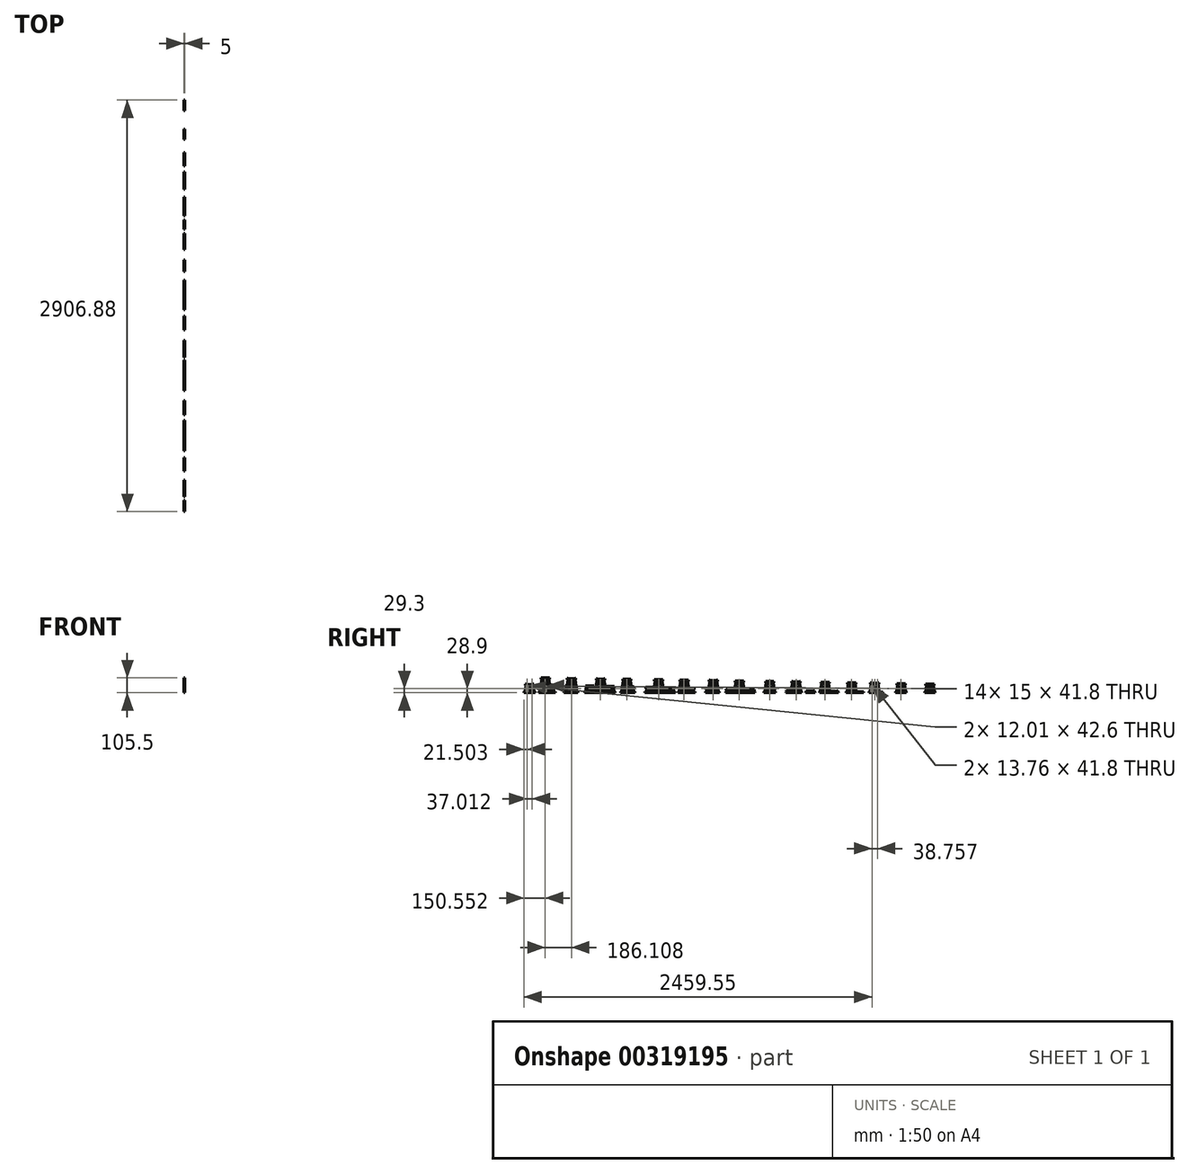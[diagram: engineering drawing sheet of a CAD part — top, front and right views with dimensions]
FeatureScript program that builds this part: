
annotation { "Feature Type Name" : "Feature", "Feature Type Description" : "" }
export const myFeature = defineFeature(function(context is Context, id is Id, definition is map)
    precondition{}
    {
        {
            var Q0;
            Q0=qCreatedBy(makeId("Right.planeOp"),FACE);
            var sketch = newSketch(context, id + "F0", { "sketchPlane" : qUnion([Q0])});
            skLineSegment(sketch, "E0", {"start": v(0, 134.08) * mm, "end": v(0, 0) * mm, "construction": true});
            skLineSegment(sketch, "E1", {"start": v(-77.1, 0) * mm, "end": v(4239.96, 0) * mm, "construction": true});
            skLineSegment(sketch, "E2.bottom", {"start": v(-24.5, 104.5) * mm, "end": v(0, 104.5) * mm});
            skLineSegment(sketch, "E2.top", {"start": v(-19.5, 96.5) * mm, "end": v(-12.5, 96.5) * mm});
            skLineSegment(sketch, "E2.left", {"start": v(-24.5, 104.5) * mm, "end": v(-24.5, 102.5) * mm});
            skLineSegment(sketch, "E3.bottom", {"start": v(-45.1, 0) * mm, "end": v(45.1, 0) * mm});
            skLineSegment(sketch, "E3.left", {"start": v(-45.1, 0) * mm, "end": v(-45.1, 8) * mm});
            skLineSegment(sketch, "E4.left", {"start": v(-12.5, 96.5) * mm, "end": v(-12.5, 54.8) * mm});
            skLineSegment(sketch, "E5", {"start": v(-40.1, 8) * mm, "end": v(-24.5, 96.5) * mm});
            skLineSegment(sketch, "E6", {"start": v(-45.1, 8) * mm, "end": v(-40.1, 8) * mm});
            skLineSegment(sketch, "E7.trimOffspring", {"start": v(-32.6, 8) * mm, "end": v(-26.42, 49.8) * mm});
            skLineSegment(sketch, "E8.bottom", {"start": v(-30, 105.5) * mm, "end": v(-25, 105.5) * mm});
            skLineSegment(sketch, "E8.top", {"start": v(-30, 96.5) * mm, "end": v(-24.5, 96.5) * mm});
            skLineSegment(sketch, "E8.left", {"start": v(-30, 105.5) * mm, "end": v(-30, 96.5) * mm});
            skLineSegment(sketch, "E9.right", {"start": v(-25, 105.5) * mm, "end": v(-25, 102.5) * mm});
            skLineSegment(sketch, "E10", {"start": v(-25, 102.5) * mm, "end": v(-24.5, 102.5) * mm});
            skLineSegment(sketch, "E11", {"start": v(-7.5, 96.5) * mm, "end": v(-7.5, 54.8) * mm});
            skLineSegment(sketch, "E12.trimOffspring", {"start": v(-32.6, 8) * mm, "end": v(-12.5, 8) * mm});
            skLineSegment(sketch, "E13.trimOffspring", {"start": v(-7.5, 49.8) * mm, "end": v(-7.5, 8) * mm});
            skLineSegment(sketch, "E14.trimOffspring", {"start": v(-12.5, 49.8) * mm, "end": v(-12.5, 8) * mm});
            skLineSegment(sketch, "E15.trimOffspring", {"start": v(-25.67, 54.8) * mm, "end": v(-19.5, 96.5) * mm});
            skLineSegment(sketch, "E16", {"start": v(59.07, 96.5) * mm, "end": v(-79.32, 96.5) * mm, "construction": true});
            skLineSegment(sketch, "E17", {"start": v(-25.67, 54.8) * mm, "end": v(0, 54.8) * mm});
            skLineSegment(sketch, "E18", {"start": v(-7.5, 96.5) * mm, "end": v(0, 96.5) * mm});
            skLineSegment(sketch, "E19", {"start": v(-26.42, 49.8) * mm, "end": v(0, 49.8) * mm});
            skLineSegment(sketch, "E20.MirrorCS", {"start": v(24.5, 104.5) * mm, "end": v(0, 104.5) * mm});
            skLineSegment(sketch, "E21.MirrorCS", {"start": v(24.5, 104.5) * mm, "end": v(24.5, 102.5) * mm});
            skLineSegment(sketch, "E22.MirrorCS", {"start": v(25, 102.5) * mm, "end": v(24.5, 102.5) * mm});
            skLineSegment(sketch, "E23.MirrorCS", {"start": v(25, 105.5) * mm, "end": v(25, 102.5) * mm});
            skLineSegment(sketch, "E24.MirrorCS", {"start": v(30, 105.5) * mm, "end": v(25, 105.5) * mm});
            skLineSegment(sketch, "E25.MirrorCS", {"start": v(30, 105.5) * mm, "end": v(30, 96.5) * mm});
            skLineSegment(sketch, "E26.MirrorCS", {"start": v(30, 96.5) * mm, "end": v(24.5, 96.5) * mm});
            skLineSegment(sketch, "E27.MirrorCS", {"start": v(19.5, 96.5) * mm, "end": v(12.5, 96.5) * mm});
            skLineSegment(sketch, "E28.MirrorCS", {"start": v(7.5, 96.5) * mm, "end": v(0, 96.5) * mm});
            skLineSegment(sketch, "E29.MirrorCS", {"start": v(7.5, 96.5) * mm, "end": v(7.5, 54.8) * mm});
            skLineSegment(sketch, "E30.MirrorCS", {"start": v(12.5, 96.5) * mm, "end": v(12.5, 54.8) * mm});
            skLineSegment(sketch, "E31.MirrorCS", {"start": v(25.67, 54.8) * mm, "end": v(19.5, 96.5) * mm});
            skLineSegment(sketch, "E32.MirrorCS", {"start": v(40.1, 8) * mm, "end": v(24.5, 96.5) * mm});
            skLineSegment(sketch, "E33.MirrorCS", {"start": v(25.67, 54.8) * mm, "end": v(0, 54.8) * mm});
            skLineSegment(sketch, "E34.MirrorCS", {"start": v(26.42, 49.8) * mm, "end": v(0, 49.8) * mm});
            skLineSegment(sketch, "E35.MirrorCS", {"start": v(7.5, 49.8) * mm, "end": v(7.5, 8) * mm});
            skLineSegment(sketch, "E36.MirrorCS", {"start": v(12.5, 49.8) * mm, "end": v(12.5, 8) * mm});
            skLineSegment(sketch, "E37.MirrorCS", {"start": v(32.6, 8) * mm, "end": v(12.5, 8) * mm});
            skLineSegment(sketch, "E38.MirrorCS", {"start": v(32.6, 8) * mm, "end": v(26.42, 49.8) * mm});
            skPoint(sketch, "E39.orphan", {"position": v(-32.73, 49.8) * mm});
            skPoint(sketch, "E40.orphan", {"position": v(32.73, 49.8) * mm});
            skLineSegment(sketch, "E41", {"start": v(-7.5, 8) * mm, "end": v(0, 8) * mm});
            skLineSegment(sketch, "E42.MirrorCS", {"start": v(7.5, 8) * mm, "end": v(0, 8) * mm});
            skLineSegment(sketch, "E43.MirrorCS", {"start": v(45.1, 0) * mm, "end": v(45.1, 8) * mm});
            skLineSegment(sketch, "E44.MirrorCS", {"start": v(45.1, 8) * mm, "end": v(40.1, 8) * mm});
            skLineSegment(sketch, "E45", {"start": v(197.1, 85.33) * mm, "end": v(197.1, 0) * mm, "construction": true});
            skLineSegment(sketch, "E46", {"start": v(119.98, 0) * mm, "end": v(260.76, 0) * mm, "construction": true});
            skLineSegment(sketch, "E47.bottom", {"start": v(172.6, 104.5) * mm, "end": v(197.1, 104.5) * mm});
            skLineSegment(sketch, "E47.top", {"start": v(177.6, 96.5) * mm, "end": v(184.6, 96.5) * mm});
            skLineSegment(sketch, "E47.left", {"start": v(172.6, 104.5) * mm, "end": v(172.6, 102.5) * mm});
            skLineSegment(sketch, "E48.bottom", {"start": v(151.99, 0) * mm, "end": v(242.2, 0) * mm});
            skLineSegment(sketch, "E48.left", {"start": v(151.99, 0) * mm, "end": v(151.99, 8) * mm});
            skLineSegment(sketch, "E49.left", {"start": v(184.6, 96.5) * mm, "end": v(184.6, 54.8) * mm});
            skLineSegment(sketch, "E50", {"start": v(156.99, 8) * mm, "end": v(172.6, 96.5) * mm});
            skLineSegment(sketch, "E51", {"start": v(151.99, 8) * mm, "end": v(156.99, 8) * mm});
            skLineSegment(sketch, "E52.trimOffspring", {"start": v(164.49, 8) * mm, "end": v(170.68, 49.8) * mm});
            skLineSegment(sketch, "E53.bottom", {"start": v(167.1, 105.5) * mm, "end": v(172.1, 105.5) * mm});
            skLineSegment(sketch, "E53.top", {"start": v(167.1, 96.5) * mm, "end": v(172.6, 96.5) * mm});
            skLineSegment(sketch, "E53.left", {"start": v(167.1, 105.5) * mm, "end": v(167.1, 96.5) * mm});
            skLineSegment(sketch, "E54.right", {"start": v(172.1, 105.5) * mm, "end": v(172.1, 102.5) * mm});
            skLineSegment(sketch, "E55", {"start": v(172.1, 102.5) * mm, "end": v(172.6, 102.5) * mm});
            skLineSegment(sketch, "E56", {"start": v(189.6, 96.5) * mm, "end": v(189.6, 54.8) * mm});
            skLineSegment(sketch, "E57.trimOffspring", {"start": v(164.49, 8) * mm, "end": v(184.6, 8) * mm});
            skLineSegment(sketch, "E58.trimOffspring", {"start": v(189.6, 49.8) * mm, "end": v(189.6, 8) * mm});
            skLineSegment(sketch, "E59.trimOffspring", {"start": v(184.6, 49.8) * mm, "end": v(184.6, 8) * mm});
            skLineSegment(sketch, "E60.trimOffspring", {"start": v(171.42, 54.8) * mm, "end": v(177.6, 96.5) * mm});
            skLineSegment(sketch, "E61", {"start": v(256.16, 96.5) * mm, "end": v(117.77, 96.5) * mm, "construction": true});
            skLineSegment(sketch, "E62", {"start": v(171.42, 54.8) * mm, "end": v(197.1, 54.8) * mm});
            skLineSegment(sketch, "E63", {"start": v(189.6, 96.5) * mm, "end": v(197.1, 96.5) * mm});
            skLineSegment(sketch, "E64", {"start": v(170.68, 49.8) * mm, "end": v(197.1, 49.8) * mm});
            skLineSegment(sketch, "E65.MirrorCS", {"start": v(221.6, 104.5) * mm, "end": v(197.1, 104.5) * mm});
            skLineSegment(sketch, "E66.MirrorCS", {"start": v(221.6, 104.5) * mm, "end": v(221.6, 102.5) * mm});
            skLineSegment(sketch, "E67.MirrorCS", {"start": v(222.1, 102.5) * mm, "end": v(221.6, 102.5) * mm});
            skLineSegment(sketch, "E68.MirrorCS", {"start": v(222.1, 105.5) * mm, "end": v(222.1, 102.5) * mm});
            skLineSegment(sketch, "E69.MirrorCS", {"start": v(227.1, 105.5) * mm, "end": v(222.1, 105.5) * mm});
            skLineSegment(sketch, "E70.MirrorCS", {"start": v(227.1, 105.5) * mm, "end": v(227.1, 96.5) * mm});
            skLineSegment(sketch, "E71.MirrorCS", {"start": v(227.1, 96.5) * mm, "end": v(221.6, 96.5) * mm});
            skLineSegment(sketch, "E72.MirrorCS", {"start": v(216.6, 96.5) * mm, "end": v(209.6, 96.5) * mm});
            skLineSegment(sketch, "E73.MirrorCS", {"start": v(204.6, 96.5) * mm, "end": v(197.1, 96.5) * mm});
            skLineSegment(sketch, "E74.MirrorCS", {"start": v(204.6, 96.5) * mm, "end": v(204.6, 54.8) * mm});
            skLineSegment(sketch, "E75.MirrorCS", {"start": v(209.6, 96.5) * mm, "end": v(209.6, 54.8) * mm});
            skLineSegment(sketch, "E76.MirrorCS", {"start": v(222.77, 54.8) * mm, "end": v(216.6, 96.5) * mm});
            skLineSegment(sketch, "E77.MirrorCS", {"start": v(237.2, 8) * mm, "end": v(221.6, 96.5) * mm});
            skLineSegment(sketch, "E78.MirrorCS", {"start": v(222.77, 54.8) * mm, "end": v(197.1, 54.8) * mm});
            skLineSegment(sketch, "E79.MirrorCS", {"start": v(223.5, 49.8) * mm, "end": v(197.1, 49.8) * mm});
            skLineSegment(sketch, "E80.MirrorCS", {"start": v(204.6, 49.8) * mm, "end": v(204.6, 8) * mm});
            skLineSegment(sketch, "E81.MirrorCS", {"start": v(209.6, 49.8) * mm, "end": v(209.6, 8) * mm});
            skLineSegment(sketch, "E82.MirrorCS", {"start": v(229.7, 8) * mm, "end": v(209.6, 8) * mm});
            skLineSegment(sketch, "E83.MirrorCS", {"start": v(229.7, 8) * mm, "end": v(223.5, 49.8) * mm});
            skPoint(sketch, "E84.orphan", {"position": v(164.36, 49.8) * mm});
            skPoint(sketch, "E85.orphan", {"position": v(229.83, 49.8) * mm});
            skLineSegment(sketch, "E86", {"start": v(189.6, 8) * mm, "end": v(197.1, 8) * mm});
            skLineSegment(sketch, "E87.MirrorCS", {"start": v(204.6, 8) * mm, "end": v(197.1, 8) * mm});
            skLineSegment(sketch, "E88.MirrorCS", {"start": v(242.2, 0) * mm, "end": v(242.2, 8) * mm});
            skLineSegment(sketch, "E89.MirrorCS", {"start": v(242.2, 8) * mm, "end": v(237.2, 8) * mm});
            skLineSegment(sketch, "E90", {"start": v(383.2, 89.08) * mm, "end": v(383.2, 0) * mm, "construction": true});
            skLineSegment(sketch, "E91", {"start": v(315.11, 0) * mm, "end": v(455.9, 0) * mm, "construction": true});
            skLineSegment(sketch, "E92.bottom", {"start": v(358.7, 100.6) * mm, "end": v(383.2, 100.6) * mm});
            skLineSegment(sketch, "E92.top", {"start": v(363.7, 92.6) * mm, "end": v(370.7, 92.6) * mm});
            skLineSegment(sketch, "E92.left", {"start": v(358.7, 100.6) * mm, "end": v(358.7, 98.6) * mm});
            skLineSegment(sketch, "E93.bottom", {"start": v(338.78, 0) * mm, "end": v(427.62, 0) * mm});
            skLineSegment(sketch, "E93.left", {"start": v(338.78, 0) * mm, "end": v(338.78, 8) * mm});
            skLineSegment(sketch, "E94.left", {"start": v(370.7, 92.6) * mm, "end": v(370.7, 54.8) * mm});
            skLineSegment(sketch, "E95", {"start": v(343.78, 8) * mm, "end": v(358.7, 92.6) * mm});
            skLineSegment(sketch, "E96", {"start": v(338.78, 8) * mm, "end": v(343.78, 8) * mm});
            skLineSegment(sketch, "E97.trimOffspring", {"start": v(351.28, 8) * mm, "end": v(357.42, 49.8) * mm});
            skLineSegment(sketch, "E98.bottom", {"start": v(353.2, 101.6) * mm, "end": v(358.2, 101.6) * mm});
            skLineSegment(sketch, "E98.top", {"start": v(353.2, 92.6) * mm, "end": v(358.7, 92.6) * mm});
            skLineSegment(sketch, "E98.left", {"start": v(353.2, 101.6) * mm, "end": v(353.2, 92.6) * mm});
            skLineSegment(sketch, "E99.right", {"start": v(358.2, 101.6) * mm, "end": v(358.2, 98.6) * mm});
            skLineSegment(sketch, "E100", {"start": v(358.2, 98.6) * mm, "end": v(358.7, 98.6) * mm});
            skLineSegment(sketch, "E101", {"start": v(375.7, 92.6) * mm, "end": v(375.7, 54.8) * mm});
            skLineSegment(sketch, "E102.trimOffspring", {"start": v(351.28, 8) * mm, "end": v(370.7, 8) * mm});
            skLineSegment(sketch, "E103.trimOffspring", {"start": v(375.7, 49.8) * mm, "end": v(375.7, 8) * mm});
            skLineSegment(sketch, "E104.trimOffspring", {"start": v(370.7, 49.8) * mm, "end": v(370.7, 8) * mm});
            skLineSegment(sketch, "E105.trimOffspring", {"start": v(358.15, 54.8) * mm, "end": v(363.7, 92.6) * mm});
            skLineSegment(sketch, "E106", {"start": v(451.29, 92.6) * mm, "end": v(312.9, 92.6) * mm, "construction": true});
            skLineSegment(sketch, "E107", {"start": v(358.15, 54.8) * mm, "end": v(383.2, 54.8) * mm});
            skLineSegment(sketch, "E108", {"start": v(375.7, 92.6) * mm, "end": v(383.2, 92.6) * mm});
            skLineSegment(sketch, "E109", {"start": v(357.42, 49.8) * mm, "end": v(383.2, 49.8) * mm});
            skLineSegment(sketch, "E110.MirrorCS", {"start": v(407.7, 100.6) * mm, "end": v(383.2, 100.6) * mm});
            skLineSegment(sketch, "E111.MirrorCS", {"start": v(407.7, 100.6) * mm, "end": v(407.7, 98.6) * mm});
            skLineSegment(sketch, "E112.MirrorCS", {"start": v(408.2, 98.6) * mm, "end": v(407.7, 98.6) * mm});
            skLineSegment(sketch, "E113.MirrorCS", {"start": v(408.2, 101.6) * mm, "end": v(408.2, 98.6) * mm});
            skLineSegment(sketch, "E114.MirrorCS", {"start": v(413.2, 101.6) * mm, "end": v(408.2, 101.6) * mm});
            skLineSegment(sketch, "E115.MirrorCS", {"start": v(413.2, 101.6) * mm, "end": v(413.2, 92.6) * mm});
            skLineSegment(sketch, "E116.MirrorCS", {"start": v(413.2, 92.6) * mm, "end": v(407.7, 92.6) * mm});
            skLineSegment(sketch, "E117.MirrorCS", {"start": v(402.7, 92.6) * mm, "end": v(395.7, 92.6) * mm});
            skLineSegment(sketch, "E118.MirrorCS", {"start": v(390.7, 92.6) * mm, "end": v(383.2, 92.6) * mm});
            skLineSegment(sketch, "E119.MirrorCS", {"start": v(390.7, 92.6) * mm, "end": v(390.7, 54.8) * mm});
            skLineSegment(sketch, "E120.MirrorCS", {"start": v(395.7, 92.6) * mm, "end": v(395.7, 54.8) * mm});
            skLineSegment(sketch, "E121.MirrorCS", {"start": v(408.25, 54.8) * mm, "end": v(402.7, 92.6) * mm});
            skLineSegment(sketch, "E122.MirrorCS", {"start": v(422.62, 8) * mm, "end": v(407.7, 92.6) * mm});
            skLineSegment(sketch, "E123.MirrorCS", {"start": v(408.25, 54.8) * mm, "end": v(383.2, 54.8) * mm});
            skLineSegment(sketch, "E124.MirrorCS", {"start": v(408.98, 49.8) * mm, "end": v(383.2, 49.8) * mm});
            skLineSegment(sketch, "E125.MirrorCS", {"start": v(390.7, 49.8) * mm, "end": v(390.7, 8) * mm});
            skLineSegment(sketch, "E126.MirrorCS", {"start": v(395.7, 49.8) * mm, "end": v(395.7, 8) * mm});
            skLineSegment(sketch, "E127.MirrorCS", {"start": v(415.12, 8) * mm, "end": v(395.7, 8) * mm});
            skLineSegment(sketch, "E128.MirrorCS", {"start": v(415.12, 8) * mm, "end": v(408.98, 49.8) * mm});
            skPoint(sketch, "E129.orphan", {"position": v(351.15, 49.8) * mm});
            skPoint(sketch, "E130.orphan", {"position": v(415.25, 49.8) * mm});
            skLineSegment(sketch, "E131", {"start": v(375.7, 8) * mm, "end": v(383.2, 8) * mm});
            skLineSegment(sketch, "E132.MirrorCS", {"start": v(390.7, 8) * mm, "end": v(383.2, 8) * mm});
            skLineSegment(sketch, "E133.MirrorCS", {"start": v(427.62, 0) * mm, "end": v(427.62, 8) * mm});
            skLineSegment(sketch, "E134.MirrorCS", {"start": v(427.62, 8) * mm, "end": v(422.62, 8) * mm});
            skLineSegment(sketch, "E135", {"start": v(587.84, 113.08) * mm, "end": v(587.84, 0) * mm, "construction": true});
            skLineSegment(sketch, "E136", {"start": v(510.73, 0) * mm, "end": v(651.5, 0) * mm, "construction": true});
            skLineSegment(sketch, "E137.bottom", {"start": v(563.34, 96.7) * mm, "end": v(587.84, 96.7) * mm});
            skLineSegment(sketch, "E137.top", {"start": v(568.34, 88.7) * mm, "end": v(575.34, 88.7) * mm});
            skLineSegment(sketch, "E137.left", {"start": v(563.34, 96.7) * mm, "end": v(563.34, 94.7) * mm});
            skLineSegment(sketch, "E138.bottom", {"start": v(544.11, 0) * mm, "end": v(631.57, 0) * mm});
            skLineSegment(sketch, "E138.left", {"start": v(544.11, 0) * mm, "end": v(544.11, 8) * mm});
            skLineSegment(sketch, "E139.left", {"start": v(575.34, 88.7) * mm, "end": v(575.34, 54.8) * mm});
            skLineSegment(sketch, "E140", {"start": v(549.11, 8) * mm, "end": v(563.34, 88.7) * mm});
            skLineSegment(sketch, "E141", {"start": v(544.11, 8) * mm, "end": v(549.11, 8) * mm});
            skLineSegment(sketch, "E142.trimOffspring", {"start": v(556.61, 8) * mm, "end": v(562.69, 49.8) * mm});
            skLineSegment(sketch, "E143.bottom", {"start": v(557.84, 97.7) * mm, "end": v(562.84, 97.7) * mm});
            skLineSegment(sketch, "E143.top", {"start": v(557.84, 88.7) * mm, "end": v(563.34, 88.7) * mm});
            skLineSegment(sketch, "E143.left", {"start": v(557.84, 97.7) * mm, "end": v(557.84, 88.7) * mm});
            skLineSegment(sketch, "E144.right", {"start": v(562.84, 97.7) * mm, "end": v(562.84, 94.7) * mm});
            skLineSegment(sketch, "E145", {"start": v(562.84, 94.7) * mm, "end": v(563.34, 94.7) * mm});
            skLineSegment(sketch, "E146", {"start": v(580.34, 88.7) * mm, "end": v(580.34, 54.8) * mm});
            skLineSegment(sketch, "E147.trimOffspring", {"start": v(556.61, 8) * mm, "end": v(575.34, 8) * mm});
            skLineSegment(sketch, "E148.trimOffspring", {"start": v(580.34, 49.8) * mm, "end": v(580.34, 8) * mm});
            skLineSegment(sketch, "E149.trimOffspring", {"start": v(575.34, 49.8) * mm, "end": v(575.34, 8) * mm});
            skLineSegment(sketch, "E150.trimOffspring", {"start": v(563.41, 54.8) * mm, "end": v(568.34, 88.7) * mm});
            skLineSegment(sketch, "E151", {"start": v(646.9, 88.7) * mm, "end": v(508.52, 88.7) * mm, "construction": true});
            skLineSegment(sketch, "E152", {"start": v(563.41, 54.8) * mm, "end": v(587.84, 54.8) * mm});
            skLineSegment(sketch, "E153", {"start": v(580.34, 88.7) * mm, "end": v(587.84, 88.7) * mm});
            skLineSegment(sketch, "E154", {"start": v(562.69, 49.8) * mm, "end": v(587.84, 49.8) * mm});
            skLineSegment(sketch, "E155.MirrorCS", {"start": v(612.34, 96.7) * mm, "end": v(587.84, 96.7) * mm});
            skLineSegment(sketch, "E156.MirrorCS", {"start": v(612.34, 96.7) * mm, "end": v(612.34, 94.7) * mm});
            skLineSegment(sketch, "E157.MirrorCS", {"start": v(612.84, 94.7) * mm, "end": v(612.34, 94.7) * mm});
            skLineSegment(sketch, "E158.MirrorCS", {"start": v(612.84, 97.7) * mm, "end": v(612.84, 94.7) * mm});
            skLineSegment(sketch, "E159.MirrorCS", {"start": v(617.84, 97.7) * mm, "end": v(612.84, 97.7) * mm});
            skLineSegment(sketch, "E160.MirrorCS", {"start": v(617.84, 97.7) * mm, "end": v(617.84, 88.7) * mm});
            skLineSegment(sketch, "E161.MirrorCS", {"start": v(617.84, 88.7) * mm, "end": v(612.34, 88.7) * mm});
            skLineSegment(sketch, "E162.MirrorCS", {"start": v(607.34, 88.7) * mm, "end": v(600.34, 88.7) * mm});
            skLineSegment(sketch, "E163.MirrorCS", {"start": v(595.34, 88.7) * mm, "end": v(587.84, 88.7) * mm});
            skLineSegment(sketch, "E164.MirrorCS", {"start": v(595.34, 88.7) * mm, "end": v(595.34, 54.8) * mm});
            skLineSegment(sketch, "E165.MirrorCS", {"start": v(600.34, 88.7) * mm, "end": v(600.34, 54.8) * mm});
            skLineSegment(sketch, "E166.MirrorCS", {"start": v(612.27, 54.8) * mm, "end": v(607.34, 88.7) * mm});
            skLineSegment(sketch, "E167.MirrorCS", {"start": v(626.57, 8) * mm, "end": v(612.34, 88.7) * mm});
            skLineSegment(sketch, "E168.MirrorCS", {"start": v(612.27, 54.8) * mm, "end": v(587.84, 54.8) * mm});
            skLineSegment(sketch, "E169.MirrorCS", {"start": v(613, 49.8) * mm, "end": v(587.84, 49.8) * mm});
            skLineSegment(sketch, "E170.MirrorCS", {"start": v(595.34, 49.8) * mm, "end": v(595.34, 8) * mm});
            skLineSegment(sketch, "E171.MirrorCS", {"start": v(600.34, 49.8) * mm, "end": v(600.34, 8) * mm});
            skLineSegment(sketch, "E172.MirrorCS", {"start": v(619.07, 8) * mm, "end": v(600.34, 8) * mm});
            skLineSegment(sketch, "E173.MirrorCS", {"start": v(619.07, 8) * mm, "end": v(613, 49.8) * mm});
            skPoint(sketch, "E174.orphan", {"position": v(556.48, 49.8) * mm});
            skPoint(sketch, "E175.orphan", {"position": v(619.2, 49.8) * mm});
            skLineSegment(sketch, "E176", {"start": v(580.34, 8) * mm, "end": v(587.84, 8) * mm});
            skLineSegment(sketch, "E177.MirrorCS", {"start": v(595.34, 8) * mm, "end": v(587.84, 8) * mm});
            skLineSegment(sketch, "E178.MirrorCS", {"start": v(631.57, 0) * mm, "end": v(631.57, 8) * mm});
            skLineSegment(sketch, "E179.MirrorCS", {"start": v(631.57, 8) * mm, "end": v(626.57, 8) * mm});
            skLineSegment(sketch, "E180", {"start": v(773.95, 116.82) * mm, "end": v(773.95, 0) * mm, "construction": true});
            skLineSegment(sketch, "E181", {"start": v(705.86, 0) * mm, "end": v(846.64, 0) * mm, "construction": true});
            skLineSegment(sketch, "E182.bottom", {"start": v(749.45, 95.8) * mm, "end": v(773.95, 95.8) * mm});
            skLineSegment(sketch, "E182.top", {"start": v(754.45, 87.8) * mm, "end": v(761.45, 87.8) * mm});
            skLineSegment(sketch, "E182.left", {"start": v(749.45, 95.8) * mm, "end": v(749.45, 93.8) * mm});
            skLineSegment(sketch, "E183.bottom", {"start": v(730.38, 0) * mm, "end": v(817.52, 0) * mm});
            skLineSegment(sketch, "E183.left", {"start": v(730.38, 0) * mm, "end": v(730.38, 8) * mm});
            skLineSegment(sketch, "E184.left", {"start": v(761.45, 87.8) * mm, "end": v(761.45, 54.8) * mm});
            skLineSegment(sketch, "E185", {"start": v(735.38, 8) * mm, "end": v(749.45, 87.8) * mm});
            skLineSegment(sketch, "E186", {"start": v(730.38, 8) * mm, "end": v(735.38, 8) * mm});
            skLineSegment(sketch, "E187.trimOffspring", {"start": v(742.88, 8) * mm, "end": v(748.94, 49.8) * mm});
            skLineSegment(sketch, "E188.bottom", {"start": v(743.95, 96.8) * mm, "end": v(748.95, 96.8) * mm});
            skLineSegment(sketch, "E188.top", {"start": v(743.95, 87.8) * mm, "end": v(749.45, 87.8) * mm});
            skLineSegment(sketch, "E188.left", {"start": v(743.95, 96.8) * mm, "end": v(743.95, 87.8) * mm});
            skLineSegment(sketch, "E189.right", {"start": v(748.95, 96.8) * mm, "end": v(748.95, 93.8) * mm});
            skLineSegment(sketch, "E190", {"start": v(748.95, 93.8) * mm, "end": v(749.45, 93.8) * mm});
            skLineSegment(sketch, "E191", {"start": v(766.45, 87.8) * mm, "end": v(766.45, 54.8) * mm});
            skLineSegment(sketch, "E192.trimOffspring", {"start": v(742.88, 8) * mm, "end": v(761.45, 8) * mm});
            skLineSegment(sketch, "E193.trimOffspring", {"start": v(766.45, 49.8) * mm, "end": v(766.45, 8) * mm});
            skLineSegment(sketch, "E194.trimOffspring", {"start": v(761.45, 49.8) * mm, "end": v(761.45, 8) * mm});
            skLineSegment(sketch, "E195.trimOffspring", {"start": v(749.66, 54.8) * mm, "end": v(754.45, 87.8) * mm});
            skLineSegment(sketch, "E196", {"start": v(842.04, 87.8) * mm, "end": v(703.65, 87.8) * mm, "construction": true});
            skLineSegment(sketch, "E197", {"start": v(749.66, 54.8) * mm, "end": v(773.95, 54.8) * mm});
            skLineSegment(sketch, "E198", {"start": v(766.45, 87.8) * mm, "end": v(773.95, 87.8) * mm});
            skLineSegment(sketch, "E199", {"start": v(748.94, 49.8) * mm, "end": v(773.95, 49.8) * mm});
            skLineSegment(sketch, "E200.MirrorCS", {"start": v(798.45, 95.8) * mm, "end": v(773.95, 95.8) * mm});
            skLineSegment(sketch, "E201.MirrorCS", {"start": v(798.45, 95.8) * mm, "end": v(798.45, 93.8) * mm});
            skLineSegment(sketch, "E202.MirrorCS", {"start": v(798.95, 93.8) * mm, "end": v(798.45, 93.8) * mm});
            skLineSegment(sketch, "E203.MirrorCS", {"start": v(798.95, 96.8) * mm, "end": v(798.95, 93.8) * mm});
            skLineSegment(sketch, "E204.MirrorCS", {"start": v(803.95, 96.8) * mm, "end": v(798.95, 96.8) * mm});
            skLineSegment(sketch, "E205.MirrorCS", {"start": v(803.95, 96.8) * mm, "end": v(803.95, 87.8) * mm});
            skLineSegment(sketch, "E206.MirrorCS", {"start": v(803.95, 87.8) * mm, "end": v(798.45, 87.8) * mm});
            skLineSegment(sketch, "E207.MirrorCS", {"start": v(793.45, 87.8) * mm, "end": v(786.45, 87.8) * mm});
            skLineSegment(sketch, "E208.MirrorCS", {"start": v(781.45, 87.8) * mm, "end": v(773.95, 87.8) * mm});
            skLineSegment(sketch, "E209.MirrorCS", {"start": v(781.45, 87.8) * mm, "end": v(781.45, 54.8) * mm});
            skLineSegment(sketch, "E210.MirrorCS", {"start": v(786.45, 87.8) * mm, "end": v(786.45, 54.8) * mm});
            skLineSegment(sketch, "E211.MirrorCS", {"start": v(798.23, 54.8) * mm, "end": v(793.45, 87.8) * mm});
            skLineSegment(sketch, "E212.MirrorCS", {"start": v(812.52, 8) * mm, "end": v(798.45, 87.8) * mm});
            skLineSegment(sketch, "E213.MirrorCS", {"start": v(798.23, 54.8) * mm, "end": v(773.95, 54.8) * mm});
            skLineSegment(sketch, "E214.MirrorCS", {"start": v(798.96, 49.8) * mm, "end": v(773.95, 49.8) * mm});
            skLineSegment(sketch, "E215.MirrorCS", {"start": v(781.45, 49.8) * mm, "end": v(781.45, 8) * mm});
            skLineSegment(sketch, "E216.MirrorCS", {"start": v(786.45, 49.8) * mm, "end": v(786.45, 8) * mm});
            skLineSegment(sketch, "E217.MirrorCS", {"start": v(805.02, 8) * mm, "end": v(786.45, 8) * mm});
            skLineSegment(sketch, "E218.MirrorCS", {"start": v(805.02, 8) * mm, "end": v(798.96, 49.8) * mm});
            skPoint(sketch, "E219.orphan", {"position": v(742.75, 49.8) * mm});
            skPoint(sketch, "E220.orphan", {"position": v(805.15, 49.8) * mm});
            skLineSegment(sketch, "E221", {"start": v(766.45, 8) * mm, "end": v(773.95, 8) * mm});
            skLineSegment(sketch, "E222.MirrorCS", {"start": v(781.45, 8) * mm, "end": v(773.95, 8) * mm});
            skLineSegment(sketch, "E223.MirrorCS", {"start": v(817.52, 0) * mm, "end": v(817.52, 8) * mm});
            skLineSegment(sketch, "E224.MirrorCS", {"start": v(817.52, 8) * mm, "end": v(812.52, 8) * mm});
            skLineSegment(sketch, "E225", {"start": v(998.65, 106.46) * mm, "end": v(998.65, 0) * mm, "construction": true});
            skLineSegment(sketch, "E226", {"start": v(917.44, 0) * mm, "end": v(1058.21, 0) * mm, "construction": true});
            skLineSegment(sketch, "E227.bottom", {"start": v(974.15, 91.9) * mm, "end": v(998.65, 91.9) * mm});
            skLineSegment(sketch, "E227.top", {"start": v(979.15, 83.9) * mm, "end": v(986.15, 83.9) * mm});
            skLineSegment(sketch, "E227.left", {"start": v(974.15, 91.9) * mm, "end": v(974.15, 89.9) * mm});
            skLineSegment(sketch, "E228.bottom", {"start": v(955.77, 0) * mm, "end": v(1041.54, 0) * mm});
            skLineSegment(sketch, "E228.left", {"start": v(955.77, 0) * mm, "end": v(955.77, 8) * mm});
            skLineSegment(sketch, "E229.left", {"start": v(986.15, 83.9) * mm, "end": v(986.15, 54.8) * mm});
            skLineSegment(sketch, "E230", {"start": v(960.77, 8) * mm, "end": v(974.15, 83.9) * mm});
            skLineSegment(sketch, "E231", {"start": v(955.77, 8) * mm, "end": v(960.77, 8) * mm});
            skLineSegment(sketch, "E232.trimOffspring", {"start": v(968.27, 8) * mm, "end": v(974.26, 49.8) * mm});
            skLineSegment(sketch, "E233.bottom", {"start": v(968.65, 92.9) * mm, "end": v(973.65, 92.9) * mm});
            skLineSegment(sketch, "E233.top", {"start": v(968.65, 83.9) * mm, "end": v(974.15, 83.9) * mm});
            skLineSegment(sketch, "E233.left", {"start": v(968.65, 92.9) * mm, "end": v(968.65, 83.9) * mm});
            skLineSegment(sketch, "E234.right", {"start": v(973.65, 92.9) * mm, "end": v(973.65, 89.9) * mm});
            skLineSegment(sketch, "E235", {"start": v(973.65, 89.9) * mm, "end": v(974.15, 89.9) * mm});
            skLineSegment(sketch, "E236", {"start": v(991.15, 83.9) * mm, "end": v(991.15, 54.8) * mm});
            skLineSegment(sketch, "E237.trimOffspring", {"start": v(968.27, 8) * mm, "end": v(986.15, 8) * mm});
            skLineSegment(sketch, "E238.trimOffspring", {"start": v(991.15, 49.8) * mm, "end": v(991.15, 8) * mm});
            skLineSegment(sketch, "E239.trimOffspring", {"start": v(986.15, 49.8) * mm, "end": v(986.15, 8) * mm});
            skLineSegment(sketch, "E240.trimOffspring", {"start": v(974.98, 54.8) * mm, "end": v(979.15, 83.9) * mm});
            skLineSegment(sketch, "E241", {"start": v(1053.61, 83.9) * mm, "end": v(915.23, 83.9) * mm, "construction": true});
            skLineSegment(sketch, "E242", {"start": v(974.98, 54.8) * mm, "end": v(998.65, 54.8) * mm});
            skLineSegment(sketch, "E243", {"start": v(991.15, 83.9) * mm, "end": v(998.65, 83.9) * mm});
            skLineSegment(sketch, "E244", {"start": v(974.26, 49.8) * mm, "end": v(998.65, 49.8) * mm});
            skLineSegment(sketch, "E245.MirrorCS", {"start": v(1023.15, 91.9) * mm, "end": v(998.65, 91.9) * mm});
            skLineSegment(sketch, "E246.MirrorCS", {"start": v(1023.15, 91.9) * mm, "end": v(1023.15, 89.9) * mm});
            skLineSegment(sketch, "E247.MirrorCS", {"start": v(1023.65, 89.9) * mm, "end": v(1023.15, 89.9) * mm});
            skLineSegment(sketch, "E248.MirrorCS", {"start": v(1023.65, 92.9) * mm, "end": v(1023.65, 89.9) * mm});
            skLineSegment(sketch, "E249.MirrorCS", {"start": v(1028.65, 92.9) * mm, "end": v(1023.65, 92.9) * mm});
            skLineSegment(sketch, "E250.MirrorCS", {"start": v(1028.65, 92.9) * mm, "end": v(1028.65, 83.9) * mm});
            skLineSegment(sketch, "E251.MirrorCS", {"start": v(1028.65, 83.9) * mm, "end": v(1023.15, 83.9) * mm});
            skLineSegment(sketch, "E252.MirrorCS", {"start": v(1018.15, 83.9) * mm, "end": v(1011.15, 83.9) * mm});
            skLineSegment(sketch, "E253.MirrorCS", {"start": v(1006.15, 83.9) * mm, "end": v(998.65, 83.9) * mm});
            skLineSegment(sketch, "E254.MirrorCS", {"start": v(1006.15, 83.9) * mm, "end": v(1006.15, 54.8) * mm});
            skLineSegment(sketch, "E255.MirrorCS", {"start": v(1011.15, 83.9) * mm, "end": v(1011.15, 54.8) * mm});
            skLineSegment(sketch, "E256.MirrorCS", {"start": v(1022.33, 54.8) * mm, "end": v(1018.15, 83.9) * mm});
            skLineSegment(sketch, "E257.MirrorCS", {"start": v(1036.54, 8) * mm, "end": v(1023.15, 83.9) * mm});
            skLineSegment(sketch, "E258.MirrorCS", {"start": v(1022.33, 54.8) * mm, "end": v(998.65, 54.8) * mm});
            skLineSegment(sketch, "E259.MirrorCS", {"start": v(1023.04, 49.8) * mm, "end": v(998.65, 49.8) * mm});
            skLineSegment(sketch, "E260.MirrorCS", {"start": v(1006.15, 49.8) * mm, "end": v(1006.15, 8) * mm});
            skLineSegment(sketch, "E261.MirrorCS", {"start": v(1011.15, 49.8) * mm, "end": v(1011.15, 8) * mm});
            skLineSegment(sketch, "E262.MirrorCS", {"start": v(1029.04, 8) * mm, "end": v(1011.15, 8) * mm});
            skLineSegment(sketch, "E263.MirrorCS", {"start": v(1029.04, 8) * mm, "end": v(1023.04, 49.8) * mm});
            skPoint(sketch, "E264.orphan", {"position": v(968.14, 49.8) * mm});
            skPoint(sketch, "E265.orphan", {"position": v(1029.17, 49.8) * mm});
            skLineSegment(sketch, "E266", {"start": v(991.15, 8) * mm, "end": v(998.65, 8) * mm});
            skLineSegment(sketch, "E267.MirrorCS", {"start": v(1006.15, 8) * mm, "end": v(998.65, 8) * mm});
            skLineSegment(sketch, "E268.MirrorCS", {"start": v(1041.54, 0) * mm, "end": v(1041.54, 8) * mm});
            skLineSegment(sketch, "E269.MirrorCS", {"start": v(1041.54, 8) * mm, "end": v(1036.54, 8) * mm});
            skLineSegment(sketch, "E270", {"start": v(1178.73, 105.45) * mm, "end": v(1178.73, 0) * mm, "construction": true});
            skLineSegment(sketch, "E271", {"start": v(1112.57, 0) * mm, "end": v(1253.34, 0) * mm, "construction": true});
            skLineSegment(sketch, "E272.bottom", {"start": v(1154.23, 88) * mm, "end": v(1178.73, 88) * mm});
            skLineSegment(sketch, "E272.top", {"start": v(1159.23, 80) * mm, "end": v(1166.23, 80) * mm});
            skLineSegment(sketch, "E272.left", {"start": v(1154.23, 88) * mm, "end": v(1154.23, 86) * mm});
            skLineSegment(sketch, "E273.bottom", {"start": v(1136.53, 0) * mm, "end": v(1220.92, 0) * mm});
            skLineSegment(sketch, "E273.left", {"start": v(1136.53, 0) * mm, "end": v(1136.53, 8) * mm});
            skLineSegment(sketch, "E274.left", {"start": v(1166.23, 80) * mm, "end": v(1166.23, 54.8) * mm});
            skLineSegment(sketch, "E275", {"start": v(1141.53, 8) * mm, "end": v(1154.23, 80) * mm});
            skLineSegment(sketch, "E276", {"start": v(1136.53, 8) * mm, "end": v(1141.53, 8) * mm});
            skLineSegment(sketch, "E277.trimOffspring", {"start": v(1149.03, 8) * mm, "end": v(1154.95, 49.8) * mm});
            skLineSegment(sketch, "E278.bottom", {"start": v(1148.73, 89) * mm, "end": v(1153.73, 89) * mm});
            skLineSegment(sketch, "E278.top", {"start": v(1148.73, 80) * mm, "end": v(1154.23, 80) * mm});
            skLineSegment(sketch, "E278.left", {"start": v(1148.73, 89) * mm, "end": v(1148.73, 80) * mm});
            skLineSegment(sketch, "E279.right", {"start": v(1153.73, 89) * mm, "end": v(1153.73, 86) * mm});
            skLineSegment(sketch, "E280", {"start": v(1153.73, 86) * mm, "end": v(1154.23, 86) * mm});
            skLineSegment(sketch, "E281", {"start": v(1171.23, 80) * mm, "end": v(1171.23, 54.8) * mm});
            skLineSegment(sketch, "E282.trimOffspring", {"start": v(1149.03, 8) * mm, "end": v(1166.23, 8) * mm});
            skLineSegment(sketch, "E283.trimOffspring", {"start": v(1171.23, 49.8) * mm, "end": v(1171.23, 8) * mm});
            skLineSegment(sketch, "E284.trimOffspring", {"start": v(1166.23, 49.8) * mm, "end": v(1166.23, 8) * mm});
            skLineSegment(sketch, "E285.trimOffspring", {"start": v(1155.66, 54.8) * mm, "end": v(1159.23, 80) * mm});
            skLineSegment(sketch, "E286", {"start": v(1248.74, 80) * mm, "end": v(1110.36, 80) * mm, "construction": true});
            skLineSegment(sketch, "E287", {"start": v(1155.66, 54.8) * mm, "end": v(1178.73, 54.8) * mm});
            skLineSegment(sketch, "E288", {"start": v(1171.23, 80) * mm, "end": v(1178.73, 80) * mm});
            skLineSegment(sketch, "E289", {"start": v(1154.95, 49.8) * mm, "end": v(1178.73, 49.8) * mm});
            skLineSegment(sketch, "E290.MirrorCS", {"start": v(1203.23, 88) * mm, "end": v(1178.73, 88) * mm});
            skLineSegment(sketch, "E291.MirrorCS", {"start": v(1203.23, 88) * mm, "end": v(1203.23, 86) * mm});
            skLineSegment(sketch, "E292.MirrorCS", {"start": v(1203.73, 86) * mm, "end": v(1203.23, 86) * mm});
            skLineSegment(sketch, "E293.MirrorCS", {"start": v(1203.73, 89) * mm, "end": v(1203.73, 86) * mm});
            skLineSegment(sketch, "E294.MirrorCS", {"start": v(1208.73, 89) * mm, "end": v(1203.73, 89) * mm});
            skLineSegment(sketch, "E295.MirrorCS", {"start": v(1208.73, 89) * mm, "end": v(1208.73, 80) * mm});
            skLineSegment(sketch, "E296.MirrorCS", {"start": v(1208.73, 80) * mm, "end": v(1203.23, 80) * mm});
            skLineSegment(sketch, "E297.MirrorCS", {"start": v(1198.23, 80) * mm, "end": v(1191.23, 80) * mm});
            skLineSegment(sketch, "E298.MirrorCS", {"start": v(1186.23, 80) * mm, "end": v(1178.73, 80) * mm});
            skLineSegment(sketch, "E299.MirrorCS", {"start": v(1186.23, 80) * mm, "end": v(1186.23, 54.8) * mm});
            skLineSegment(sketch, "E300.MirrorCS", {"start": v(1191.23, 80) * mm, "end": v(1191.23, 54.8) * mm});
            skLineSegment(sketch, "E301.MirrorCS", {"start": v(1201.8, 54.8) * mm, "end": v(1198.23, 80) * mm});
            skLineSegment(sketch, "E302.MirrorCS", {"start": v(1215.92, 8) * mm, "end": v(1203.23, 80) * mm});
            skLineSegment(sketch, "E303.MirrorCS", {"start": v(1201.8, 54.8) * mm, "end": v(1178.73, 54.8) * mm});
            skLineSegment(sketch, "E304.MirrorCS", {"start": v(1202.5, 49.8) * mm, "end": v(1178.73, 49.8) * mm});
            skLineSegment(sketch, "E305.MirrorCS", {"start": v(1186.23, 49.8) * mm, "end": v(1186.23, 8) * mm});
            skLineSegment(sketch, "E306.MirrorCS", {"start": v(1191.23, 49.8) * mm, "end": v(1191.23, 8) * mm});
            skLineSegment(sketch, "E307.MirrorCS", {"start": v(1208.42, 8) * mm, "end": v(1191.23, 8) * mm});
            skLineSegment(sketch, "E308.MirrorCS", {"start": v(1208.42, 8) * mm, "end": v(1202.5, 49.8) * mm});
            skPoint(sketch, "E309.orphan", {"position": v(1148.9, 49.8) * mm});
            skPoint(sketch, "E310.orphan", {"position": v(1208.55, 49.8) * mm});
            skLineSegment(sketch, "E311", {"start": v(1171.23, 8) * mm, "end": v(1178.73, 8) * mm});
            skLineSegment(sketch, "E312.MirrorCS", {"start": v(1186.23, 8) * mm, "end": v(1178.73, 8) * mm});
            skLineSegment(sketch, "E313.MirrorCS", {"start": v(1220.92, 0) * mm, "end": v(1220.92, 8) * mm});
            skLineSegment(sketch, "E314.MirrorCS", {"start": v(1220.92, 8) * mm, "end": v(1215.92, 8) * mm});
            skLineSegment(sketch, "E315", {"start": v(1385.06, 114.47) * mm, "end": v(1385.06, 0) * mm, "construction": true});
            skLineSegment(sketch, "E316", {"start": v(1308.18, 0) * mm, "end": v(1448.96, 0) * mm, "construction": true});
            skLineSegment(sketch, "E317.bottom", {"start": v(1360.56, 87.1) * mm, "end": v(1385.06, 87.1) * mm});
            skLineSegment(sketch, "E317.top", {"start": v(1365.56, 79.1) * mm, "end": v(1372.56, 79.1) * mm});
            skLineSegment(sketch, "E317.left", {"start": v(1360.56, 87.1) * mm, "end": v(1360.56, 85.1) * mm});
            skLineSegment(sketch, "E318.bottom", {"start": v(1343.03, 0) * mm, "end": v(1427.1, 0) * mm});
            skLineSegment(sketch, "E318.left", {"start": v(1343.03, 0) * mm, "end": v(1343.03, 8) * mm});
            skLineSegment(sketch, "E319.left", {"start": v(1372.56, 79.1) * mm, "end": v(1372.56, 54.8) * mm});
            skLineSegment(sketch, "E320", {"start": v(1348.03, 8) * mm, "end": v(1360.56, 79.1) * mm});
            skLineSegment(sketch, "E321", {"start": v(1343.03, 8) * mm, "end": v(1348.03, 8) * mm});
            skLineSegment(sketch, "E322.trimOffspring", {"start": v(1355.53, 8) * mm, "end": v(1361.43, 49.8) * mm});
            skLineSegment(sketch, "E323.bottom", {"start": v(1355.06, 88.1) * mm, "end": v(1360.06, 88.1) * mm});
            skLineSegment(sketch, "E323.top", {"start": v(1355.06, 79.1) * mm, "end": v(1360.56, 79.1) * mm});
            skLineSegment(sketch, "E323.left", {"start": v(1355.06, 88.1) * mm, "end": v(1355.06, 79.1) * mm});
            skLineSegment(sketch, "E324.right", {"start": v(1360.06, 88.1) * mm, "end": v(1360.06, 85.1) * mm});
            skLineSegment(sketch, "E325", {"start": v(1360.06, 85.1) * mm, "end": v(1360.56, 85.1) * mm});
            skLineSegment(sketch, "E326", {"start": v(1377.56, 79.1) * mm, "end": v(1377.56, 54.8) * mm});
            skLineSegment(sketch, "E327.trimOffspring", {"start": v(1355.53, 8) * mm, "end": v(1372.56, 8) * mm});
            skLineSegment(sketch, "E328.trimOffspring", {"start": v(1377.56, 49.8) * mm, "end": v(1377.56, 8) * mm});
            skLineSegment(sketch, "E329.trimOffspring", {"start": v(1372.56, 49.8) * mm, "end": v(1372.56, 8) * mm});
            skLineSegment(sketch, "E330.trimOffspring", {"start": v(1362.13, 54.8) * mm, "end": v(1365.56, 79.1) * mm});
            skLineSegment(sketch, "E331", {"start": v(1444.36, 79.1) * mm, "end": v(1305.97, 79.1) * mm, "construction": true});
            skLineSegment(sketch, "E332", {"start": v(1362.13, 54.8) * mm, "end": v(1385.06, 54.8) * mm});
            skLineSegment(sketch, "E333", {"start": v(1377.56, 79.1) * mm, "end": v(1385.06, 79.1) * mm});
            skLineSegment(sketch, "E334", {"start": v(1361.43, 49.8) * mm, "end": v(1385.06, 49.8) * mm});
            skLineSegment(sketch, "E335.MirrorCS", {"start": v(1409.56, 87.1) * mm, "end": v(1385.06, 87.1) * mm});
            skLineSegment(sketch, "E336.MirrorCS", {"start": v(1409.56, 87.1) * mm, "end": v(1409.56, 85.1) * mm});
            skLineSegment(sketch, "E337.MirrorCS", {"start": v(1410.06, 85.1) * mm, "end": v(1409.56, 85.1) * mm});
            skLineSegment(sketch, "E338.MirrorCS", {"start": v(1410.06, 88.1) * mm, "end": v(1410.06, 85.1) * mm});
            skLineSegment(sketch, "E339.MirrorCS", {"start": v(1415.06, 88.1) * mm, "end": v(1410.06, 88.1) * mm});
            skLineSegment(sketch, "E340.MirrorCS", {"start": v(1415.06, 88.1) * mm, "end": v(1415.06, 79.1) * mm});
            skLineSegment(sketch, "E341.MirrorCS", {"start": v(1415.06, 79.1) * mm, "end": v(1409.56, 79.1) * mm});
            skLineSegment(sketch, "E342.MirrorCS", {"start": v(1404.56, 79.1) * mm, "end": v(1397.56, 79.1) * mm});
            skLineSegment(sketch, "E343.MirrorCS", {"start": v(1392.56, 79.1) * mm, "end": v(1385.06, 79.1) * mm});
            skLineSegment(sketch, "E344.MirrorCS", {"start": v(1392.56, 79.1) * mm, "end": v(1392.56, 54.8) * mm});
            skLineSegment(sketch, "E345.MirrorCS", {"start": v(1397.56, 79.1) * mm, "end": v(1397.56, 54.8) * mm});
            skLineSegment(sketch, "E346.MirrorCS", {"start": v(1408, 54.8) * mm, "end": v(1404.56, 79.1) * mm});
            skLineSegment(sketch, "E347.MirrorCS", {"start": v(1422.1, 8) * mm, "end": v(1409.56, 79.1) * mm});
            skLineSegment(sketch, "E348.MirrorCS", {"start": v(1408, 54.8) * mm, "end": v(1385.06, 54.8) * mm});
            skLineSegment(sketch, "E349.MirrorCS", {"start": v(1408.7, 49.8) * mm, "end": v(1385.06, 49.8) * mm});
            skLineSegment(sketch, "E350.MirrorCS", {"start": v(1392.56, 49.8) * mm, "end": v(1392.56, 8) * mm});
            skLineSegment(sketch, "E351.MirrorCS", {"start": v(1397.56, 49.8) * mm, "end": v(1397.56, 8) * mm});
            skLineSegment(sketch, "E352.MirrorCS", {"start": v(1414.6, 8) * mm, "end": v(1397.56, 8) * mm});
            skLineSegment(sketch, "E353.MirrorCS", {"start": v(1414.6, 8) * mm, "end": v(1408.7, 49.8) * mm});
            skPoint(sketch, "E354.orphan", {"position": v(1355.4, 49.8) * mm});
            skPoint(sketch, "E355.orphan", {"position": v(1414.73, 49.8) * mm});
            skLineSegment(sketch, "E356", {"start": v(1377.56, 8) * mm, "end": v(1385.06, 8) * mm});
            skLineSegment(sketch, "E357.MirrorCS", {"start": v(1392.56, 8) * mm, "end": v(1385.06, 8) * mm});
            skLineSegment(sketch, "E358.MirrorCS", {"start": v(1427.1, 0) * mm, "end": v(1427.1, 8) * mm});
            skLineSegment(sketch, "E359.MirrorCS", {"start": v(1427.1, 8) * mm, "end": v(1422.1, 8) * mm});
            skLineSegment(sketch, "E360", {"start": v(1568.9, 104.74) * mm, "end": v(1568.9, 0) * mm, "construction": true});
            skLineSegment(sketch, "E361", {"start": v(1503.32, 0) * mm, "end": v(1644.1, 0) * mm, "construction": true});
            skLineSegment(sketch, "E362.bottom", {"start": v(1544.4, 83.2) * mm, "end": v(1568.9, 83.2) * mm});
            skLineSegment(sketch, "E362.top", {"start": v(1549.4, 75.2) * mm, "end": v(1556.4, 75.2) * mm});
            skLineSegment(sketch, "E362.left", {"start": v(1544.4, 83.2) * mm, "end": v(1544.4, 81.2) * mm});
            skLineSegment(sketch, "E363.bottom", {"start": v(1527.54, 0) * mm, "end": v(1610.24, 0) * mm});
            skLineSegment(sketch, "E363.left", {"start": v(1527.54, 0) * mm, "end": v(1527.54, 8) * mm});
            skLineSegment(sketch, "E364.left", {"start": v(1556.4, 75.2) * mm, "end": v(1556.4, 54.8) * mm});
            skLineSegment(sketch, "E365", {"start": v(1532.54, 8) * mm, "end": v(1544.4, 75.2) * mm});
            skLineSegment(sketch, "E366", {"start": v(1527.54, 8) * mm, "end": v(1532.54, 8) * mm});
            skLineSegment(sketch, "E367.trimOffspring", {"start": v(1540.04, 8) * mm, "end": v(1545.86, 49.8) * mm});
            skLineSegment(sketch, "E368.bottom", {"start": v(1538.9, 84.2) * mm, "end": v(1543.9, 84.2) * mm});
            skLineSegment(sketch, "E368.top", {"start": v(1538.9, 75.2) * mm, "end": v(1544.4, 75.2) * mm});
            skLineSegment(sketch, "E368.left", {"start": v(1538.9, 84.2) * mm, "end": v(1538.9, 75.2) * mm});
            skLineSegment(sketch, "E369.right", {"start": v(1543.9, 84.2) * mm, "end": v(1543.9, 81.2) * mm});
            skLineSegment(sketch, "E370", {"start": v(1543.9, 81.2) * mm, "end": v(1544.4, 81.2) * mm});
            skLineSegment(sketch, "E371", {"start": v(1561.4, 75.2) * mm, "end": v(1561.4, 54.8) * mm});
            skLineSegment(sketch, "E372.trimOffspring", {"start": v(1540.04, 8) * mm, "end": v(1556.4, 8) * mm});
            skLineSegment(sketch, "E373.trimOffspring", {"start": v(1561.4, 49.8) * mm, "end": v(1561.4, 8) * mm});
            skLineSegment(sketch, "E374.trimOffspring", {"start": v(1556.4, 49.8) * mm, "end": v(1556.4, 8) * mm});
            skLineSegment(sketch, "E375.trimOffspring", {"start": v(1546.55, 54.8) * mm, "end": v(1549.4, 75.2) * mm});
            skLineSegment(sketch, "E376", {"start": v(1639.5, 75.2) * mm, "end": v(1501.1, 75.2) * mm, "construction": true});
            skLineSegment(sketch, "E377", {"start": v(1546.55, 54.8) * mm, "end": v(1568.9, 54.8) * mm});
            skLineSegment(sketch, "E378", {"start": v(1561.4, 75.2) * mm, "end": v(1568.9, 75.2) * mm});
            skLineSegment(sketch, "E379", {"start": v(1545.86, 49.8) * mm, "end": v(1568.9, 49.8) * mm});
            skLineSegment(sketch, "E380.MirrorCS", {"start": v(1593.4, 83.2) * mm, "end": v(1568.9, 83.2) * mm});
            skLineSegment(sketch, "E381.MirrorCS", {"start": v(1593.4, 83.2) * mm, "end": v(1593.4, 81.2) * mm});
            skLineSegment(sketch, "E382.MirrorCS", {"start": v(1593.9, 81.2) * mm, "end": v(1593.4, 81.2) * mm});
            skLineSegment(sketch, "E383.MirrorCS", {"start": v(1593.9, 84.2) * mm, "end": v(1593.9, 81.2) * mm});
            skLineSegment(sketch, "E384.MirrorCS", {"start": v(1598.9, 84.2) * mm, "end": v(1593.9, 84.2) * mm});
            skLineSegment(sketch, "E385.MirrorCS", {"start": v(1598.9, 84.2) * mm, "end": v(1598.9, 75.2) * mm});
            skLineSegment(sketch, "E386.MirrorCS", {"start": v(1598.9, 75.2) * mm, "end": v(1593.4, 75.2) * mm});
            skLineSegment(sketch, "E387.MirrorCS", {"start": v(1588.4, 75.2) * mm, "end": v(1581.4, 75.2) * mm});
            skLineSegment(sketch, "E388.MirrorCS", {"start": v(1576.4, 75.2) * mm, "end": v(1568.9, 75.2) * mm});
            skLineSegment(sketch, "E389.MirrorCS", {"start": v(1576.4, 75.2) * mm, "end": v(1576.4, 54.8) * mm});
            skLineSegment(sketch, "E390.MirrorCS", {"start": v(1581.4, 75.2) * mm, "end": v(1581.4, 54.8) * mm});
            skLineSegment(sketch, "E391.MirrorCS", {"start": v(1591.23, 54.8) * mm, "end": v(1588.4, 75.2) * mm});
            skLineSegment(sketch, "E392.MirrorCS", {"start": v(1605.24, 8) * mm, "end": v(1593.4, 75.2) * mm});
            skLineSegment(sketch, "E393.MirrorCS", {"start": v(1591.23, 54.8) * mm, "end": v(1568.9, 54.8) * mm});
            skLineSegment(sketch, "E394.MirrorCS", {"start": v(1591.92, 49.8) * mm, "end": v(1568.9, 49.8) * mm});
            skLineSegment(sketch, "E395.MirrorCS", {"start": v(1576.4, 49.8) * mm, "end": v(1576.4, 8) * mm});
            skLineSegment(sketch, "E396.MirrorCS", {"start": v(1581.4, 49.8) * mm, "end": v(1581.4, 8) * mm});
            skLineSegment(sketch, "E397.MirrorCS", {"start": v(1597.74, 8) * mm, "end": v(1581.4, 8) * mm});
            skLineSegment(sketch, "E398.MirrorCS", {"start": v(1597.74, 8) * mm, "end": v(1591.92, 49.8) * mm});
            skPoint(sketch, "E399.orphan", {"position": v(1539.91, 49.8) * mm});
            skPoint(sketch, "E400.orphan", {"position": v(1597.87, 49.8) * mm});
            skLineSegment(sketch, "E401", {"start": v(1561.4, 8) * mm, "end": v(1568.9, 8) * mm});
            skLineSegment(sketch, "E402.MirrorCS", {"start": v(1576.4, 8) * mm, "end": v(1568.9, 8) * mm});
            skLineSegment(sketch, "E403.MirrorCS", {"start": v(1610.24, 0) * mm, "end": v(1610.24, 8) * mm});
            skLineSegment(sketch, "E404.MirrorCS", {"start": v(1610.24, 8) * mm, "end": v(1605.24, 8) * mm});
            skLineSegment(sketch, "E405", {"start": v(1783.75, 120.9) * mm, "end": v(1783.75, 0) * mm, "construction": true});
            skLineSegment(sketch, "E406", {"start": v(1706.64, 0) * mm, "end": v(1847.42, 0) * mm, "construction": true});
            skLineSegment(sketch, "E407.bottom", {"start": v(1759.25, 79.3) * mm, "end": v(1783.75, 79.3) * mm});
            skLineSegment(sketch, "E407.top", {"start": v(1764.25, 71.3) * mm, "end": v(1771.25, 71.3) * mm});
            skLineSegment(sketch, "E407.left", {"start": v(1759.25, 79.3) * mm, "end": v(1759.25, 77.3) * mm});
            skLineSegment(sketch, "E408.bottom", {"start": v(1743.1, 0) * mm, "end": v(1824.42, 0) * mm});
            skLineSegment(sketch, "E408.left", {"start": v(1743.1, 0) * mm, "end": v(1743.1, 8) * mm});
            skLineSegment(sketch, "E409.left", {"start": v(1771.25, 71.3) * mm, "end": v(1771.25, 54.8) * mm});
            skLineSegment(sketch, "E410", {"start": v(1748.1, 8) * mm, "end": v(1759.25, 71.3) * mm});
            skLineSegment(sketch, "E411", {"start": v(1743.1, 8) * mm, "end": v(1748.1, 8) * mm});
            skLineSegment(sketch, "E412.trimOffspring", {"start": v(1755.6, 8) * mm, "end": v(1761.31, 49.8) * mm});
            skLineSegment(sketch, "E413.bottom", {"start": v(1753.75, 80.3) * mm, "end": v(1758.75, 80.3) * mm});
            skLineSegment(sketch, "E413.top", {"start": v(1753.75, 71.3) * mm, "end": v(1759.25, 71.3) * mm});
            skLineSegment(sketch, "E413.left", {"start": v(1753.75, 80.3) * mm, "end": v(1753.75, 71.3) * mm});
            skLineSegment(sketch, "E414.right", {"start": v(1758.75, 80.3) * mm, "end": v(1758.75, 77.3) * mm});
            skLineSegment(sketch, "E415", {"start": v(1758.75, 77.3) * mm, "end": v(1759.25, 77.3) * mm});
            skLineSegment(sketch, "E416", {"start": v(1776.25, 71.3) * mm, "end": v(1776.25, 54.8) * mm});
            skLineSegment(sketch, "E417.trimOffspring", {"start": v(1755.6, 8) * mm, "end": v(1771.25, 8) * mm});
            skLineSegment(sketch, "E418.trimOffspring", {"start": v(1776.25, 49.8) * mm, "end": v(1776.25, 8) * mm});
            skLineSegment(sketch, "E419.trimOffspring", {"start": v(1771.25, 49.8) * mm, "end": v(1771.25, 8) * mm});
            skLineSegment(sketch, "E420.trimOffspring", {"start": v(1762, 54.8) * mm, "end": v(1764.25, 71.3) * mm});
            skLineSegment(sketch, "E421", {"start": v(1842.82, 71.3) * mm, "end": v(1704.43, 71.3) * mm, "construction": true});
            skLineSegment(sketch, "E422", {"start": v(1762, 54.8) * mm, "end": v(1783.75, 54.8) * mm});
            skLineSegment(sketch, "E423", {"start": v(1776.25, 71.3) * mm, "end": v(1783.75, 71.3) * mm});
            skLineSegment(sketch, "E424", {"start": v(1761.31, 49.8) * mm, "end": v(1783.75, 49.8) * mm});
            skLineSegment(sketch, "E425.MirrorCS", {"start": v(1808.25, 79.3) * mm, "end": v(1783.75, 79.3) * mm});
            skLineSegment(sketch, "E426.MirrorCS", {"start": v(1808.25, 79.3) * mm, "end": v(1808.25, 77.3) * mm});
            skLineSegment(sketch, "E427.MirrorCS", {"start": v(1808.75, 77.3) * mm, "end": v(1808.25, 77.3) * mm});
            skLineSegment(sketch, "E428.MirrorCS", {"start": v(1808.75, 80.3) * mm, "end": v(1808.75, 77.3) * mm});
            skLineSegment(sketch, "E429.MirrorCS", {"start": v(1813.75, 80.3) * mm, "end": v(1808.75, 80.3) * mm});
            skLineSegment(sketch, "E430.MirrorCS", {"start": v(1813.75, 80.3) * mm, "end": v(1813.75, 71.3) * mm});
            skLineSegment(sketch, "E431.MirrorCS", {"start": v(1813.75, 71.3) * mm, "end": v(1808.25, 71.3) * mm});
            skLineSegment(sketch, "E432.MirrorCS", {"start": v(1803.25, 71.3) * mm, "end": v(1796.25, 71.3) * mm});
            skLineSegment(sketch, "E433.MirrorCS", {"start": v(1791.25, 71.3) * mm, "end": v(1783.75, 71.3) * mm});
            skLineSegment(sketch, "E434.MirrorCS", {"start": v(1791.25, 71.3) * mm, "end": v(1791.25, 54.8) * mm});
            skLineSegment(sketch, "E435.MirrorCS", {"start": v(1796.25, 71.3) * mm, "end": v(1796.25, 54.8) * mm});
            skLineSegment(sketch, "E436.MirrorCS", {"start": v(1805.51, 54.8) * mm, "end": v(1803.25, 71.3) * mm});
            skLineSegment(sketch, "E437.MirrorCS", {"start": v(1819.42, 8) * mm, "end": v(1808.25, 71.3) * mm});
            skLineSegment(sketch, "E438.MirrorCS", {"start": v(1805.51, 54.8) * mm, "end": v(1783.75, 54.8) * mm});
            skLineSegment(sketch, "E439.MirrorCS", {"start": v(1806.2, 49.8) * mm, "end": v(1783.75, 49.8) * mm});
            skLineSegment(sketch, "E440.MirrorCS", {"start": v(1791.25, 49.8) * mm, "end": v(1791.25, 8) * mm});
            skLineSegment(sketch, "E441.MirrorCS", {"start": v(1796.25, 49.8) * mm, "end": v(1796.25, 8) * mm});
            skLineSegment(sketch, "E442.MirrorCS", {"start": v(1811.92, 8) * mm, "end": v(1796.25, 8) * mm});
            skLineSegment(sketch, "E443.MirrorCS", {"start": v(1811.92, 8) * mm, "end": v(1806.2, 49.8) * mm});
            skPoint(sketch, "E444.orphan", {"position": v(1755.46, 49.8) * mm});
            skPoint(sketch, "E445.orphan", {"position": v(1812.04, 49.8) * mm});
            skLineSegment(sketch, "E446", {"start": v(1776.25, 8) * mm, "end": v(1783.75, 8) * mm});
            skLineSegment(sketch, "E447.MirrorCS", {"start": v(1791.25, 8) * mm, "end": v(1783.75, 8) * mm});
            skLineSegment(sketch, "E448.MirrorCS", {"start": v(1824.42, 0) * mm, "end": v(1824.42, 8) * mm});
            skLineSegment(sketch, "E449.MirrorCS", {"start": v(1824.42, 8) * mm, "end": v(1819.42, 8) * mm});
            skLineSegment(sketch, "E450", {"start": v(1969.86, 124.64) * mm, "end": v(1969.86, 0) * mm, "construction": true});
            skLineSegment(sketch, "E451", {"start": v(1901.78, 0) * mm, "end": v(2042.55, 0) * mm, "construction": true});
            skLineSegment(sketch, "E452.bottom", {"start": v(1945.36, 78.4) * mm, "end": v(1969.86, 78.4) * mm});
            skLineSegment(sketch, "E452.top", {"start": v(1950.36, 70.4) * mm, "end": v(1957.36, 70.4) * mm});
            skLineSegment(sketch, "E452.left", {"start": v(1945.36, 78.4) * mm, "end": v(1945.36, 76.4) * mm});
            skLineSegment(sketch, "E453.bottom", {"start": v(1929.36, 0) * mm, "end": v(2010.36, 0) * mm});
            skLineSegment(sketch, "E453.left", {"start": v(1929.36, 0) * mm, "end": v(1929.36, 8) * mm});
            skLineSegment(sketch, "E454.left", {"start": v(1957.36, 70.4) * mm, "end": v(1957.36, 54.8) * mm});
            skLineSegment(sketch, "E455", {"start": v(1934.36, 8) * mm, "end": v(1945.36, 70.4) * mm});
            skLineSegment(sketch, "E456", {"start": v(1929.36, 8) * mm, "end": v(1934.36, 8) * mm});
            skLineSegment(sketch, "E457.trimOffspring", {"start": v(1941.86, 8) * mm, "end": v(1947.55, 49.8) * mm});
            skLineSegment(sketch, "E458.bottom", {"start": v(1939.86, 79.4) * mm, "end": v(1944.86, 79.4) * mm});
            skLineSegment(sketch, "E458.top", {"start": v(1939.86, 70.4) * mm, "end": v(1945.36, 70.4) * mm});
            skLineSegment(sketch, "E458.left", {"start": v(1939.86, 79.4) * mm, "end": v(1939.86, 70.4) * mm});
            skLineSegment(sketch, "E459.right", {"start": v(1944.86, 79.4) * mm, "end": v(1944.86, 76.4) * mm});
            skLineSegment(sketch, "E460", {"start": v(1944.86, 76.4) * mm, "end": v(1945.36, 76.4) * mm});
            skLineSegment(sketch, "E461", {"start": v(1962.36, 70.4) * mm, "end": v(1962.36, 54.8) * mm});
            skLineSegment(sketch, "E462.trimOffspring", {"start": v(1941.86, 8) * mm, "end": v(1957.36, 8) * mm});
            skLineSegment(sketch, "E463.trimOffspring", {"start": v(1962.36, 49.8) * mm, "end": v(1962.36, 8) * mm});
            skLineSegment(sketch, "E464.trimOffspring", {"start": v(1957.36, 49.8) * mm, "end": v(1957.36, 8) * mm});
            skLineSegment(sketch, "E465.trimOffspring", {"start": v(1948.24, 54.8) * mm, "end": v(1950.36, 70.4) * mm});
            skLineSegment(sketch, "E466", {"start": v(2037.95, 70.4) * mm, "end": v(1899.57, 70.4) * mm, "construction": true});
            skLineSegment(sketch, "E467", {"start": v(1948.24, 54.8) * mm, "end": v(1969.86, 54.8) * mm});
            skLineSegment(sketch, "E468", {"start": v(1962.36, 70.4) * mm, "end": v(1969.86, 70.4) * mm});
            skLineSegment(sketch, "E469", {"start": v(1947.55, 49.8) * mm, "end": v(1969.86, 49.8) * mm});
            skLineSegment(sketch, "E470.MirrorCS", {"start": v(1994.36, 78.4) * mm, "end": v(1969.86, 78.4) * mm});
            skLineSegment(sketch, "E471.MirrorCS", {"start": v(1994.36, 78.4) * mm, "end": v(1994.36, 76.4) * mm});
            skLineSegment(sketch, "E472.MirrorCS", {"start": v(1994.86, 76.4) * mm, "end": v(1994.36, 76.4) * mm});
            skLineSegment(sketch, "E473.MirrorCS", {"start": v(1994.86, 79.4) * mm, "end": v(1994.86, 76.4) * mm});
            skLineSegment(sketch, "E474.MirrorCS", {"start": v(1999.86, 79.4) * mm, "end": v(1994.86, 79.4) * mm});
            skLineSegment(sketch, "E475.MirrorCS", {"start": v(1999.86, 79.4) * mm, "end": v(1999.86, 70.4) * mm});
            skLineSegment(sketch, "E476.MirrorCS", {"start": v(1999.86, 70.4) * mm, "end": v(1994.36, 70.4) * mm});
            skLineSegment(sketch, "E477.MirrorCS", {"start": v(1989.36, 70.4) * mm, "end": v(1982.36, 70.4) * mm});
            skLineSegment(sketch, "E478.MirrorCS", {"start": v(1977.36, 70.4) * mm, "end": v(1969.86, 70.4) * mm});
            skLineSegment(sketch, "E479.MirrorCS", {"start": v(1977.36, 70.4) * mm, "end": v(1977.36, 54.8) * mm});
            skLineSegment(sketch, "E480.MirrorCS", {"start": v(1982.36, 70.4) * mm, "end": v(1982.36, 54.8) * mm});
            skLineSegment(sketch, "E481.MirrorCS", {"start": v(1991.49, 54.8) * mm, "end": v(1989.36, 70.4) * mm});
            skLineSegment(sketch, "E482.MirrorCS", {"start": v(2005.36, 8) * mm, "end": v(1994.36, 70.4) * mm});
            skLineSegment(sketch, "E483.MirrorCS", {"start": v(1991.49, 54.8) * mm, "end": v(1969.86, 54.8) * mm});
            skLineSegment(sketch, "E484.MirrorCS", {"start": v(1992.17, 49.8) * mm, "end": v(1969.86, 49.8) * mm});
            skLineSegment(sketch, "E485.MirrorCS", {"start": v(1977.36, 49.8) * mm, "end": v(1977.36, 8) * mm});
            skLineSegment(sketch, "E486.MirrorCS", {"start": v(1982.36, 49.8) * mm, "end": v(1982.36, 8) * mm});
            skLineSegment(sketch, "E487.MirrorCS", {"start": v(1997.86, 8) * mm, "end": v(1982.36, 8) * mm});
            skLineSegment(sketch, "E488.MirrorCS", {"start": v(1997.86, 8) * mm, "end": v(1992.17, 49.8) * mm});
            skPoint(sketch, "E489.orphan", {"position": v(1941.73, 49.8) * mm});
            skPoint(sketch, "E490.orphan", {"position": v(1998, 49.8) * mm});
            skLineSegment(sketch, "E491", {"start": v(1962.36, 8) * mm, "end": v(1969.86, 8) * mm});
            skLineSegment(sketch, "E492.MirrorCS", {"start": v(1977.36, 8) * mm, "end": v(1969.86, 8) * mm});
            skLineSegment(sketch, "E493.MirrorCS", {"start": v(2010.36, 0) * mm, "end": v(2010.36, 8) * mm});
            skLineSegment(sketch, "E494.MirrorCS", {"start": v(2010.36, 8) * mm, "end": v(2005.36, 8) * mm});
            skLineSegment(sketch, "E495", {"start": v(2175.5, 99.88) * mm, "end": v(2175.5, 0) * mm, "construction": true});
            skLineSegment(sketch, "E496", {"start": v(2097.4, 0) * mm, "end": v(2238.17, 0) * mm, "construction": true});
            skLineSegment(sketch, "E497.bottom", {"start": v(2151, 74) * mm, "end": v(2175.5, 74) * mm});
            skLineSegment(sketch, "E497.top", {"start": v(2156, 66) * mm, "end": v(2163, 66) * mm});
            skLineSegment(sketch, "E497.left", {"start": v(2151, 74) * mm, "end": v(2151, 72) * mm});
            skLineSegment(sketch, "E498.bottom", {"start": v(2135.77, 0) * mm, "end": v(2215.22, 0) * mm});
            skLineSegment(sketch, "E498.left", {"start": v(2135.77, 0) * mm, "end": v(2135.77, 8) * mm});
            skLineSegment(sketch, "E499.left", {"start": v(2163, 66) * mm, "end": v(2163, 54.8) * mm});
            skLineSegment(sketch, "E500", {"start": v(2140.77, 8) * mm, "end": v(2151, 66) * mm});
            skLineSegment(sketch, "E501", {"start": v(2135.77, 8) * mm, "end": v(2140.77, 8) * mm});
            skLineSegment(sketch, "E502.trimOffspring", {"start": v(2148.27, 8) * mm, "end": v(2153.84, 49.8) * mm});
            skLineSegment(sketch, "E503.bottom", {"start": v(2145.5, 75) * mm, "end": v(2150.5, 75) * mm});
            skLineSegment(sketch, "E503.top", {"start": v(2145.5, 66) * mm, "end": v(2151, 66) * mm});
            skLineSegment(sketch, "E503.left", {"start": v(2145.5, 75) * mm, "end": v(2145.5, 66) * mm});
            skLineSegment(sketch, "E504.right", {"start": v(2150.5, 75) * mm, "end": v(2150.5, 72) * mm});
            skLineSegment(sketch, "E505", {"start": v(2150.5, 72) * mm, "end": v(2151, 72) * mm});
            skLineSegment(sketch, "E506", {"start": v(2168, 66) * mm, "end": v(2168, 54.8) * mm});
            skLineSegment(sketch, "E507.trimOffspring", {"start": v(2148.27, 8) * mm, "end": v(2163, 8) * mm});
            skLineSegment(sketch, "E508.trimOffspring", {"start": v(2168, 49.8) * mm, "end": v(2168, 8) * mm});
            skLineSegment(sketch, "E509.trimOffspring", {"start": v(2163, 49.8) * mm, "end": v(2163, 8) * mm});
            skLineSegment(sketch, "E510.trimOffspring", {"start": v(2154.5, 54.8) * mm, "end": v(2156, 66) * mm});
            skLineSegment(sketch, "E511", {"start": v(2233.57, 66) * mm, "end": v(2095.18, 66) * mm, "construction": true});
            skLineSegment(sketch, "E512", {"start": v(2154.5, 54.8) * mm, "end": v(2175.5, 54.8) * mm});
            skLineSegment(sketch, "E513", {"start": v(2168, 66) * mm, "end": v(2175.5, 66) * mm});
            skLineSegment(sketch, "E514", {"start": v(2153.84, 49.8) * mm, "end": v(2175.5, 49.8) * mm});
            skLineSegment(sketch, "E515.MirrorCS", {"start": v(2200, 74) * mm, "end": v(2175.5, 74) * mm});
            skLineSegment(sketch, "E516.MirrorCS", {"start": v(2200, 74) * mm, "end": v(2200, 72) * mm});
            skLineSegment(sketch, "E517.MirrorCS", {"start": v(2200.5, 72) * mm, "end": v(2200, 72) * mm});
            skLineSegment(sketch, "E518.MirrorCS", {"start": v(2200.5, 75) * mm, "end": v(2200.5, 72) * mm});
            skLineSegment(sketch, "E519.MirrorCS", {"start": v(2205.5, 75) * mm, "end": v(2200.5, 75) * mm});
            skLineSegment(sketch, "E520.MirrorCS", {"start": v(2205.5, 75) * mm, "end": v(2205.5, 66) * mm});
            skLineSegment(sketch, "E521.MirrorCS", {"start": v(2205.5, 66) * mm, "end": v(2200, 66) * mm});
            skLineSegment(sketch, "E522.MirrorCS", {"start": v(2195, 66) * mm, "end": v(2188, 66) * mm});
            skLineSegment(sketch, "E523.MirrorCS", {"start": v(2183, 66) * mm, "end": v(2175.5, 66) * mm});
            skLineSegment(sketch, "E524.MirrorCS", {"start": v(2183, 66) * mm, "end": v(2183, 54.8) * mm});
            skLineSegment(sketch, "E525.MirrorCS", {"start": v(2188, 66) * mm, "end": v(2188, 54.8) * mm});
            skLineSegment(sketch, "E526.MirrorCS", {"start": v(2196.49, 54.8) * mm, "end": v(2195, 66) * mm});
            skLineSegment(sketch, "E527.MirrorCS", {"start": v(2210.22, 8) * mm, "end": v(2200, 66) * mm});
            skLineSegment(sketch, "E528.MirrorCS", {"start": v(2196.49, 54.8) * mm, "end": v(2175.5, 54.8) * mm});
            skLineSegment(sketch, "E529.MirrorCS", {"start": v(2197.16, 49.8) * mm, "end": v(2175.5, 49.8) * mm});
            skLineSegment(sketch, "E530.MirrorCS", {"start": v(2183, 49.8) * mm, "end": v(2183, 8) * mm});
            skLineSegment(sketch, "E531.MirrorCS", {"start": v(2188, 49.8) * mm, "end": v(2188, 8) * mm});
            skLineSegment(sketch, "E532.MirrorCS", {"start": v(2202.72, 8) * mm, "end": v(2188, 8) * mm});
            skLineSegment(sketch, "E533.MirrorCS", {"start": v(2202.72, 8) * mm, "end": v(2197.16, 49.8) * mm});
            skPoint(sketch, "E534.orphan", {"position": v(2148.14, 49.8) * mm});
            skPoint(sketch, "E535.orphan", {"position": v(2202.85, 49.8) * mm});
            skLineSegment(sketch, "E536", {"start": v(2168, 8) * mm, "end": v(2175.5, 8) * mm});
            skLineSegment(sketch, "E537.MirrorCS", {"start": v(2183, 8) * mm, "end": v(2175.5, 8) * mm});
            skLineSegment(sketch, "E538.MirrorCS", {"start": v(2215.22, 0) * mm, "end": v(2215.22, 8) * mm});
            skLineSegment(sketch, "E539.MirrorCS", {"start": v(2215.22, 8) * mm, "end": v(2210.22, 8) * mm});
            skLineSegment(sketch, "E540", {"start": v(2362.88, 97.17) * mm, "end": v(2362.88, 0) * mm, "construction": true});
            skLineSegment(sketch, "E541", {"start": v(2292.52, 0) * mm, "end": v(2433.3, 0) * mm, "construction": true});
            skLineSegment(sketch, "E542.bottom", {"start": v(2338.38, 69.6) * mm, "end": v(2362.88, 69.6) * mm});
            skLineSegment(sketch, "E542.top", {"start": v(2343.38, 61.6) * mm, "end": v(2350.38, 61.6) * mm});
            skLineSegment(sketch, "E542.left", {"start": v(2338.38, 69.6) * mm, "end": v(2338.38, 67.6) * mm});
            skLineSegment(sketch, "E543.bottom", {"start": v(2323.92, 0) * mm, "end": v(2401.83, 0) * mm});
            skLineSegment(sketch, "E543.left", {"start": v(2323.92, 0) * mm, "end": v(2323.92, 8) * mm});
            skLineSegment(sketch, "E544.left", {"start": v(2350.38, 61.6) * mm, "end": v(2350.38, 54.8) * mm});
            skLineSegment(sketch, "E545", {"start": v(2328.92, 8) * mm, "end": v(2338.38, 61.6) * mm});
            skLineSegment(sketch, "E546", {"start": v(2323.92, 8) * mm, "end": v(2328.92, 8) * mm});
            skLineSegment(sketch, "E547.trimOffspring", {"start": v(2336.42, 8) * mm, "end": v(2341.84, 49.8) * mm});
            skLineSegment(sketch, "E548.bottom", {"start": v(2332.88, 70.6) * mm, "end": v(2337.88, 70.6) * mm});
            skLineSegment(sketch, "E548.top", {"start": v(2332.88, 61.6) * mm, "end": v(2338.38, 61.6) * mm});
            skLineSegment(sketch, "E548.left", {"start": v(2332.88, 70.6) * mm, "end": v(2332.88, 61.6) * mm});
            skLineSegment(sketch, "E549.right", {"start": v(2337.88, 70.6) * mm, "end": v(2337.88, 67.6) * mm});
            skLineSegment(sketch, "E550", {"start": v(2337.88, 67.6) * mm, "end": v(2338.38, 67.6) * mm});
            skLineSegment(sketch, "E551", {"start": v(2355.38, 61.6) * mm, "end": v(2355.38, 54.8) * mm});
            skLineSegment(sketch, "E552.trimOffspring", {"start": v(2336.42, 8) * mm, "end": v(2350.38, 8) * mm});
            skLineSegment(sketch, "E553.trimOffspring", {"start": v(2355.38, 49.8) * mm, "end": v(2355.38, 8) * mm});
            skLineSegment(sketch, "E554.trimOffspring", {"start": v(2350.38, 49.8) * mm, "end": v(2350.38, 8) * mm});
            skLineSegment(sketch, "E555.trimOffspring", {"start": v(2342.5, 54.8) * mm, "end": v(2343.38, 61.6) * mm});
            skLineSegment(sketch, "E556", {"start": v(2428.7, 61.6) * mm, "end": v(2290.31, 61.6) * mm, "construction": true});
            skLineSegment(sketch, "E557", {"start": v(2342.5, 54.8) * mm, "end": v(2362.88, 54.8) * mm});
            skLineSegment(sketch, "E558", {"start": v(2355.38, 61.6) * mm, "end": v(2362.88, 61.6) * mm});
            skLineSegment(sketch, "E559", {"start": v(2341.84, 49.8) * mm, "end": v(2362.88, 49.8) * mm});
            skLineSegment(sketch, "E560.MirrorCS", {"start": v(2387.38, 69.6) * mm, "end": v(2362.88, 69.6) * mm});
            skLineSegment(sketch, "E561.MirrorCS", {"start": v(2387.38, 69.6) * mm, "end": v(2387.38, 67.6) * mm});
            skLineSegment(sketch, "E562.MirrorCS", {"start": v(2387.88, 67.6) * mm, "end": v(2387.38, 67.6) * mm});
            skLineSegment(sketch, "E563.MirrorCS", {"start": v(2387.88, 70.6) * mm, "end": v(2387.88, 67.6) * mm});
            skLineSegment(sketch, "E564.MirrorCS", {"start": v(2392.88, 70.6) * mm, "end": v(2387.88, 70.6) * mm});
            skLineSegment(sketch, "E565.MirrorCS", {"start": v(2392.88, 70.6) * mm, "end": v(2392.88, 61.6) * mm});
            skLineSegment(sketch, "E566.MirrorCS", {"start": v(2392.88, 61.6) * mm, "end": v(2387.38, 61.6) * mm});
            skLineSegment(sketch, "E567.MirrorCS", {"start": v(2382.38, 61.6) * mm, "end": v(2375.38, 61.6) * mm});
            skLineSegment(sketch, "E568.MirrorCS", {"start": v(2370.38, 61.6) * mm, "end": v(2362.88, 61.6) * mm});
            skLineSegment(sketch, "E569.MirrorCS", {"start": v(2370.38, 61.6) * mm, "end": v(2370.38, 54.8) * mm});
            skLineSegment(sketch, "E570.MirrorCS", {"start": v(2375.38, 61.6) * mm, "end": v(2375.38, 54.8) * mm});
            skLineSegment(sketch, "E571.MirrorCS", {"start": v(2383.26, 54.8) * mm, "end": v(2382.38, 61.6) * mm});
            skLineSegment(sketch, "E572.MirrorCS", {"start": v(2396.83, 8) * mm, "end": v(2387.38, 61.6) * mm});
            skLineSegment(sketch, "E573.MirrorCS", {"start": v(2383.26, 54.8) * mm, "end": v(2362.88, 54.8) * mm});
            skLineSegment(sketch, "E574.MirrorCS", {"start": v(2383.9, 49.8) * mm, "end": v(2362.88, 49.8) * mm});
            skLineSegment(sketch, "E575.MirrorCS", {"start": v(2370.38, 49.8) * mm, "end": v(2370.38, 8) * mm});
            skLineSegment(sketch, "E576.MirrorCS", {"start": v(2375.38, 49.8) * mm, "end": v(2375.38, 8) * mm});
            skLineSegment(sketch, "E577.MirrorCS", {"start": v(2389.33, 8) * mm, "end": v(2375.38, 8) * mm});
            skLineSegment(sketch, "E578.MirrorCS", {"start": v(2389.33, 8) * mm, "end": v(2383.9, 49.8) * mm});
            skPoint(sketch, "E579.orphan", {"position": v(2336.3, 49.8) * mm});
            skPoint(sketch, "E580.orphan", {"position": v(2389.46, 49.8) * mm});
            skLineSegment(sketch, "E581", {"start": v(2355.38, 8) * mm, "end": v(2362.88, 8) * mm});
            skLineSegment(sketch, "E582.MirrorCS", {"start": v(2370.38, 8) * mm, "end": v(2362.88, 8) * mm});
            skLineSegment(sketch, "E583.MirrorCS", {"start": v(2401.83, 0) * mm, "end": v(2401.83, 8) * mm});
            skLineSegment(sketch, "E584.MirrorCS", {"start": v(2401.83, 8) * mm, "end": v(2396.83, 8) * mm});
            skLineSegment(sketch, "E585", {"start": v(2525.47, 80.3) * mm, "end": v(2525.47, 0) * mm, "construction": true});
            skLineSegment(sketch, "E586", {"start": v(2448.36, 0) * mm, "end": v(2589.14, 0) * mm, "construction": true});
            skLineSegment(sketch, "E587.bottom", {"start": v(2500.97, 68.5) * mm, "end": v(2525.47, 68.5) * mm});
            skLineSegment(sketch, "E587.top", {"start": v(2505.97, 60.5) * mm, "end": v(2512.97, 60.5) * mm});
            skLineSegment(sketch, "E587.left", {"start": v(2500.97, 68.5) * mm, "end": v(2500.97, 66.5) * mm});
            skLineSegment(sketch, "E588.bottom", {"start": v(2486.71, 0) * mm, "end": v(2564.23, 0) * mm});
            skLineSegment(sketch, "E588.left", {"start": v(2486.71, 0) * mm, "end": v(2486.71, 8) * mm});
            skLineSegment(sketch, "E589.left", {"start": v(2512.97, 60.5) * mm, "end": v(2512.97, 54.8) * mm});
            skLineSegment(sketch, "E590", {"start": v(2491.71, 8) * mm, "end": v(2500.97, 60.5) * mm});
            skLineSegment(sketch, "E591", {"start": v(2486.71, 8) * mm, "end": v(2491.71, 8) * mm});
            skLineSegment(sketch, "E592.trimOffspring", {"start": v(2499.21, 8) * mm, "end": v(2504.6, 49.8) * mm});
            skLineSegment(sketch, "E593.bottom", {"start": v(2495.47, 69.5) * mm, "end": v(2500.47, 69.5) * mm});
            skLineSegment(sketch, "E593.top", {"start": v(2495.47, 60.5) * mm, "end": v(2500.97, 60.5) * mm});
            skLineSegment(sketch, "E593.left", {"start": v(2495.47, 69.5) * mm, "end": v(2495.47, 60.5) * mm});
            skLineSegment(sketch, "E594.right", {"start": v(2500.47, 69.5) * mm, "end": v(2500.47, 66.5) * mm});
            skLineSegment(sketch, "E595", {"start": v(2500.47, 66.5) * mm, "end": v(2500.97, 66.5) * mm});
            skLineSegment(sketch, "E596", {"start": v(2517.97, 60.5) * mm, "end": v(2517.97, 54.8) * mm});
            skLineSegment(sketch, "E597.trimOffspring", {"start": v(2499.21, 8) * mm, "end": v(2512.97, 8) * mm});
            skLineSegment(sketch, "E598.trimOffspring", {"start": v(2517.97, 49.8) * mm, "end": v(2517.97, 8) * mm});
            skLineSegment(sketch, "E599.trimOffspring", {"start": v(2512.97, 49.8) * mm, "end": v(2512.97, 8) * mm});
            skLineSegment(sketch, "E600.trimOffspring", {"start": v(2505.23, 54.8) * mm, "end": v(2505.97, 60.5) * mm});
            skLineSegment(sketch, "E601", {"start": v(2584.53, 60.5) * mm, "end": v(2446.15, 60.5) * mm, "construction": true});
            skLineSegment(sketch, "E602", {"start": v(2505.23, 54.8) * mm, "end": v(2525.47, 54.8) * mm});
            skLineSegment(sketch, "E603", {"start": v(2517.97, 60.5) * mm, "end": v(2525.47, 60.5) * mm});
            skLineSegment(sketch, "E604", {"start": v(2504.6, 49.8) * mm, "end": v(2525.47, 49.8) * mm});
            skLineSegment(sketch, "E605.MirrorCS", {"start": v(2549.97, 68.5) * mm, "end": v(2525.47, 68.5) * mm});
            skLineSegment(sketch, "E606.MirrorCS", {"start": v(2549.97, 68.5) * mm, "end": v(2549.97, 66.5) * mm});
            skLineSegment(sketch, "E607.MirrorCS", {"start": v(2550.47, 66.5) * mm, "end": v(2549.97, 66.5) * mm});
            skLineSegment(sketch, "E608.MirrorCS", {"start": v(2550.47, 69.5) * mm, "end": v(2550.47, 66.5) * mm});
            skLineSegment(sketch, "E609.MirrorCS", {"start": v(2555.47, 69.5) * mm, "end": v(2550.47, 69.5) * mm});
            skLineSegment(sketch, "E610.MirrorCS", {"start": v(2555.47, 69.5) * mm, "end": v(2555.47, 60.5) * mm});
            skLineSegment(sketch, "E611.MirrorCS", {"start": v(2555.47, 60.5) * mm, "end": v(2549.97, 60.5) * mm});
            skLineSegment(sketch, "E612.MirrorCS", {"start": v(2544.97, 60.5) * mm, "end": v(2537.97, 60.5) * mm});
            skLineSegment(sketch, "E613.MirrorCS", {"start": v(2532.97, 60.5) * mm, "end": v(2525.47, 60.5) * mm});
            skLineSegment(sketch, "E614.MirrorCS", {"start": v(2532.97, 60.5) * mm, "end": v(2532.97, 54.8) * mm});
            skLineSegment(sketch, "E615.MirrorCS", {"start": v(2537.97, 60.5) * mm, "end": v(2537.97, 54.8) * mm});
            skLineSegment(sketch, "E616.MirrorCS", {"start": v(2545.7, 54.8) * mm, "end": v(2544.97, 60.5) * mm});
            skLineSegment(sketch, "E617.MirrorCS", {"start": v(2559.23, 8) * mm, "end": v(2549.97, 60.5) * mm});
            skLineSegment(sketch, "E618.MirrorCS", {"start": v(2545.7, 54.8) * mm, "end": v(2525.47, 54.8) * mm});
            skLineSegment(sketch, "E619.MirrorCS", {"start": v(2546.35, 49.8) * mm, "end": v(2525.47, 49.8) * mm});
            skLineSegment(sketch, "E620.MirrorCS", {"start": v(2532.97, 49.8) * mm, "end": v(2532.97, 8) * mm});
            skLineSegment(sketch, "E621.MirrorCS", {"start": v(2537.97, 49.8) * mm, "end": v(2537.97, 8) * mm});
            skLineSegment(sketch, "E622.MirrorCS", {"start": v(2551.73, 8) * mm, "end": v(2537.97, 8) * mm});
            skLineSegment(sketch, "E623.MirrorCS", {"start": v(2551.73, 8) * mm, "end": v(2546.35, 49.8) * mm});
            skPoint(sketch, "E624.orphan", {"position": v(2499.08, 49.8) * mm});
            skPoint(sketch, "E625.orphan", {"position": v(2551.85, 49.8) * mm});
            skLineSegment(sketch, "E626", {"start": v(2517.97, 8) * mm, "end": v(2525.47, 8) * mm});
            skLineSegment(sketch, "E627.MirrorCS", {"start": v(2532.97, 8) * mm, "end": v(2525.47, 8) * mm});
            skLineSegment(sketch, "E628.MirrorCS", {"start": v(2564.23, 0) * mm, "end": v(2564.23, 8) * mm});
            skLineSegment(sketch, "E629.MirrorCS", {"start": v(2564.23, 8) * mm, "end": v(2559.23, 8) * mm});
            skLineSegment(sketch, "E630", {"start": v(2711.58, 84.04) * mm, "end": v(2711.58, 0) * mm, "construction": true});
            skLineSegment(sketch, "E631", {"start": v(2643.49, 0) * mm, "end": v(2784.27, 0) * mm, "construction": true});
            skLineSegment(sketch, "E632.bottom", {"start": v(2687.08, 64.1) * mm, "end": v(2711.58, 64.1) * mm});
            skLineSegment(sketch, "E632.top", {"start": v(2692.08, 56.1) * mm, "end": v(2699.08, 56.1) * mm});
            skLineSegment(sketch, "E632.left", {"start": v(2687.08, 64.1) * mm, "end": v(2687.08, 62.1) * mm});
            skLineSegment(sketch, "E633.bottom", {"start": v(2673.6, 0) * mm, "end": v(2749.56, 0) * mm});
            skLineSegment(sketch, "E633.left", {"start": v(2673.6, 0) * mm, "end": v(2673.6, 8) * mm});
            skLineSegment(sketch, "E634.left", {"start": v(2699.08, 56.1) * mm, "end": v(2699.08, 54.8) * mm});
            skLineSegment(sketch, "E635", {"start": v(2678.6, 8) * mm, "end": v(2687.08, 56.1) * mm});
            skLineSegment(sketch, "E636", {"start": v(2673.6, 8) * mm, "end": v(2678.6, 8) * mm});
            skLineSegment(sketch, "E637.trimOffspring", {"start": v(2686.1, 8) * mm, "end": v(2691.3, 49.8) * mm});
            skLineSegment(sketch, "E638.bottom", {"start": v(2681.58, 65.1) * mm, "end": v(2686.58, 65.1) * mm});
            skLineSegment(sketch, "E638.top", {"start": v(2681.58, 56.1) * mm, "end": v(2687.08, 56.1) * mm});
            skLineSegment(sketch, "E638.left", {"start": v(2681.58, 65.1) * mm, "end": v(2681.58, 56.1) * mm});
            skLineSegment(sketch, "E639.right", {"start": v(2686.58, 65.1) * mm, "end": v(2686.58, 62.1) * mm});
            skLineSegment(sketch, "E640", {"start": v(2686.58, 62.1) * mm, "end": v(2687.08, 62.1) * mm});
            skLineSegment(sketch, "E641", {"start": v(2704.08, 56.1) * mm, "end": v(2704.08, 54.8) * mm});
            skLineSegment(sketch, "E642.trimOffspring", {"start": v(2686.1, 8) * mm, "end": v(2699.08, 8) * mm});
            skLineSegment(sketch, "E643.trimOffspring", {"start": v(2704.08, 49.8) * mm, "end": v(2704.08, 8) * mm});
            skLineSegment(sketch, "E644.trimOffspring", {"start": v(2699.08, 49.8) * mm, "end": v(2699.08, 8) * mm});
            skLineSegment(sketch, "E645.trimOffspring", {"start": v(2691.91, 54.8) * mm, "end": v(2692.08, 56.1) * mm});
            skLineSegment(sketch, "E646", {"start": v(2779.66, 56.1) * mm, "end": v(2641.28, 56.1) * mm, "construction": true});
            skLineSegment(sketch, "E647", {"start": v(2691.91, 54.8) * mm, "end": v(2711.58, 54.8) * mm});
            skLineSegment(sketch, "E648", {"start": v(2704.08, 56.1) * mm, "end": v(2711.58, 56.1) * mm});
            skLineSegment(sketch, "E649", {"start": v(2691.3, 49.8) * mm, "end": v(2711.58, 49.8) * mm});
            skLineSegment(sketch, "E650.MirrorCS", {"start": v(2736.08, 64.1) * mm, "end": v(2711.58, 64.1) * mm});
            skLineSegment(sketch, "E651.MirrorCS", {"start": v(2736.08, 64.1) * mm, "end": v(2736.08, 62.1) * mm});
            skLineSegment(sketch, "E652.MirrorCS", {"start": v(2736.58, 62.1) * mm, "end": v(2736.08, 62.1) * mm});
            skLineSegment(sketch, "E653.MirrorCS", {"start": v(2736.58, 65.1) * mm, "end": v(2736.58, 62.1) * mm});
            skLineSegment(sketch, "E654.MirrorCS", {"start": v(2741.58, 65.1) * mm, "end": v(2736.58, 65.1) * mm});
            skLineSegment(sketch, "E655.MirrorCS", {"start": v(2741.58, 65.1) * mm, "end": v(2741.58, 56.1) * mm});
            skLineSegment(sketch, "E656.MirrorCS", {"start": v(2741.58, 56.1) * mm, "end": v(2736.08, 56.1) * mm});
            skLineSegment(sketch, "E657.MirrorCS", {"start": v(2731.08, 56.1) * mm, "end": v(2724.08, 56.1) * mm});
            skLineSegment(sketch, "E658.MirrorCS", {"start": v(2719.08, 56.1) * mm, "end": v(2711.58, 56.1) * mm});
            skLineSegment(sketch, "E659.MirrorCS", {"start": v(2719.08, 56.1) * mm, "end": v(2719.08, 54.8) * mm});
            skLineSegment(sketch, "E660.MirrorCS", {"start": v(2724.08, 56.1) * mm, "end": v(2724.08, 54.8) * mm});
            skLineSegment(sketch, "E661.MirrorCS", {"start": v(2731.24, 54.8) * mm, "end": v(2731.08, 56.1) * mm});
            skLineSegment(sketch, "E662.MirrorCS", {"start": v(2744.56, 8) * mm, "end": v(2736.08, 56.1) * mm});
            skLineSegment(sketch, "E663.MirrorCS", {"start": v(2731.24, 54.8) * mm, "end": v(2711.58, 54.8) * mm});
            skLineSegment(sketch, "E664.MirrorCS", {"start": v(2731.86, 49.8) * mm, "end": v(2711.58, 49.8) * mm});
            skLineSegment(sketch, "E665.MirrorCS", {"start": v(2719.08, 49.8) * mm, "end": v(2719.08, 8) * mm});
            skLineSegment(sketch, "E666.MirrorCS", {"start": v(2724.08, 49.8) * mm, "end": v(2724.08, 8) * mm});
            skLineSegment(sketch, "E667.MirrorCS", {"start": v(2737.06, 8) * mm, "end": v(2724.08, 8) * mm});
            skLineSegment(sketch, "E668.MirrorCS", {"start": v(2737.06, 8) * mm, "end": v(2731.86, 49.8) * mm});
            skPoint(sketch, "E669.orphan", {"position": v(2685.97, 49.8) * mm});
            skPoint(sketch, "E670.orphan", {"position": v(2737.19, 49.8) * mm});
            skLineSegment(sketch, "E671", {"start": v(2704.08, 8) * mm, "end": v(2711.58, 8) * mm});
            skLineSegment(sketch, "E672.MirrorCS", {"start": v(2719.08, 8) * mm, "end": v(2711.58, 8) * mm});
            skLineSegment(sketch, "E673.MirrorCS", {"start": v(2749.56, 0) * mm, "end": v(2749.56, 8) * mm});
            skLineSegment(sketch, "E674.MirrorCS", {"start": v(2749.56, 8) * mm, "end": v(2744.56, 8) * mm});
            skLineSegment(sketch, "E675", {"start": v(2916.22, 108.04) * mm, "end": v(2916.22, 0) * mm, "construction": true});
            skLineSegment(sketch, "E676", {"start": v(2839.1, 0) * mm, "end": v(2979.88, 0) * mm, "construction": true});
            skLineSegment(sketch, "E677.bottom", {"start": v(2891.72, 59.7) * mm, "end": v(2916.22, 59.7) * mm});
            skLineSegment(sketch, "E677.top", {"start": v(2896.72, 51.7) * mm, "end": v(2903.72, 51.7) * mm});
            skLineSegment(sketch, "E677.left", {"start": v(2891.72, 59.7) * mm, "end": v(2891.72, 57.7) * mm});
            skLineSegment(sketch, "E678.bottom", {"start": v(2879.01, 0) * mm, "end": v(2953.42, 0) * mm});
            skLineSegment(sketch, "E678.left", {"start": v(2879.01, 0) * mm, "end": v(2879.01, 8) * mm});
            skLineSegment(sketch, "E679.left", {"start": v(2903.72, 51.7) * mm, "end": v(2903.72, 51.7) * mm});
            skLineSegment(sketch, "E680", {"start": v(2884.01, 8) * mm, "end": v(2891.72, 51.7) * mm});
            skLineSegment(sketch, "E681", {"start": v(2879.01, 8) * mm, "end": v(2884.01, 8) * mm});
            skLineSegment(sketch, "E682.trimOffspring", {"start": v(2891.51, 8) * mm, "end": v(2896.12, 46.7) * mm});
            skLineSegment(sketch, "E683.bottom", {"start": v(2886.22, 60.7) * mm, "end": v(2891.22, 60.7) * mm});
            skLineSegment(sketch, "E683.top", {"start": v(2886.22, 51.7) * mm, "end": v(2891.72, 51.7) * mm});
            skLineSegment(sketch, "E683.left", {"start": v(2886.22, 60.7) * mm, "end": v(2886.22, 51.7) * mm});
            skLineSegment(sketch, "E684.right", {"start": v(2891.22, 60.7) * mm, "end": v(2891.22, 57.7) * mm});
            skLineSegment(sketch, "E685", {"start": v(2891.22, 57.7) * mm, "end": v(2891.72, 57.7) * mm});
            skLineSegment(sketch, "E686", {"start": v(2908.72, 51.7) * mm, "end": v(2908.72, 51.7) * mm});
            skLineSegment(sketch, "E687.trimOffspring", {"start": v(2891.51, 8) * mm, "end": v(2903.72, 8) * mm});
            skLineSegment(sketch, "E688.trimOffspring", {"start": v(2908.72, 46.7) * mm, "end": v(2908.72, 8) * mm});
            skLineSegment(sketch, "E689.trimOffspring", {"start": v(2903.72, 46.7) * mm, "end": v(2903.72, 8) * mm});
            skLineSegment(sketch, "E690.trimOffspring", {"start": v(2896.72, 51.7) * mm, "end": v(2896.72, 51.7) * mm});
            skLineSegment(sketch, "E691", {"start": v(2975.28, 51.7) * mm, "end": v(2836.9, 51.7) * mm, "construction": true});
            skLineSegment(sketch, "E692", {"start": v(2896.72, 51.7) * mm, "end": v(2916.22, 51.7) * mm});
            skLineSegment(sketch, "E693", {"start": v(2908.72, 51.7) * mm, "end": v(2916.22, 51.7) * mm});
            skLineSegment(sketch, "E694", {"start": v(2896.12, 46.7) * mm, "end": v(2916.22, 46.7) * mm});
            skLineSegment(sketch, "E695.MirrorCS", {"start": v(2940.72, 59.7) * mm, "end": v(2916.22, 59.7) * mm});
            skLineSegment(sketch, "E696.MirrorCS", {"start": v(2940.72, 59.7) * mm, "end": v(2940.72, 57.7) * mm});
            skLineSegment(sketch, "E697.MirrorCS", {"start": v(2941.22, 57.7) * mm, "end": v(2940.72, 57.7) * mm});
            skLineSegment(sketch, "E698.MirrorCS", {"start": v(2941.22, 60.7) * mm, "end": v(2941.22, 57.7) * mm});
            skLineSegment(sketch, "E699.MirrorCS", {"start": v(2946.22, 60.7) * mm, "end": v(2941.22, 60.7) * mm});
            skLineSegment(sketch, "E700.MirrorCS", {"start": v(2946.22, 60.7) * mm, "end": v(2946.22, 51.7) * mm});
            skLineSegment(sketch, "E701.MirrorCS", {"start": v(2946.22, 51.7) * mm, "end": v(2940.72, 51.7) * mm});
            skLineSegment(sketch, "E702.MirrorCS", {"start": v(2935.72, 51.7) * mm, "end": v(2928.72, 51.7) * mm});
            skLineSegment(sketch, "E703.MirrorCS", {"start": v(2923.72, 51.7) * mm, "end": v(2916.22, 51.7) * mm});
            skLineSegment(sketch, "E704.MirrorCS", {"start": v(2923.72, 51.7) * mm, "end": v(2923.72, 51.7) * mm});
            skLineSegment(sketch, "E705.MirrorCS", {"start": v(2928.72, 51.7) * mm, "end": v(2928.72, 51.7) * mm});
            skLineSegment(sketch, "E706.MirrorCS", {"start": v(2935.72, 51.7) * mm, "end": v(2935.72, 51.7) * mm});
            skLineSegment(sketch, "E707.MirrorCS", {"start": v(2948.42, 8) * mm, "end": v(2940.72, 51.7) * mm});
            skLineSegment(sketch, "E708.MirrorCS", {"start": v(2935.72, 51.7) * mm, "end": v(2916.22, 51.7) * mm});
            skLineSegment(sketch, "E709.MirrorCS", {"start": v(2936.31, 46.7) * mm, "end": v(2916.22, 46.7) * mm});
            skLineSegment(sketch, "E710.MirrorCS", {"start": v(2923.72, 46.7) * mm, "end": v(2923.72, 8) * mm});
            skLineSegment(sketch, "E711.MirrorCS", {"start": v(2928.72, 46.7) * mm, "end": v(2928.72, 8) * mm});
            skLineSegment(sketch, "E712.MirrorCS", {"start": v(2940.92, 8) * mm, "end": v(2928.72, 8) * mm});
            skLineSegment(sketch, "E713.MirrorCS", {"start": v(2940.92, 8) * mm, "end": v(2936.31, 46.7) * mm});
            skPoint(sketch, "E714.orphan", {"position": v(2890.83, 46.7) * mm});
            skPoint(sketch, "E715.orphan", {"position": v(2941.6, 46.7) * mm});
            skLineSegment(sketch, "E716", {"start": v(2908.72, 8) * mm, "end": v(2916.22, 8) * mm});
            skLineSegment(sketch, "E717.MirrorCS", {"start": v(2923.72, 8) * mm, "end": v(2916.22, 8) * mm});
            skLineSegment(sketch, "E718.MirrorCS", {"start": v(2953.42, 0) * mm, "end": v(2953.42, 8) * mm});
            skLineSegment(sketch, "E719.MirrorCS", {"start": v(2953.42, 8) * mm, "end": v(2948.42, 8) * mm});
            skLineSegment(sketch, "E720", {"start": v(3102.32, 111.78) * mm, "end": v(3102.32, 0) * mm, "construction": true});
            skLineSegment(sketch, "E721", {"start": v(3034.24, 0) * mm, "end": v(3175.01, 0) * mm, "construction": true});
            skLineSegment(sketch, "E722.bottom", {"start": v(3077.82, 104.5) * mm, "end": v(3102.32, 104.5) * mm});
            skLineSegment(sketch, "E722.top", {"start": v(3082.82, 96.5) * mm, "end": v(3089.82, 96.5) * mm});
            skLineSegment(sketch, "E722.left", {"start": v(3077.82, 104.5) * mm, "end": v(3077.82, 102.5) * mm});
            skLineSegment(sketch, "E723.bottom", {"start": v(3057.22, 0) * mm, "end": v(3147.43, 0) * mm});
            skLineSegment(sketch, "E723.left", {"start": v(3057.22, 0) * mm, "end": v(3057.22, 8) * mm});
            skLineSegment(sketch, "E724.left", {"start": v(3089.82, 96.5) * mm, "end": v(3089.82, 54.8) * mm});
            skLineSegment(sketch, "E725", {"start": v(3062.22, 8) * mm, "end": v(3077.82, 96.5) * mm});
            skLineSegment(sketch, "E726", {"start": v(3057.22, 8) * mm, "end": v(3062.22, 8) * mm});
            skLineSegment(sketch, "E727.trimOffspring", {"start": v(3069.72, 8) * mm, "end": v(3075.9, 49.8) * mm});
            skLineSegment(sketch, "E728.bottom", {"start": v(3072.32, 105.5) * mm, "end": v(3077.32, 105.5) * mm});
            skLineSegment(sketch, "E728.top", {"start": v(3072.32, 96.5) * mm, "end": v(3077.82, 96.5) * mm});
            skLineSegment(sketch, "E728.left", {"start": v(3072.32, 105.5) * mm, "end": v(3072.32, 96.5) * mm});
            skLineSegment(sketch, "E729.right", {"start": v(3077.32, 105.5) * mm, "end": v(3077.32, 102.5) * mm});
            skLineSegment(sketch, "E730", {"start": v(3077.32, 102.5) * mm, "end": v(3077.82, 102.5) * mm});
            skLineSegment(sketch, "E731", {"start": v(3094.82, 96.5) * mm, "end": v(3094.82, 54.8) * mm});
            skLineSegment(sketch, "E732.trimOffspring", {"start": v(3069.72, 8) * mm, "end": v(3089.82, 8) * mm});
            skLineSegment(sketch, "E733.trimOffspring", {"start": v(3094.82, 49.8) * mm, "end": v(3094.82, 8) * mm});
            skLineSegment(sketch, "E734.trimOffspring", {"start": v(3089.82, 49.8) * mm, "end": v(3089.82, 8) * mm});
            skLineSegment(sketch, "E735.trimOffspring", {"start": v(3076.65, 54.8) * mm, "end": v(3082.82, 96.5) * mm});
            skLineSegment(sketch, "E736", {"start": v(3170.41, 96.5) * mm, "end": v(3032.03, 96.5) * mm, "construction": true});
            skLineSegment(sketch, "E737", {"start": v(3076.65, 54.8) * mm, "end": v(3102.32, 54.8) * mm});
            skLineSegment(sketch, "E738", {"start": v(3094.82, 96.5) * mm, "end": v(3102.32, 96.5) * mm});
            skLineSegment(sketch, "E739", {"start": v(3075.9, 49.8) * mm, "end": v(3102.32, 49.8) * mm});
            skLineSegment(sketch, "E740.MirrorCS", {"start": v(3126.82, 104.5) * mm, "end": v(3102.32, 104.5) * mm});
            skLineSegment(sketch, "E741.MirrorCS", {"start": v(3126.82, 104.5) * mm, "end": v(3126.82, 102.5) * mm});
            skLineSegment(sketch, "E742.MirrorCS", {"start": v(3127.32, 102.5) * mm, "end": v(3126.82, 102.5) * mm});
            skLineSegment(sketch, "E743.MirrorCS", {"start": v(3127.32, 105.5) * mm, "end": v(3127.32, 102.5) * mm});
            skLineSegment(sketch, "E744.MirrorCS", {"start": v(3132.32, 105.5) * mm, "end": v(3127.32, 105.5) * mm});
            skLineSegment(sketch, "E745.MirrorCS", {"start": v(3132.32, 105.5) * mm, "end": v(3132.32, 96.5) * mm});
            skLineSegment(sketch, "E746.MirrorCS", {"start": v(3132.32, 96.5) * mm, "end": v(3126.82, 96.5) * mm});
            skLineSegment(sketch, "E747.MirrorCS", {"start": v(3121.82, 96.5) * mm, "end": v(3114.82, 96.5) * mm});
            skLineSegment(sketch, "E748.MirrorCS", {"start": v(3109.82, 96.5) * mm, "end": v(3102.32, 96.5) * mm});
            skLineSegment(sketch, "E749.MirrorCS", {"start": v(3109.82, 96.5) * mm, "end": v(3109.82, 54.8) * mm});
            skLineSegment(sketch, "E750.MirrorCS", {"start": v(3114.82, 96.5) * mm, "end": v(3114.82, 54.8) * mm});
            skLineSegment(sketch, "E751.MirrorCS", {"start": v(3128, 54.8) * mm, "end": v(3121.82, 96.5) * mm});
            skLineSegment(sketch, "E752.MirrorCS", {"start": v(3142.43, 8) * mm, "end": v(3126.82, 96.5) * mm});
            skLineSegment(sketch, "E753.MirrorCS", {"start": v(3128, 54.8) * mm, "end": v(3102.32, 54.8) * mm});
            skLineSegment(sketch, "E754.MirrorCS", {"start": v(3128.74, 49.8) * mm, "end": v(3102.32, 49.8) * mm});
            skLineSegment(sketch, "E755.MirrorCS", {"start": v(3109.82, 49.8) * mm, "end": v(3109.82, 8) * mm});
            skLineSegment(sketch, "E756.MirrorCS", {"start": v(3114.82, 49.8) * mm, "end": v(3114.82, 8) * mm});
            skLineSegment(sketch, "E757.MirrorCS", {"start": v(3134.93, 8) * mm, "end": v(3114.82, 8) * mm});
            skLineSegment(sketch, "E758.MirrorCS", {"start": v(3134.93, 8) * mm, "end": v(3128.74, 49.8) * mm});
            skPoint(sketch, "E759.orphan", {"position": v(3069.59, 49.8) * mm});
            skPoint(sketch, "E760.orphan", {"position": v(3135.06, 49.8) * mm});
            skLineSegment(sketch, "E761", {"start": v(3094.82, 8) * mm, "end": v(3102.32, 8) * mm});
            skLineSegment(sketch, "E762.MirrorCS", {"start": v(3109.82, 8) * mm, "end": v(3102.32, 8) * mm});
            skLineSegment(sketch, "E763.MirrorCS", {"start": v(3147.43, 0) * mm, "end": v(3147.43, 8) * mm});
            skLineSegment(sketch, "E764.MirrorCS", {"start": v(3147.43, 8) * mm, "end": v(3142.43, 8) * mm});
            skSolve(sketch);
        }
        {
            var Q0;
            Q0=qCreatedBy(makeId("Right.planeOp"),FACE);
            var sketch = newSketch(context, id + "F1", { "sketchPlane" : qUnion([Q0])});
            skLineSegment(sketch, "E765", {"start": v(-94.52, 0) * mm, "end": v(-94.52, -2.28) * mm, "construction": true});
            skLineSegment(sketch, "E766", {"start": v(-181.07, 0) * mm, "end": v(6661.25, 0) * mm, "construction": true});
            skLineSegment(sketch, "E767.bottom", {"start": v(-119.02, 58.7) * mm, "end": v(-94.52, 58.7) * mm});
            skLineSegment(sketch, "E767.top", {"start": v(-114.02, 50.7) * mm, "end": v(-107.02, 50.7) * mm});
            skLineSegment(sketch, "E767.left", {"start": v(-119.02, 58.7) * mm, "end": v(-119.02, 56.7) * mm});
            skLineSegment(sketch, "E768.bottom", {"start": v(-134.55, 0) * mm, "end": v(-54.49, 0) * mm});
            skLineSegment(sketch, "E768.left", {"start": v(-134.55, 0) * mm, "end": v(-134.55, 8) * mm});
            skLineSegment(sketch, "E769", {"start": v(-126.55, 8) * mm, "end": v(-119.02, 50.7) * mm});
            skLineSegment(sketch, "E770", {"start": v(-134.55, 8) * mm, "end": v(-126.55, 8) * mm});
            skLineSegment(sketch, "E771.bottom", {"start": v(-124.52, 59.7) * mm, "end": v(-119.52, 59.7) * mm});
            skLineSegment(sketch, "E771.top", {"start": v(-124.52, 50.7) * mm, "end": v(-119.02, 50.7) * mm});
            skLineSegment(sketch, "E771.left", {"start": v(-124.52, 59.7) * mm, "end": v(-124.52, 50.7) * mm});
            skLineSegment(sketch, "E772.right", {"start": v(-119.52, 59.7) * mm, "end": v(-119.52, 56.7) * mm});
            skLineSegment(sketch, "E773", {"start": v(-119.52, 56.7) * mm, "end": v(-119.02, 56.7) * mm});
            skLineSegment(sketch, "E774.trimOffspring", {"start": v(-119.05, 8) * mm, "end": v(-107.02, 8) * mm});
            skLineSegment(sketch, "E775", {"start": v(-102.02, 50.7) * mm, "end": v(-94.52, 50.7) * mm});
            skLineSegment(sketch, "E776.MirrorCS", {"start": v(-70.02, 58.7) * mm, "end": v(-94.52, 58.7) * mm});
            skLineSegment(sketch, "E777.MirrorCS", {"start": v(-70.02, 58.7) * mm, "end": v(-70.02, 56.7) * mm});
            skLineSegment(sketch, "E778.MirrorCS", {"start": v(-69.52, 56.7) * mm, "end": v(-70.02, 56.7) * mm});
            skLineSegment(sketch, "E779.MirrorCS", {"start": v(-69.52, 59.7) * mm, "end": v(-69.52, 56.7) * mm});
            skLineSegment(sketch, "E780.MirrorCS", {"start": v(-64.52, 59.7) * mm, "end": v(-69.52, 59.7) * mm});
            skLineSegment(sketch, "E781.MirrorCS", {"start": v(-64.52, 59.7) * mm, "end": v(-64.52, 50.7) * mm});
            skLineSegment(sketch, "E782.MirrorCS", {"start": v(-64.52, 50.7) * mm, "end": v(-70.02, 50.7) * mm});
            skLineSegment(sketch, "E783.MirrorCS", {"start": v(-75.02, 50.7) * mm, "end": v(-82.02, 50.7) * mm});
            skLineSegment(sketch, "E784.MirrorCS", {"start": v(-87.02, 50.7) * mm, "end": v(-94.52, 50.7) * mm});
            skLineSegment(sketch, "E785.MirrorCS", {"start": v(-62.49, 8) * mm, "end": v(-70.02, 50.7) * mm});
            skLineSegment(sketch, "E786.MirrorCS", {"start": v(-69.99, 8) * mm, "end": v(-82.02, 8) * mm});
            skLineSegment(sketch, "E787", {"start": v(-102.02, 8) * mm, "end": v(-94.52, 8) * mm});
            skLineSegment(sketch, "E788.MirrorCS", {"start": v(-87.02, 8) * mm, "end": v(-94.52, 8) * mm});
            skLineSegment(sketch, "E789.MirrorCS", {"start": v(-54.49, 0) * mm, "end": v(-54.49, 8) * mm});
            skLineSegment(sketch, "E790.MirrorCS", {"start": v(-54.49, 8) * mm, "end": v(-62.49, 8) * mm});
            skLineSegment(sketch, "E791", {"start": v(-119.05, 8) * mm, "end": v(-114.02, 50.7) * mm});
            skLineSegment(sketch, "E792", {"start": v(-107.02, 50.7) * mm, "end": v(-107.02, 8) * mm});
            skLineSegment(sketch, "E793", {"start": v(-102.02, 8) * mm, "end": v(-102.02, 50.7) * mm});
            skLineSegment(sketch, "E794.MirrorCS", {"start": v(-69.99, 8) * mm, "end": v(-75.02, 50.7) * mm});
            skLineSegment(sketch, "E795.MirrorCS", {"start": v(-82.02, 50.7) * mm, "end": v(-82.02, 8) * mm});
            skLineSegment(sketch, "E796.MirrorCS", {"start": v(-87.02, 8) * mm, "end": v(-87.02, 50.7) * mm});
            skLineSegment(sketch, "E797", {"start": v(-156.63, 50.7) * mm, "end": v(-42.2, 50.7) * mm, "construction": true});
            skLineSegment(sketch, "E798", {"start": v(86.55, 61.18) * mm, "end": v(86.55, 0) * mm, "construction": true});
            skLineSegment(sketch, "E799", {"start": v(0, 0) * mm, "end": v(141.92, 0) * mm, "construction": true});
            skLineSegment(sketch, "E800.bottom", {"start": v(62.05, 58.6) * mm, "end": v(86.55, 58.6) * mm});
            skLineSegment(sketch, "E800.top", {"start": v(67.05, 50.6) * mm, "end": v(74.05, 50.6) * mm});
            skLineSegment(sketch, "E800.left", {"start": v(62.05, 58.6) * mm, "end": v(62.05, 56.6) * mm});
            skLineSegment(sketch, "E801.bottom", {"start": v(46.54, 0) * mm, "end": v(126.56, 0) * mm});
            skLineSegment(sketch, "E801.left", {"start": v(46.54, 0) * mm, "end": v(46.54, 8) * mm});
            skLineSegment(sketch, "E802", {"start": v(54.54, 8) * mm, "end": v(62.05, 50.6) * mm});
            skLineSegment(sketch, "E803", {"start": v(46.54, 8) * mm, "end": v(54.54, 8) * mm});
            skLineSegment(sketch, "E804.bottom", {"start": v(56.55, 59.6) * mm, "end": v(61.55, 59.6) * mm});
            skLineSegment(sketch, "E804.top", {"start": v(56.55, 50.6) * mm, "end": v(62.05, 50.6) * mm});
            skLineSegment(sketch, "E804.left", {"start": v(56.55, 59.6) * mm, "end": v(56.55, 50.6) * mm});
            skLineSegment(sketch, "E805.right", {"start": v(61.55, 59.6) * mm, "end": v(61.55, 56.6) * mm});
            skLineSegment(sketch, "E806", {"start": v(61.55, 56.6) * mm, "end": v(62.05, 56.6) * mm});
            skLineSegment(sketch, "E807.trimOffspring", {"start": v(62.04, 8) * mm, "end": v(74.05, 8) * mm});
            skLineSegment(sketch, "E808", {"start": v(79.05, 50.6) * mm, "end": v(86.55, 50.6) * mm});
            skLineSegment(sketch, "E809.MirrorCS", {"start": v(111.05, 58.6) * mm, "end": v(86.55, 58.6) * mm});
            skLineSegment(sketch, "E810.MirrorCS", {"start": v(111.05, 58.6) * mm, "end": v(111.05, 56.6) * mm});
            skLineSegment(sketch, "E811.MirrorCS", {"start": v(111.55, 56.6) * mm, "end": v(111.05, 56.6) * mm});
            skLineSegment(sketch, "E812.MirrorCS", {"start": v(111.55, 59.6) * mm, "end": v(111.55, 56.6) * mm});
            skLineSegment(sketch, "E813.MirrorCS", {"start": v(116.55, 59.6) * mm, "end": v(111.55, 59.6) * mm});
            skLineSegment(sketch, "E814.MirrorCS", {"start": v(116.55, 59.6) * mm, "end": v(116.55, 50.6) * mm});
            skLineSegment(sketch, "E815.MirrorCS", {"start": v(116.55, 50.6) * mm, "end": v(111.05, 50.6) * mm});
            skLineSegment(sketch, "E816.MirrorCS", {"start": v(106.05, 50.6) * mm, "end": v(99.05, 50.6) * mm});
            skLineSegment(sketch, "E817.MirrorCS", {"start": v(94.05, 50.6) * mm, "end": v(86.55, 50.6) * mm});
            skLineSegment(sketch, "E818.MirrorCS", {"start": v(118.56, 8) * mm, "end": v(111.05, 50.6) * mm});
            skLineSegment(sketch, "E819.MirrorCS", {"start": v(111.06, 8) * mm, "end": v(99.05, 8) * mm});
            skLineSegment(sketch, "E820", {"start": v(79.05, 8) * mm, "end": v(86.55, 8) * mm});
            skLineSegment(sketch, "E821.MirrorCS", {"start": v(94.05, 8) * mm, "end": v(86.55, 8) * mm});
            skLineSegment(sketch, "E822.MirrorCS", {"start": v(126.56, 0) * mm, "end": v(126.56, 8) * mm});
            skLineSegment(sketch, "E823.MirrorCS", {"start": v(126.56, 8) * mm, "end": v(118.56, 8) * mm});
            skLineSegment(sketch, "E824", {"start": v(62.04, 8) * mm, "end": v(67.05, 50.6) * mm});
            skLineSegment(sketch, "E825", {"start": v(74.05, 50.6) * mm, "end": v(74.05, 8) * mm});
            skLineSegment(sketch, "E826", {"start": v(79.05, 8) * mm, "end": v(79.05, 50.6) * mm});
            skLineSegment(sketch, "E827.MirrorCS", {"start": v(111.06, 8) * mm, "end": v(106.05, 50.6) * mm});
            skLineSegment(sketch, "E828.MirrorCS", {"start": v(99.05, 50.6) * mm, "end": v(99.05, 8) * mm});
            skLineSegment(sketch, "E829.MirrorCS", {"start": v(94.05, 8) * mm, "end": v(94.05, 50.6) * mm});
            skLineSegment(sketch, "E830", {"start": v(24.44, 50.6) * mm, "end": v(138.87, 50.6) * mm, "construction": true});
            skLineSegment(sketch, "E831", {"start": v(228.47, 26.25) * mm, "end": v(228.47, 0) * mm, "construction": true});
            skLineSegment(sketch, "E832", {"start": v(141.92, 0) * mm, "end": v(283.84, 0) * mm, "construction": true});
            skLineSegment(sketch, "E833.bottom", {"start": v(203.97, 54.1) * mm, "end": v(228.47, 54.1) * mm});
            skLineSegment(sketch, "E833.top", {"start": v(208.97, 46.1) * mm, "end": v(215.97, 46.1) * mm});
            skLineSegment(sketch, "E833.left", {"start": v(203.97, 54.1) * mm, "end": v(203.97, 52.1) * mm});
            skLineSegment(sketch, "E834.bottom", {"start": v(189.25, 0) * mm, "end": v(267.69, 0) * mm});
            skLineSegment(sketch, "E834.left", {"start": v(189.25, 0) * mm, "end": v(189.25, 8) * mm});
            skLineSegment(sketch, "E835", {"start": v(197.25, 8) * mm, "end": v(203.97, 46.1) * mm});
            skLineSegment(sketch, "E836", {"start": v(189.25, 8) * mm, "end": v(197.25, 8) * mm});
            skLineSegment(sketch, "E837.bottom", {"start": v(198.47, 55.1) * mm, "end": v(203.47, 55.1) * mm});
            skLineSegment(sketch, "E837.top", {"start": v(198.47, 46.1) * mm, "end": v(203.97, 46.1) * mm});
            skLineSegment(sketch, "E837.left", {"start": v(198.47, 55.1) * mm, "end": v(198.47, 46.1) * mm});
            skLineSegment(sketch, "E838.right", {"start": v(203.47, 55.1) * mm, "end": v(203.47, 52.1) * mm});
            skLineSegment(sketch, "E839", {"start": v(203.47, 52.1) * mm, "end": v(203.97, 52.1) * mm});
            skLineSegment(sketch, "E840.trimOffspring", {"start": v(204.75, 8) * mm, "end": v(215.97, 8) * mm});
            skLineSegment(sketch, "E841", {"start": v(220.97, 46.1) * mm, "end": v(228.47, 46.1) * mm});
            skLineSegment(sketch, "E842.MirrorCS", {"start": v(252.97, 54.1) * mm, "end": v(228.47, 54.1) * mm});
            skLineSegment(sketch, "E843.MirrorCS", {"start": v(252.97, 54.1) * mm, "end": v(252.97, 52.1) * mm});
            skLineSegment(sketch, "E844.MirrorCS", {"start": v(253.47, 52.1) * mm, "end": v(252.97, 52.1) * mm});
            skLineSegment(sketch, "E845.MirrorCS", {"start": v(253.47, 55.1) * mm, "end": v(253.47, 52.1) * mm});
            skLineSegment(sketch, "E846.MirrorCS", {"start": v(258.47, 55.1) * mm, "end": v(253.47, 55.1) * mm});
            skLineSegment(sketch, "E847.MirrorCS", {"start": v(258.47, 55.1) * mm, "end": v(258.47, 46.1) * mm});
            skLineSegment(sketch, "E848.MirrorCS", {"start": v(258.47, 46.1) * mm, "end": v(252.97, 46.1) * mm});
            skLineSegment(sketch, "E849.MirrorCS", {"start": v(247.97, 46.1) * mm, "end": v(240.97, 46.1) * mm});
            skLineSegment(sketch, "E850.MirrorCS", {"start": v(235.97, 46.1) * mm, "end": v(228.47, 46.1) * mm});
            skLineSegment(sketch, "E851.MirrorCS", {"start": v(259.69, 8) * mm, "end": v(252.97, 46.1) * mm});
            skLineSegment(sketch, "E852.MirrorCS", {"start": v(252.19, 8) * mm, "end": v(240.97, 8) * mm});
            skLineSegment(sketch, "E853", {"start": v(220.97, 8) * mm, "end": v(228.47, 8) * mm});
            skLineSegment(sketch, "E854.MirrorCS", {"start": v(235.97, 8) * mm, "end": v(228.47, 8) * mm});
            skLineSegment(sketch, "E855.MirrorCS", {"start": v(267.69, 0) * mm, "end": v(267.69, 8) * mm});
            skLineSegment(sketch, "E856.MirrorCS", {"start": v(267.69, 8) * mm, "end": v(259.69, 8) * mm});
            skLineSegment(sketch, "E857", {"start": v(204.75, 8) * mm, "end": v(208.97, 46.1) * mm});
            skLineSegment(sketch, "E858", {"start": v(215.97, 46.1) * mm, "end": v(215.97, 8) * mm});
            skLineSegment(sketch, "E859", {"start": v(220.97, 8) * mm, "end": v(220.97, 46.1) * mm});
            skLineSegment(sketch, "E860.MirrorCS", {"start": v(252.19, 8) * mm, "end": v(247.97, 46.1) * mm});
            skLineSegment(sketch, "E861.MirrorCS", {"start": v(240.97, 46.1) * mm, "end": v(240.97, 8) * mm});
            skLineSegment(sketch, "E862.MirrorCS", {"start": v(235.97, 8) * mm, "end": v(235.97, 46.1) * mm});
            skLineSegment(sketch, "E863", {"start": v(166.36, 46.1) * mm, "end": v(280.8, 46.1) * mm, "construction": true});
            skLineSegment(sketch, "E864", {"start": v(369.09, 38.67) * mm, "end": v(369.09, 0) * mm, "construction": true});
            skLineSegment(sketch, "E865", {"start": v(283.84, 0) * mm, "end": v(425.76, 0) * mm, "construction": true});
            skLineSegment(sketch, "E866.bottom", {"start": v(344.59, 49.7) * mm, "end": v(369.09, 49.7) * mm});
            skLineSegment(sketch, "E866.top", {"start": v(349.59, 41.7) * mm, "end": v(356.59, 41.7) * mm});
            skLineSegment(sketch, "E866.left", {"start": v(344.59, 49.7) * mm, "end": v(344.59, 47.7) * mm});
            skLineSegment(sketch, "E867.bottom", {"start": v(330.65, 0) * mm, "end": v(407.53, 0) * mm});
            skLineSegment(sketch, "E867.left", {"start": v(330.65, 0) * mm, "end": v(330.65, 8) * mm});
            skLineSegment(sketch, "E868", {"start": v(338.65, 8) * mm, "end": v(344.59, 41.7) * mm});
            skLineSegment(sketch, "E869", {"start": v(330.65, 8) * mm, "end": v(338.65, 8) * mm});
            skLineSegment(sketch, "E870.bottom", {"start": v(339.09, 50.7) * mm, "end": v(344.09, 50.7) * mm});
            skLineSegment(sketch, "E870.top", {"start": v(339.09, 41.7) * mm, "end": v(344.59, 41.7) * mm});
            skLineSegment(sketch, "E870.left", {"start": v(339.09, 50.7) * mm, "end": v(339.09, 41.7) * mm});
            skLineSegment(sketch, "E871.right", {"start": v(344.09, 50.7) * mm, "end": v(344.09, 47.7) * mm});
            skLineSegment(sketch, "E872", {"start": v(344.09, 47.7) * mm, "end": v(344.59, 47.7) * mm});
            skLineSegment(sketch, "E873.trimOffspring", {"start": v(346.15, 8) * mm, "end": v(356.59, 8) * mm});
            skLineSegment(sketch, "E874", {"start": v(361.59, 41.7) * mm, "end": v(369.09, 41.7) * mm});
            skLineSegment(sketch, "E875.MirrorCS", {"start": v(393.59, 49.7) * mm, "end": v(369.09, 49.7) * mm});
            skLineSegment(sketch, "E876.MirrorCS", {"start": v(393.59, 49.7) * mm, "end": v(393.59, 47.7) * mm});
            skLineSegment(sketch, "E877.MirrorCS", {"start": v(394.09, 47.7) * mm, "end": v(393.59, 47.7) * mm});
            skLineSegment(sketch, "E878.MirrorCS", {"start": v(394.09, 50.7) * mm, "end": v(394.09, 47.7) * mm});
            skLineSegment(sketch, "E879.MirrorCS", {"start": v(399.09, 50.7) * mm, "end": v(394.09, 50.7) * mm});
            skLineSegment(sketch, "E880.MirrorCS", {"start": v(399.09, 50.7) * mm, "end": v(399.09, 41.7) * mm});
            skLineSegment(sketch, "E881.MirrorCS", {"start": v(399.09, 41.7) * mm, "end": v(393.59, 41.7) * mm});
            skLineSegment(sketch, "E882.MirrorCS", {"start": v(388.59, 41.7) * mm, "end": v(381.59, 41.7) * mm});
            skLineSegment(sketch, "E883.MirrorCS", {"start": v(376.59, 41.7) * mm, "end": v(369.09, 41.7) * mm});
            skLineSegment(sketch, "E884.MirrorCS", {"start": v(399.53, 8) * mm, "end": v(393.59, 41.7) * mm});
            skLineSegment(sketch, "E885.MirrorCS", {"start": v(392.03, 8) * mm, "end": v(381.59, 8) * mm});
            skLineSegment(sketch, "E886", {"start": v(361.59, 8) * mm, "end": v(369.09, 8) * mm});
            skLineSegment(sketch, "E887.MirrorCS", {"start": v(376.59, 8) * mm, "end": v(369.09, 8) * mm});
            skLineSegment(sketch, "E888.MirrorCS", {"start": v(407.53, 0) * mm, "end": v(407.53, 8) * mm});
            skLineSegment(sketch, "E889.MirrorCS", {"start": v(407.53, 8) * mm, "end": v(399.53, 8) * mm});
            skLineSegment(sketch, "E890", {"start": v(346.15, 8) * mm, "end": v(349.59, 41.7) * mm});
            skLineSegment(sketch, "E891", {"start": v(356.59, 41.7) * mm, "end": v(356.59, 8) * mm});
            skLineSegment(sketch, "E892", {"start": v(361.59, 8) * mm, "end": v(361.59, 41.7) * mm});
            skLineSegment(sketch, "E893.MirrorCS", {"start": v(392.03, 8) * mm, "end": v(388.59, 41.7) * mm});
            skLineSegment(sketch, "E894.MirrorCS", {"start": v(381.59, 41.7) * mm, "end": v(381.59, 8) * mm});
            skLineSegment(sketch, "E895.MirrorCS", {"start": v(376.59, 8) * mm, "end": v(376.59, 41.7) * mm});
            skLineSegment(sketch, "E896", {"start": v(308.28, 41.7) * mm, "end": v(422.72, 41.7) * mm, "construction": true});
            skLineSegment(sketch, "E897", {"start": v(512.31, 62.71) * mm, "end": v(512.31, 0) * mm, "construction": true});
            skLineSegment(sketch, "E898", {"start": v(425.76, 0) * mm, "end": v(567.68, 0) * mm, "construction": true});
            skLineSegment(sketch, "E899.bottom", {"start": v(487.81, 48.6) * mm, "end": v(512.31, 48.6) * mm});
            skLineSegment(sketch, "E899.top", {"start": v(492.81, 40.6) * mm, "end": v(499.81, 40.6) * mm});
            skLineSegment(sketch, "E899.left", {"start": v(487.81, 48.6) * mm, "end": v(487.81, 46.6) * mm});
            skLineSegment(sketch, "E900.bottom", {"start": v(474.06, 0) * mm, "end": v(550.56, 0) * mm});
            skLineSegment(sketch, "E900.left", {"start": v(474.06, 0) * mm, "end": v(474.06, 8) * mm});
            skLineSegment(sketch, "E901", {"start": v(482.06, 8) * mm, "end": v(487.81, 40.6) * mm});
            skLineSegment(sketch, "E902", {"start": v(474.06, 8) * mm, "end": v(482.06, 8) * mm});
            skLineSegment(sketch, "E903.bottom", {"start": v(482.31, 49.6) * mm, "end": v(487.31, 49.6) * mm});
            skLineSegment(sketch, "E903.top", {"start": v(482.31, 40.6) * mm, "end": v(487.81, 40.6) * mm});
            skLineSegment(sketch, "E903.left", {"start": v(482.31, 49.6) * mm, "end": v(482.31, 40.6) * mm});
            skLineSegment(sketch, "E904.right", {"start": v(487.31, 49.6) * mm, "end": v(487.31, 46.6) * mm});
            skLineSegment(sketch, "E905", {"start": v(487.31, 46.6) * mm, "end": v(487.81, 46.6) * mm});
            skLineSegment(sketch, "E906.trimOffspring", {"start": v(489.56, 8) * mm, "end": v(499.81, 8) * mm});
            skLineSegment(sketch, "E907", {"start": v(504.81, 40.6) * mm, "end": v(512.31, 40.6) * mm});
            skLineSegment(sketch, "E908.MirrorCS", {"start": v(536.81, 48.6) * mm, "end": v(512.31, 48.6) * mm});
            skLineSegment(sketch, "E909.MirrorCS", {"start": v(536.81, 48.6) * mm, "end": v(536.81, 46.6) * mm});
            skLineSegment(sketch, "E910.MirrorCS", {"start": v(537.31, 46.6) * mm, "end": v(536.81, 46.6) * mm});
            skLineSegment(sketch, "E911.MirrorCS", {"start": v(537.31, 49.6) * mm, "end": v(537.31, 46.6) * mm});
            skLineSegment(sketch, "E912.MirrorCS", {"start": v(542.31, 49.6) * mm, "end": v(537.31, 49.6) * mm});
            skLineSegment(sketch, "E913.MirrorCS", {"start": v(542.31, 49.6) * mm, "end": v(542.31, 40.6) * mm});
            skLineSegment(sketch, "E914.MirrorCS", {"start": v(542.31, 40.6) * mm, "end": v(536.81, 40.6) * mm});
            skLineSegment(sketch, "E915.MirrorCS", {"start": v(531.81, 40.6) * mm, "end": v(524.81, 40.6) * mm});
            skLineSegment(sketch, "E916.MirrorCS", {"start": v(519.81, 40.6) * mm, "end": v(512.31, 40.6) * mm});
            skLineSegment(sketch, "E917.MirrorCS", {"start": v(542.56, 8) * mm, "end": v(536.81, 40.6) * mm});
            skLineSegment(sketch, "E918.MirrorCS", {"start": v(535.06, 8) * mm, "end": v(524.81, 8) * mm});
            skLineSegment(sketch, "E919", {"start": v(504.81, 8) * mm, "end": v(512.31, 8) * mm});
            skLineSegment(sketch, "E920.MirrorCS", {"start": v(519.81, 8) * mm, "end": v(512.31, 8) * mm});
            skLineSegment(sketch, "E921.MirrorCS", {"start": v(550.56, 0) * mm, "end": v(550.56, 8) * mm});
            skLineSegment(sketch, "E922.MirrorCS", {"start": v(550.56, 8) * mm, "end": v(542.56, 8) * mm});
            skLineSegment(sketch, "E923", {"start": v(489.56, 8) * mm, "end": v(492.81, 40.6) * mm});
            skLineSegment(sketch, "E924", {"start": v(499.81, 40.6) * mm, "end": v(499.81, 8) * mm});
            skLineSegment(sketch, "E925", {"start": v(504.81, 8) * mm, "end": v(504.81, 40.6) * mm});
            skLineSegment(sketch, "E926.MirrorCS", {"start": v(535.06, 8) * mm, "end": v(531.81, 40.6) * mm});
            skLineSegment(sketch, "E927.MirrorCS", {"start": v(524.81, 40.6) * mm, "end": v(524.81, 8) * mm});
            skLineSegment(sketch, "E928.MirrorCS", {"start": v(519.81, 8) * mm, "end": v(519.81, 40.6) * mm});
            skLineSegment(sketch, "E929", {"start": v(450.2, 40.6) * mm, "end": v(564.64, 40.6) * mm, "construction": true});
            skLineSegment(sketch, "E930", {"start": v(654.23, 27.79) * mm, "end": v(654.23, 0) * mm, "construction": true});
            skLineSegment(sketch, "E931", {"start": v(567.68, 0) * mm, "end": v(709.6, 0) * mm, "construction": true});
            skLineSegment(sketch, "E932.bottom", {"start": v(629.73, 44.2) * mm, "end": v(654.23, 44.2) * mm});
            skLineSegment(sketch, "E932.top", {"start": v(634.73, 36.2) * mm, "end": v(641.73, 36.2) * mm});
            skLineSegment(sketch, "E932.left", {"start": v(629.73, 44.2) * mm, "end": v(629.73, 42.2) * mm});
            skLineSegment(sketch, "E933.bottom", {"start": v(616.76, 0) * mm, "end": v(691.7, 0) * mm});
            skLineSegment(sketch, "E933.left", {"start": v(616.76, 0) * mm, "end": v(616.76, 8) * mm});
            skLineSegment(sketch, "E934", {"start": v(624.76, 8) * mm, "end": v(629.73, 36.2) * mm});
            skLineSegment(sketch, "E935", {"start": v(616.76, 8) * mm, "end": v(624.76, 8) * mm});
            skLineSegment(sketch, "E936.bottom", {"start": v(624.23, 45.2) * mm, "end": v(629.23, 45.2) * mm});
            skLineSegment(sketch, "E936.top", {"start": v(624.23, 36.2) * mm, "end": v(629.73, 36.2) * mm});
            skLineSegment(sketch, "E936.left", {"start": v(624.23, 45.2) * mm, "end": v(624.23, 36.2) * mm});
            skLineSegment(sketch, "E937.right", {"start": v(629.23, 45.2) * mm, "end": v(629.23, 42.2) * mm});
            skLineSegment(sketch, "E938", {"start": v(629.23, 42.2) * mm, "end": v(629.73, 42.2) * mm});
            skLineSegment(sketch, "E939.trimOffspring", {"start": v(632.26, 8) * mm, "end": v(641.73, 8) * mm});
            skLineSegment(sketch, "E940", {"start": v(646.73, 36.2) * mm, "end": v(654.23, 36.2) * mm});
            skLineSegment(sketch, "E941.MirrorCS", {"start": v(678.73, 44.2) * mm, "end": v(654.23, 44.2) * mm});
            skLineSegment(sketch, "E942.MirrorCS", {"start": v(678.73, 44.2) * mm, "end": v(678.73, 42.2) * mm});
            skLineSegment(sketch, "E943.MirrorCS", {"start": v(679.23, 42.2) * mm, "end": v(678.73, 42.2) * mm});
            skLineSegment(sketch, "E944.MirrorCS", {"start": v(679.23, 45.2) * mm, "end": v(679.23, 42.2) * mm});
            skLineSegment(sketch, "E945.MirrorCS", {"start": v(684.23, 45.2) * mm, "end": v(679.23, 45.2) * mm});
            skLineSegment(sketch, "E946.MirrorCS", {"start": v(684.23, 45.2) * mm, "end": v(684.23, 36.2) * mm});
            skLineSegment(sketch, "E947.MirrorCS", {"start": v(684.23, 36.2) * mm, "end": v(678.73, 36.2) * mm});
            skLineSegment(sketch, "E948.MirrorCS", {"start": v(673.73, 36.2) * mm, "end": v(666.73, 36.2) * mm});
            skLineSegment(sketch, "E949.MirrorCS", {"start": v(661.73, 36.2) * mm, "end": v(654.23, 36.2) * mm});
            skLineSegment(sketch, "E950.MirrorCS", {"start": v(683.7, 8) * mm, "end": v(678.73, 36.2) * mm});
            skLineSegment(sketch, "E951.MirrorCS", {"start": v(676.2, 8) * mm, "end": v(666.73, 8) * mm});
            skLineSegment(sketch, "E952", {"start": v(646.73, 8) * mm, "end": v(654.23, 8) * mm});
            skLineSegment(sketch, "E953.MirrorCS", {"start": v(661.73, 8) * mm, "end": v(654.23, 8) * mm});
            skLineSegment(sketch, "E954.MirrorCS", {"start": v(691.7, 0) * mm, "end": v(691.7, 8) * mm});
            skLineSegment(sketch, "E955.MirrorCS", {"start": v(691.7, 8) * mm, "end": v(683.7, 8) * mm});
            skLineSegment(sketch, "E956", {"start": v(632.26, 8) * mm, "end": v(634.73, 36.2) * mm});
            skLineSegment(sketch, "E957", {"start": v(641.73, 36.2) * mm, "end": v(641.73, 8) * mm});
            skLineSegment(sketch, "E958", {"start": v(646.73, 8) * mm, "end": v(646.73, 36.2) * mm});
            skLineSegment(sketch, "E959.MirrorCS", {"start": v(676.2, 8) * mm, "end": v(673.73, 36.2) * mm});
            skLineSegment(sketch, "E960.MirrorCS", {"start": v(666.73, 36.2) * mm, "end": v(666.73, 8) * mm});
            skLineSegment(sketch, "E961.MirrorCS", {"start": v(661.73, 8) * mm, "end": v(661.73, 36.2) * mm});
            skLineSegment(sketch, "E962", {"start": v(592.12, 36.2) * mm, "end": v(706.56, 36.2) * mm, "construction": true});
            skLineSegment(sketch, "E963", {"start": v(794.85, 40.2) * mm, "end": v(794.85, 0) * mm, "construction": true});
            skLineSegment(sketch, "E964", {"start": v(709.6, 0) * mm, "end": v(851.53, 0) * mm, "construction": true});
            skLineSegment(sketch, "E965.bottom", {"start": v(770.35, 39.8) * mm, "end": v(794.85, 39.8) * mm});
            skLineSegment(sketch, "E965.top", {"start": v(775.35, 31.8) * mm, "end": v(782.35, 31.8) * mm});
            skLineSegment(sketch, "E965.left", {"start": v(770.35, 39.8) * mm, "end": v(770.35, 37.8) * mm});
            skLineSegment(sketch, "E966.bottom", {"start": v(758.16, 0) * mm, "end": v(831.55, 0) * mm});
            skLineSegment(sketch, "E966.left", {"start": v(758.16, 0) * mm, "end": v(758.16, 8) * mm});
            skLineSegment(sketch, "E967", {"start": v(766.16, 8) * mm, "end": v(770.35, 31.8) * mm});
            skLineSegment(sketch, "E968", {"start": v(758.16, 8) * mm, "end": v(766.16, 8) * mm});
            skLineSegment(sketch, "E969.bottom", {"start": v(764.85, 40.8) * mm, "end": v(769.85, 40.8) * mm});
            skLineSegment(sketch, "E969.top", {"start": v(764.85, 31.8) * mm, "end": v(770.35, 31.8) * mm});
            skLineSegment(sketch, "E969.left", {"start": v(764.85, 40.8) * mm, "end": v(764.85, 31.8) * mm});
            skLineSegment(sketch, "E970.right", {"start": v(769.85, 40.8) * mm, "end": v(769.85, 37.8) * mm});
            skLineSegment(sketch, "E971", {"start": v(769.85, 37.8) * mm, "end": v(770.35, 37.8) * mm});
            skLineSegment(sketch, "E972.trimOffspring", {"start": v(773.66, 8) * mm, "end": v(782.35, 8) * mm});
            skLineSegment(sketch, "E973", {"start": v(787.35, 31.8) * mm, "end": v(794.85, 31.8) * mm});
            skLineSegment(sketch, "E974.MirrorCS", {"start": v(819.35, 39.8) * mm, "end": v(794.85, 39.8) * mm});
            skLineSegment(sketch, "E975.MirrorCS", {"start": v(819.35, 39.8) * mm, "end": v(819.35, 37.8) * mm});
            skLineSegment(sketch, "E976.MirrorCS", {"start": v(819.85, 37.8) * mm, "end": v(819.35, 37.8) * mm});
            skLineSegment(sketch, "E977.MirrorCS", {"start": v(819.85, 40.8) * mm, "end": v(819.85, 37.8) * mm});
            skLineSegment(sketch, "E978.MirrorCS", {"start": v(824.85, 40.8) * mm, "end": v(819.85, 40.8) * mm});
            skLineSegment(sketch, "E979.MirrorCS", {"start": v(824.85, 40.8) * mm, "end": v(824.85, 31.8) * mm});
            skLineSegment(sketch, "E980.MirrorCS", {"start": v(824.85, 31.8) * mm, "end": v(819.35, 31.8) * mm});
            skLineSegment(sketch, "E981.MirrorCS", {"start": v(814.35, 31.8) * mm, "end": v(807.35, 31.8) * mm});
            skLineSegment(sketch, "E982.MirrorCS", {"start": v(802.35, 31.8) * mm, "end": v(794.85, 31.8) * mm});
            skLineSegment(sketch, "E983.MirrorCS", {"start": v(823.55, 8) * mm, "end": v(819.35, 31.8) * mm});
            skLineSegment(sketch, "E984.MirrorCS", {"start": v(816.05, 8) * mm, "end": v(807.35, 8) * mm});
            skLineSegment(sketch, "E985", {"start": v(787.35, 8) * mm, "end": v(794.85, 8) * mm});
            skLineSegment(sketch, "E986.MirrorCS", {"start": v(802.35, 8) * mm, "end": v(794.85, 8) * mm});
            skLineSegment(sketch, "E987.MirrorCS", {"start": v(831.55, 0) * mm, "end": v(831.55, 8) * mm});
            skLineSegment(sketch, "E988.MirrorCS", {"start": v(831.55, 8) * mm, "end": v(823.55, 8) * mm});
            skLineSegment(sketch, "E989", {"start": v(773.66, 8) * mm, "end": v(775.35, 31.8) * mm});
            skLineSegment(sketch, "E990", {"start": v(782.35, 31.8) * mm, "end": v(782.35, 8) * mm});
            skLineSegment(sketch, "E991", {"start": v(787.35, 8) * mm, "end": v(787.35, 31.8) * mm});
            skLineSegment(sketch, "E992.MirrorCS", {"start": v(816.05, 8) * mm, "end": v(814.35, 31.8) * mm});
            skLineSegment(sketch, "E993.MirrorCS", {"start": v(807.35, 31.8) * mm, "end": v(807.35, 8) * mm});
            skLineSegment(sketch, "E994.MirrorCS", {"start": v(802.35, 8) * mm, "end": v(802.35, 31.8) * mm});
            skLineSegment(sketch, "E995", {"start": v(734.04, 31.8) * mm, "end": v(848.48, 31.8) * mm, "construction": true});
            skLineSegment(sketch, "E996", {"start": v(938.07, 44.17) * mm, "end": v(938.07, 0) * mm, "construction": true});
            skLineSegment(sketch, "E997", {"start": v(851.53, 0) * mm, "end": v(993.45, 0) * mm, "construction": true});
            skLineSegment(sketch, "E998.bottom", {"start": v(913.57, 38.7) * mm, "end": v(938.07, 38.7) * mm});
            skLineSegment(sketch, "E998.top", {"start": v(918.57, 30.7) * mm, "end": v(925.57, 30.7) * mm});
            skLineSegment(sketch, "E998.left", {"start": v(913.57, 38.7) * mm, "end": v(913.57, 36.7) * mm});
            skLineSegment(sketch, "E999.bottom", {"start": v(901.57, 0) * mm, "end": v(974.58, 0) * mm});
            skLineSegment(sketch, "E999.left", {"start": v(901.57, 0) * mm, "end": v(901.57, 8) * mm});
            skLineSegment(sketch, "E1000", {"start": v(909.57, 8) * mm, "end": v(913.57, 30.7) * mm});
            skLineSegment(sketch, "E1001", {"start": v(901.57, 8) * mm, "end": v(909.57, 8) * mm});
            skLineSegment(sketch, "E1002.bottom", {"start": v(908.07, 39.7) * mm, "end": v(913.07, 39.7) * mm});
            skLineSegment(sketch, "E1002.top", {"start": v(908.07, 30.7) * mm, "end": v(913.57, 30.7) * mm});
            skLineSegment(sketch, "E1002.left", {"start": v(908.07, 39.7) * mm, "end": v(908.07, 30.7) * mm});
            skLineSegment(sketch, "E1003.right", {"start": v(913.07, 39.7) * mm, "end": v(913.07, 36.7) * mm});
            skLineSegment(sketch, "E1004", {"start": v(913.07, 36.7) * mm, "end": v(913.57, 36.7) * mm});
            skLineSegment(sketch, "E1005.trimOffspring", {"start": v(917.07, 8) * mm, "end": v(925.57, 8) * mm});
            skLineSegment(sketch, "E1006", {"start": v(930.57, 30.7) * mm, "end": v(938.07, 30.7) * mm});
            skLineSegment(sketch, "E1007.MirrorCS", {"start": v(962.57, 38.7) * mm, "end": v(938.07, 38.7) * mm});
            skLineSegment(sketch, "E1008.MirrorCS", {"start": v(962.57, 38.7) * mm, "end": v(962.57, 36.7) * mm});
            skLineSegment(sketch, "E1009.MirrorCS", {"start": v(963.07, 36.7) * mm, "end": v(962.57, 36.7) * mm});
            skLineSegment(sketch, "E1010.MirrorCS", {"start": v(963.07, 39.7) * mm, "end": v(963.07, 36.7) * mm});
            skLineSegment(sketch, "E1011.MirrorCS", {"start": v(968.07, 39.7) * mm, "end": v(963.07, 39.7) * mm});
            skLineSegment(sketch, "E1012.MirrorCS", {"start": v(968.07, 39.7) * mm, "end": v(968.07, 30.7) * mm});
            skLineSegment(sketch, "E1013.MirrorCS", {"start": v(968.07, 30.7) * mm, "end": v(962.57, 30.7) * mm});
            skLineSegment(sketch, "E1014.MirrorCS", {"start": v(957.57, 30.7) * mm, "end": v(950.57, 30.7) * mm});
            skLineSegment(sketch, "E1015.MirrorCS", {"start": v(945.57, 30.7) * mm, "end": v(938.07, 30.7) * mm});
            skLineSegment(sketch, "E1016.MirrorCS", {"start": v(966.58, 8) * mm, "end": v(962.57, 30.7) * mm});
            skLineSegment(sketch, "E1017.MirrorCS", {"start": v(959.08, 8) * mm, "end": v(950.57, 8) * mm});
            skLineSegment(sketch, "E1018", {"start": v(930.57, 8) * mm, "end": v(938.07, 8) * mm});
            skLineSegment(sketch, "E1019.MirrorCS", {"start": v(945.57, 8) * mm, "end": v(938.07, 8) * mm});
            skLineSegment(sketch, "E1020.MirrorCS", {"start": v(974.58, 0) * mm, "end": v(974.58, 8) * mm});
            skLineSegment(sketch, "E1021.MirrorCS", {"start": v(974.58, 8) * mm, "end": v(966.58, 8) * mm});
            skLineSegment(sketch, "E1022", {"start": v(917.07, 8) * mm, "end": v(918.57, 30.7) * mm});
            skLineSegment(sketch, "E1023", {"start": v(925.57, 30.7) * mm, "end": v(925.57, 8) * mm});
            skLineSegment(sketch, "E1024", {"start": v(930.57, 8) * mm, "end": v(930.57, 30.7) * mm});
            skLineSegment(sketch, "E1025.MirrorCS", {"start": v(959.08, 8) * mm, "end": v(957.57, 30.7) * mm});
            skLineSegment(sketch, "E1026.MirrorCS", {"start": v(950.57, 30.7) * mm, "end": v(950.57, 8) * mm});
            skLineSegment(sketch, "E1027.MirrorCS", {"start": v(945.57, 8) * mm, "end": v(945.57, 30.7) * mm});
            skLineSegment(sketch, "E1028", {"start": v(875.96, 30.7) * mm, "end": v(990.4, 30.7) * mm, "construction": true});
            skLineSegment(sketch, "E1029", {"start": v(1080, 9.24) * mm, "end": v(1080, 0) * mm, "construction": true});
            skLineSegment(sketch, "E1030", {"start": v(993.45, 0) * mm, "end": v(1135.37, 0) * mm, "construction": true});
            skLineSegment(sketch, "E1031.bottom", {"start": v(1055.5, 34.8) * mm, "end": v(1080, 34.8) * mm});
            skLineSegment(sketch, "E1031.top", {"start": v(1060.5, 26.8) * mm, "end": v(1067.5, 26.8) * mm});
            skLineSegment(sketch, "E1031.left", {"start": v(1055.5, 34.8) * mm, "end": v(1055.5, 32.8) * mm});
            skLineSegment(sketch, "E1032.bottom", {"start": v(1044.18, 0) * mm, "end": v(1115.81, 0) * mm});
            skLineSegment(sketch, "E1032.left", {"start": v(1044.18, 0) * mm, "end": v(1044.18, 8) * mm});
            skLineSegment(sketch, "E1033", {"start": v(1052.18, 8) * mm, "end": v(1055.5, 26.8) * mm});
            skLineSegment(sketch, "E1034", {"start": v(1044.18, 8) * mm, "end": v(1052.18, 8) * mm});
            skLineSegment(sketch, "E1035.bottom", {"start": v(1050, 35.8) * mm, "end": v(1055, 35.8) * mm});
            skLineSegment(sketch, "E1035.top", {"start": v(1050, 26.8) * mm, "end": v(1055.5, 26.8) * mm});
            skLineSegment(sketch, "E1035.left", {"start": v(1050, 35.8) * mm, "end": v(1050, 26.8) * mm});
            skLineSegment(sketch, "E1036.right", {"start": v(1055, 35.8) * mm, "end": v(1055, 32.8) * mm});
            skLineSegment(sketch, "E1037", {"start": v(1055, 32.8) * mm, "end": v(1055.5, 32.8) * mm});
            skLineSegment(sketch, "E1038.trimOffspring", {"start": v(1059.68, 8) * mm, "end": v(1067.5, 8) * mm});
            skLineSegment(sketch, "E1039", {"start": v(1072.5, 26.8) * mm, "end": v(1080, 26.8) * mm});
            skLineSegment(sketch, "E1040.MirrorCS", {"start": v(1104.5, 34.8) * mm, "end": v(1080, 34.8) * mm});
            skLineSegment(sketch, "E1041.MirrorCS", {"start": v(1104.5, 34.8) * mm, "end": v(1104.5, 32.8) * mm});
            skLineSegment(sketch, "E1042.MirrorCS", {"start": v(1105, 32.8) * mm, "end": v(1104.5, 32.8) * mm});
            skLineSegment(sketch, "E1043.MirrorCS", {"start": v(1105, 35.8) * mm, "end": v(1105, 32.8) * mm});
            skLineSegment(sketch, "E1044.MirrorCS", {"start": v(1110, 35.8) * mm, "end": v(1105, 35.8) * mm});
            skLineSegment(sketch, "E1045.MirrorCS", {"start": v(1110, 35.8) * mm, "end": v(1110, 26.8) * mm});
            skLineSegment(sketch, "E1046.MirrorCS", {"start": v(1110, 26.8) * mm, "end": v(1104.5, 26.8) * mm});
            skLineSegment(sketch, "E1047.MirrorCS", {"start": v(1099.5, 26.8) * mm, "end": v(1092.5, 26.8) * mm});
            skLineSegment(sketch, "E1048.MirrorCS", {"start": v(1087.5, 26.8) * mm, "end": v(1080, 26.8) * mm});
            skLineSegment(sketch, "E1049.MirrorCS", {"start": v(1107.81, 8) * mm, "end": v(1104.5, 26.8) * mm});
            skLineSegment(sketch, "E1050.MirrorCS", {"start": v(1100.31, 8) * mm, "end": v(1092.5, 8) * mm});
            skLineSegment(sketch, "E1051", {"start": v(1072.5, 8) * mm, "end": v(1080, 8) * mm});
            skLineSegment(sketch, "E1052.MirrorCS", {"start": v(1087.5, 8) * mm, "end": v(1080, 8) * mm});
            skLineSegment(sketch, "E1053.MirrorCS", {"start": v(1115.81, 0) * mm, "end": v(1115.81, 8) * mm});
            skLineSegment(sketch, "E1054.MirrorCS", {"start": v(1115.81, 8) * mm, "end": v(1107.81, 8) * mm});
            skLineSegment(sketch, "E1055", {"start": v(1059.68, 8) * mm, "end": v(1060.5, 26.8) * mm});
            skLineSegment(sketch, "E1056", {"start": v(1067.5, 26.8) * mm, "end": v(1067.5, 8) * mm});
            skLineSegment(sketch, "E1057", {"start": v(1072.5, 8) * mm, "end": v(1072.5, 26.8) * mm});
            skLineSegment(sketch, "E1058.MirrorCS", {"start": v(1100.31, 8) * mm, "end": v(1099.5, 26.8) * mm});
            skLineSegment(sketch, "E1059.MirrorCS", {"start": v(1092.5, 26.8) * mm, "end": v(1092.5, 8) * mm});
            skLineSegment(sketch, "E1060.MirrorCS", {"start": v(1087.5, 8) * mm, "end": v(1087.5, 26.8) * mm});
            skLineSegment(sketch, "E1061", {"start": v(1017.88, 26.8) * mm, "end": v(1132.32, 26.8) * mm, "construction": true});
            skLineSegment(sketch, "E1062", {"start": v(1220.61, 21.66) * mm, "end": v(1220.61, 0) * mm, "construction": true});
            skLineSegment(sketch, "E1063", {"start": v(1135.37, 0) * mm, "end": v(1277.29, 0) * mm, "construction": true});
            skLineSegment(sketch, "E1064.bottom", {"start": v(1196.11, 30.9) * mm, "end": v(1220.61, 30.9) * mm});
            skLineSegment(sketch, "E1064.top", {"start": v(1201.11, 22.9) * mm, "end": v(1208.11, 22.9) * mm});
            skLineSegment(sketch, "E1064.left", {"start": v(1196.11, 30.9) * mm, "end": v(1196.11, 28.9) * mm});
            skLineSegment(sketch, "E1065.bottom", {"start": v(1185.49, 0) * mm, "end": v(1255.74, 0) * mm});
            skLineSegment(sketch, "E1065.left", {"start": v(1185.49, 0) * mm, "end": v(1185.49, 8) * mm});
            skLineSegment(sketch, "E1066", {"start": v(1193.49, 8) * mm, "end": v(1196.11, 22.9) * mm});
            skLineSegment(sketch, "E1067", {"start": v(1185.49, 8) * mm, "end": v(1193.49, 8) * mm});
            skLineSegment(sketch, "E1068.bottom", {"start": v(1190.61, 31.9) * mm, "end": v(1195.61, 31.9) * mm});
            skLineSegment(sketch, "E1068.top", {"start": v(1190.61, 22.9) * mm, "end": v(1196.11, 22.9) * mm});
            skLineSegment(sketch, "E1068.left", {"start": v(1190.61, 31.9) * mm, "end": v(1190.61, 22.9) * mm});
            skLineSegment(sketch, "E1069.right", {"start": v(1195.61, 31.9) * mm, "end": v(1195.61, 28.9) * mm});
            skLineSegment(sketch, "E1070", {"start": v(1195.61, 28.9) * mm, "end": v(1196.11, 28.9) * mm});
            skLineSegment(sketch, "E1071.trimOffspring", {"start": v(1200.99, 8) * mm, "end": v(1208.11, 8) * mm});
            skLineSegment(sketch, "E1072", {"start": v(1213.11, 22.9) * mm, "end": v(1220.61, 22.9) * mm});
            skLineSegment(sketch, "E1073.MirrorCS", {"start": v(1245.11, 30.9) * mm, "end": v(1220.61, 30.9) * mm});
            skLineSegment(sketch, "E1074.MirrorCS", {"start": v(1245.11, 30.9) * mm, "end": v(1245.11, 28.9) * mm});
            skLineSegment(sketch, "E1075.MirrorCS", {"start": v(1245.61, 28.9) * mm, "end": v(1245.11, 28.9) * mm});
            skLineSegment(sketch, "E1076.MirrorCS", {"start": v(1245.61, 31.9) * mm, "end": v(1245.61, 28.9) * mm});
            skLineSegment(sketch, "E1077.MirrorCS", {"start": v(1250.61, 31.9) * mm, "end": v(1245.61, 31.9) * mm});
            skLineSegment(sketch, "E1078.MirrorCS", {"start": v(1250.61, 31.9) * mm, "end": v(1250.61, 22.9) * mm});
            skLineSegment(sketch, "E1079.MirrorCS", {"start": v(1250.61, 22.9) * mm, "end": v(1245.11, 22.9) * mm});
            skLineSegment(sketch, "E1080.MirrorCS", {"start": v(1240.11, 22.9) * mm, "end": v(1233.11, 22.9) * mm});
            skLineSegment(sketch, "E1081.MirrorCS", {"start": v(1228.11, 22.9) * mm, "end": v(1220.61, 22.9) * mm});
            skLineSegment(sketch, "E1082.MirrorCS", {"start": v(1247.74, 8) * mm, "end": v(1245.11, 22.9) * mm});
            skLineSegment(sketch, "E1083.MirrorCS", {"start": v(1240.24, 8) * mm, "end": v(1233.11, 8) * mm});
            skLineSegment(sketch, "E1084", {"start": v(1213.11, 8) * mm, "end": v(1220.61, 8) * mm});
            skLineSegment(sketch, "E1085.MirrorCS", {"start": v(1228.11, 8) * mm, "end": v(1220.61, 8) * mm});
            skLineSegment(sketch, "E1086.MirrorCS", {"start": v(1255.74, 0) * mm, "end": v(1255.74, 8) * mm});
            skLineSegment(sketch, "E1087.MirrorCS", {"start": v(1255.74, 8) * mm, "end": v(1247.74, 8) * mm});
            skLineSegment(sketch, "E1088", {"start": v(1200.99, 8) * mm, "end": v(1201.11, 22.9) * mm});
            skLineSegment(sketch, "E1089", {"start": v(1208.11, 22.9) * mm, "end": v(1208.11, 8) * mm});
            skLineSegment(sketch, "E1090", {"start": v(1213.11, 8) * mm, "end": v(1213.11, 22.9) * mm});
            skLineSegment(sketch, "E1091.MirrorCS", {"start": v(1240.24, 8) * mm, "end": v(1240.11, 22.9) * mm});
            skLineSegment(sketch, "E1092.MirrorCS", {"start": v(1233.11, 22.9) * mm, "end": v(1233.11, 8) * mm});
            skLineSegment(sketch, "E1093.MirrorCS", {"start": v(1228.11, 8) * mm, "end": v(1228.11, 22.9) * mm});
            skLineSegment(sketch, "E1094", {"start": v(1159.8, 22.9) * mm, "end": v(1274.24, 22.9) * mm, "construction": true});
            skLineSegment(sketch, "E1095", {"start": v(1363.84, 50.68) * mm, "end": v(1363.84, 0) * mm, "construction": true});
            skLineSegment(sketch, "E1096", {"start": v(1277.29, 0) * mm, "end": v(1419.2, 0) * mm, "construction": true});
            skLineSegment(sketch, "E1097.bottom", {"start": v(1339.34, 30) * mm, "end": v(1363.84, 30) * mm});
            skLineSegment(sketch, "E1097.top", {"start": v(1344.34, 22) * mm, "end": v(1351.34, 22) * mm});
            skLineSegment(sketch, "E1097.left", {"start": v(1339.34, 30) * mm, "end": v(1339.34, 28) * mm});
            skLineSegment(sketch, "E1098.bottom", {"start": v(1328.87, 0) * mm, "end": v(1398.8, 0) * mm});
            skLineSegment(sketch, "E1098.left", {"start": v(1328.87, 0) * mm, "end": v(1328.87, 8) * mm});
            skLineSegment(sketch, "E1099", {"start": v(1336.87, 8) * mm, "end": v(1339.34, 22) * mm});
            skLineSegment(sketch, "E1100", {"start": v(1328.87, 8) * mm, "end": v(1336.87, 8) * mm});
            skLineSegment(sketch, "E1101.bottom", {"start": v(1333.84, 31) * mm, "end": v(1338.84, 31) * mm});
            skLineSegment(sketch, "E1101.top", {"start": v(1333.84, 22) * mm, "end": v(1339.34, 22) * mm});
            skLineSegment(sketch, "E1101.left", {"start": v(1333.84, 31) * mm, "end": v(1333.84, 22) * mm});
            skLineSegment(sketch, "E1102.right", {"start": v(1338.84, 31) * mm, "end": v(1338.84, 28) * mm});
            skLineSegment(sketch, "E1103", {"start": v(1338.84, 28) * mm, "end": v(1339.34, 28) * mm});
            skLineSegment(sketch, "E1104.trimOffspring", {"start": v(1344.37, 8) * mm, "end": v(1351.34, 8) * mm});
            skLineSegment(sketch, "E1105", {"start": v(1356.34, 22) * mm, "end": v(1363.84, 22) * mm});
            skLineSegment(sketch, "E1106.MirrorCS", {"start": v(1388.34, 30) * mm, "end": v(1363.84, 30) * mm});
            skLineSegment(sketch, "E1107.MirrorCS", {"start": v(1388.34, 30) * mm, "end": v(1388.34, 28) * mm});
            skLineSegment(sketch, "E1108.MirrorCS", {"start": v(1388.84, 28) * mm, "end": v(1388.34, 28) * mm});
            skLineSegment(sketch, "E1109.MirrorCS", {"start": v(1388.84, 31) * mm, "end": v(1388.84, 28) * mm});
            skLineSegment(sketch, "E1110.MirrorCS", {"start": v(1393.84, 31) * mm, "end": v(1388.84, 31) * mm});
            skLineSegment(sketch, "E1111.MirrorCS", {"start": v(1393.84, 31) * mm, "end": v(1393.84, 22) * mm});
            skLineSegment(sketch, "E1112.MirrorCS", {"start": v(1393.84, 22) * mm, "end": v(1388.34, 22) * mm});
            skLineSegment(sketch, "E1113.MirrorCS", {"start": v(1383.34, 22) * mm, "end": v(1376.34, 22) * mm});
            skLineSegment(sketch, "E1114.MirrorCS", {"start": v(1371.34, 22) * mm, "end": v(1363.84, 22) * mm});
            skLineSegment(sketch, "E1115.MirrorCS", {"start": v(1390.8, 8) * mm, "end": v(1388.34, 22) * mm});
            skLineSegment(sketch, "E1116.MirrorCS", {"start": v(1383.3, 8) * mm, "end": v(1376.34, 8) * mm});
            skLineSegment(sketch, "E1117", {"start": v(1356.34, 8) * mm, "end": v(1363.84, 8) * mm});
            skLineSegment(sketch, "E1118.MirrorCS", {"start": v(1371.34, 8) * mm, "end": v(1363.84, 8) * mm});
            skLineSegment(sketch, "E1119.MirrorCS", {"start": v(1398.8, 0) * mm, "end": v(1398.8, 8) * mm});
            skLineSegment(sketch, "E1120.MirrorCS", {"start": v(1398.8, 8) * mm, "end": v(1390.8, 8) * mm});
            skLineSegment(sketch, "E1121", {"start": v(1344.37, 8) * mm, "end": v(1344.34, 22) * mm});
            skLineSegment(sketch, "E1122", {"start": v(1351.34, 22) * mm, "end": v(1351.34, 8) * mm});
            skLineSegment(sketch, "E1123", {"start": v(1356.34, 8) * mm, "end": v(1356.34, 22) * mm});
            skLineSegment(sketch, "E1124.MirrorCS", {"start": v(1383.3, 8) * mm, "end": v(1383.34, 22) * mm});
            skLineSegment(sketch, "E1125.MirrorCS", {"start": v(1376.34, 22) * mm, "end": v(1376.34, 8) * mm});
            skLineSegment(sketch, "E1126.MirrorCS", {"start": v(1371.34, 8) * mm, "end": v(1371.34, 22) * mm});
            skLineSegment(sketch, "E1127", {"start": v(1301.72, 22) * mm, "end": v(1416.16, 22) * mm, "construction": true});
            skLineSegment(sketch, "E1128", {"start": v(1505.76, 15.76) * mm, "end": v(1505.76, 0) * mm, "construction": true});
            skLineSegment(sketch, "E1129", {"start": v(1419.2, 0) * mm, "end": v(1561.13, 0) * mm, "construction": true});
            skLineSegment(sketch, "E1130.bottom", {"start": v(1481.26, 26.1) * mm, "end": v(1505.76, 26.1) * mm});
            skLineSegment(sketch, "E1130.top", {"start": v(1486.26, 18.1) * mm, "end": v(1493.26, 18.1) * mm});
            skLineSegment(sketch, "E1130.left", {"start": v(1481.26, 26.1) * mm, "end": v(1481.26, 24.1) * mm});
            skLineSegment(sketch, "E1131.bottom", {"start": v(1471.48, 0) * mm, "end": v(1540.04, 0) * mm});
            skLineSegment(sketch, "E1131.left", {"start": v(1471.48, 0) * mm, "end": v(1471.48, 8) * mm});
            skLineSegment(sketch, "E1132", {"start": v(1479.48, 8) * mm, "end": v(1481.26, 18.1) * mm});
            skLineSegment(sketch, "E1133", {"start": v(1471.48, 8) * mm, "end": v(1479.48, 8) * mm});
            skLineSegment(sketch, "E1134.bottom", {"start": v(1475.76, 27.1) * mm, "end": v(1480.76, 27.1) * mm});
            skLineSegment(sketch, "E1134.top", {"start": v(1475.76, 18.1) * mm, "end": v(1481.26, 18.1) * mm});
            skLineSegment(sketch, "E1134.left", {"start": v(1475.76, 27.1) * mm, "end": v(1475.76, 18.1) * mm});
            skLineSegment(sketch, "E1135.right", {"start": v(1480.76, 27.1) * mm, "end": v(1480.76, 24.1) * mm});
            skLineSegment(sketch, "E1136", {"start": v(1480.76, 24.1) * mm, "end": v(1481.26, 24.1) * mm});
            skLineSegment(sketch, "E1137.trimOffspring", {"start": v(1486.98, 8) * mm, "end": v(1493.26, 8) * mm});
            skLineSegment(sketch, "E1138", {"start": v(1498.26, 18.1) * mm, "end": v(1505.76, 18.1) * mm});
            skLineSegment(sketch, "E1139.MirrorCS", {"start": v(1530.26, 26.1) * mm, "end": v(1505.76, 26.1) * mm});
            skLineSegment(sketch, "E1140.MirrorCS", {"start": v(1530.26, 26.1) * mm, "end": v(1530.26, 24.1) * mm});
            skLineSegment(sketch, "E1141.MirrorCS", {"start": v(1530.76, 24.1) * mm, "end": v(1530.26, 24.1) * mm});
            skLineSegment(sketch, "E1142.MirrorCS", {"start": v(1530.76, 27.1) * mm, "end": v(1530.76, 24.1) * mm});
            skLineSegment(sketch, "E1143.MirrorCS", {"start": v(1535.76, 27.1) * mm, "end": v(1530.76, 27.1) * mm});
            skLineSegment(sketch, "E1144.MirrorCS", {"start": v(1535.76, 27.1) * mm, "end": v(1535.76, 18.1) * mm});
            skLineSegment(sketch, "E1145.MirrorCS", {"start": v(1535.76, 18.1) * mm, "end": v(1530.26, 18.1) * mm});
            skLineSegment(sketch, "E1146.MirrorCS", {"start": v(1525.26, 18.1) * mm, "end": v(1518.26, 18.1) * mm});
            skLineSegment(sketch, "E1147.MirrorCS", {"start": v(1513.26, 18.1) * mm, "end": v(1505.76, 18.1) * mm});
            skLineSegment(sketch, "E1148.MirrorCS", {"start": v(1532.04, 8) * mm, "end": v(1530.26, 18.1) * mm});
            skLineSegment(sketch, "E1149.MirrorCS", {"start": v(1524.54, 8) * mm, "end": v(1518.26, 8) * mm});
            skLineSegment(sketch, "E1150", {"start": v(1498.26, 8) * mm, "end": v(1505.76, 8) * mm});
            skLineSegment(sketch, "E1151.MirrorCS", {"start": v(1513.26, 8) * mm, "end": v(1505.76, 8) * mm});
            skLineSegment(sketch, "E1152.MirrorCS", {"start": v(1540.04, 0) * mm, "end": v(1540.04, 8) * mm});
            skLineSegment(sketch, "E1153.MirrorCS", {"start": v(1540.04, 8) * mm, "end": v(1532.04, 8) * mm});
            skLineSegment(sketch, "E1154", {"start": v(1486.98, 8) * mm, "end": v(1486.26, 18.1) * mm});
            skLineSegment(sketch, "E1155", {"start": v(1493.26, 18.1) * mm, "end": v(1493.26, 8) * mm});
            skLineSegment(sketch, "E1156", {"start": v(1498.26, 8) * mm, "end": v(1498.26, 18.1) * mm});
            skLineSegment(sketch, "E1157.MirrorCS", {"start": v(1524.54, 8) * mm, "end": v(1525.26, 18.1) * mm});
            skLineSegment(sketch, "E1158.MirrorCS", {"start": v(1518.26, 18.1) * mm, "end": v(1518.26, 8) * mm});
            skLineSegment(sketch, "E1159.MirrorCS", {"start": v(1513.26, 8) * mm, "end": v(1513.26, 18.1) * mm});
            skLineSegment(sketch, "E1160", {"start": v(1443.65, 18.1) * mm, "end": v(1558.08, 18.1) * mm, "construction": true});
            skLineSegment(sketch, "E1161", {"start": v(1646.38, 28.17) * mm, "end": v(1646.38, 0) * mm, "construction": true});
            skLineSegment(sketch, "E1162", {"start": v(1561.13, 0) * mm, "end": v(1703.05, 0) * mm, "construction": true});
            skLineSegment(sketch, "E1163.bottom", {"start": v(1621.88, 22.2) * mm, "end": v(1646.38, 22.2) * mm});
            skLineSegment(sketch, "E1163.top", {"start": v(1626.88, 14.2) * mm, "end": v(1633.88, 14.2) * mm});
            skLineSegment(sketch, "E1163.left", {"start": v(1621.88, 22.2) * mm, "end": v(1621.88, 20.2) * mm});
            skLineSegment(sketch, "E1164.bottom", {"start": v(1612.78, 0) * mm, "end": v(1679.97, 0) * mm});
            skLineSegment(sketch, "E1164.left", {"start": v(1612.78, 0) * mm, "end": v(1612.78, 8) * mm});
            skLineSegment(sketch, "E1165", {"start": v(1620.78, 8) * mm, "end": v(1621.88, 14.2) * mm});
            skLineSegment(sketch, "E1166", {"start": v(1612.78, 8) * mm, "end": v(1620.78, 8) * mm});
            skLineSegment(sketch, "E1167.bottom", {"start": v(1616.38, 23.2) * mm, "end": v(1621.38, 23.2) * mm});
            skLineSegment(sketch, "E1167.top", {"start": v(1616.38, 14.2) * mm, "end": v(1621.88, 14.2) * mm});
            skLineSegment(sketch, "E1167.left", {"start": v(1616.38, 23.2) * mm, "end": v(1616.38, 14.2) * mm});
            skLineSegment(sketch, "E1168.right", {"start": v(1621.38, 23.2) * mm, "end": v(1621.38, 20.2) * mm});
            skLineSegment(sketch, "E1169", {"start": v(1621.38, 20.2) * mm, "end": v(1621.88, 20.2) * mm});
            skLineSegment(sketch, "E1170.trimOffspring", {"start": v(1628.28, 8) * mm, "end": v(1633.88, 8) * mm});
            skLineSegment(sketch, "E1171", {"start": v(1638.88, 14.2) * mm, "end": v(1646.38, 14.2) * mm});
            skLineSegment(sketch, "E1172.MirrorCS", {"start": v(1670.88, 22.2) * mm, "end": v(1646.38, 22.2) * mm});
            skLineSegment(sketch, "E1173.MirrorCS", {"start": v(1670.88, 22.2) * mm, "end": v(1670.88, 20.2) * mm});
            skLineSegment(sketch, "E1174.MirrorCS", {"start": v(1671.38, 20.2) * mm, "end": v(1670.88, 20.2) * mm});
            skLineSegment(sketch, "E1175.MirrorCS", {"start": v(1671.38, 23.2) * mm, "end": v(1671.38, 20.2) * mm});
            skLineSegment(sketch, "E1176.MirrorCS", {"start": v(1676.38, 23.2) * mm, "end": v(1671.38, 23.2) * mm});
            skLineSegment(sketch, "E1177.MirrorCS", {"start": v(1676.38, 23.2) * mm, "end": v(1676.38, 14.2) * mm});
            skLineSegment(sketch, "E1178.MirrorCS", {"start": v(1676.38, 14.2) * mm, "end": v(1670.88, 14.2) * mm});
            skLineSegment(sketch, "E1179.MirrorCS", {"start": v(1665.88, 14.2) * mm, "end": v(1658.88, 14.2) * mm});
            skLineSegment(sketch, "E1180.MirrorCS", {"start": v(1653.88, 14.2) * mm, "end": v(1646.38, 14.2) * mm});
            skLineSegment(sketch, "E1181.MirrorCS", {"start": v(1671.97, 8) * mm, "end": v(1670.88, 14.2) * mm});
            skLineSegment(sketch, "E1182.MirrorCS", {"start": v(1664.47, 8) * mm, "end": v(1658.88, 8) * mm});
            skLineSegment(sketch, "E1183", {"start": v(1638.88, 8) * mm, "end": v(1646.38, 8) * mm});
            skLineSegment(sketch, "E1184.MirrorCS", {"start": v(1653.88, 8) * mm, "end": v(1646.38, 8) * mm});
            skLineSegment(sketch, "E1185.MirrorCS", {"start": v(1679.97, 0) * mm, "end": v(1679.97, 8) * mm});
            skLineSegment(sketch, "E1186.MirrorCS", {"start": v(1679.97, 8) * mm, "end": v(1671.97, 8) * mm});
            skLineSegment(sketch, "E1187", {"start": v(1628.28, 8) * mm, "end": v(1626.88, 14.2) * mm});
            skLineSegment(sketch, "E1188", {"start": v(1633.88, 14.2) * mm, "end": v(1633.88, 8) * mm});
            skLineSegment(sketch, "E1189", {"start": v(1638.88, 8) * mm, "end": v(1638.88, 14.2) * mm});
            skLineSegment(sketch, "E1190.MirrorCS", {"start": v(1664.47, 8) * mm, "end": v(1665.88, 14.2) * mm});
            skLineSegment(sketch, "E1191.MirrorCS", {"start": v(1658.88, 14.2) * mm, "end": v(1658.88, 8) * mm});
            skLineSegment(sketch, "E1192.MirrorCS", {"start": v(1653.88, 8) * mm, "end": v(1653.88, 14.2) * mm});
            skLineSegment(sketch, "E1193", {"start": v(1585.57, 14.2) * mm, "end": v(1700, 14.2) * mm, "construction": true});
            skLineSegment(sketch, "E1194", {"start": v(1789.6, 52.22) * mm, "end": v(1789.6, 0) * mm, "construction": true});
            skLineSegment(sketch, "E1195", {"start": v(1703.05, 0) * mm, "end": v(1844.97, 0) * mm, "construction": true});
            skLineSegment(sketch, "E1196.bottom", {"start": v(1765.1, 21.3) * mm, "end": v(1789.6, 21.3) * mm});
            skLineSegment(sketch, "E1196.top", {"start": v(1770.1, 13.3) * mm, "end": v(1777.1, 13.3) * mm});
            skLineSegment(sketch, "E1196.left", {"start": v(1765.1, 21.3) * mm, "end": v(1765.1, 19.3) * mm});
            skLineSegment(sketch, "E1197.bottom", {"start": v(1756.17, 0) * mm, "end": v(1823.04, 0) * mm});
            skLineSegment(sketch, "E1197.left", {"start": v(1756.17, 0) * mm, "end": v(1756.17, 8) * mm});
            skLineSegment(sketch, "E1198", {"start": v(1764.17, 8) * mm, "end": v(1765.1, 13.3) * mm});
            skLineSegment(sketch, "E1199", {"start": v(1756.17, 8) * mm, "end": v(1764.17, 8) * mm});
            skLineSegment(sketch, "E1200.bottom", {"start": v(1759.6, 22.3) * mm, "end": v(1764.6, 22.3) * mm});
            skLineSegment(sketch, "E1200.top", {"start": v(1759.6, 13.3) * mm, "end": v(1765.1, 13.3) * mm});
            skLineSegment(sketch, "E1200.left", {"start": v(1759.6, 22.3) * mm, "end": v(1759.6, 13.3) * mm});
            skLineSegment(sketch, "E1201.right", {"start": v(1764.6, 22.3) * mm, "end": v(1764.6, 19.3) * mm});
            skLineSegment(sketch, "E1202", {"start": v(1764.6, 19.3) * mm, "end": v(1765.1, 19.3) * mm});
            skLineSegment(sketch, "E1203.trimOffspring", {"start": v(1771.67, 8) * mm, "end": v(1777.1, 8) * mm});
            skLineSegment(sketch, "E1204", {"start": v(1782.1, 13.3) * mm, "end": v(1789.6, 13.3) * mm});
            skLineSegment(sketch, "E1205.MirrorCS", {"start": v(1814.1, 21.3) * mm, "end": v(1789.6, 21.3) * mm});
            skLineSegment(sketch, "E1206.MirrorCS", {"start": v(1814.1, 21.3) * mm, "end": v(1814.1, 19.3) * mm});
            skLineSegment(sketch, "E1207.MirrorCS", {"start": v(1814.6, 19.3) * mm, "end": v(1814.1, 19.3) * mm});
            skLineSegment(sketch, "E1208.MirrorCS", {"start": v(1814.6, 22.3) * mm, "end": v(1814.6, 19.3) * mm});
            skLineSegment(sketch, "E1209.MirrorCS", {"start": v(1819.6, 22.3) * mm, "end": v(1814.6, 22.3) * mm});
            skLineSegment(sketch, "E1210.MirrorCS", {"start": v(1819.6, 22.3) * mm, "end": v(1819.6, 13.3) * mm});
            skLineSegment(sketch, "E1211.MirrorCS", {"start": v(1819.6, 13.3) * mm, "end": v(1814.1, 13.3) * mm});
            skLineSegment(sketch, "E1212.MirrorCS", {"start": v(1809.1, 13.3) * mm, "end": v(1802.1, 13.3) * mm});
            skLineSegment(sketch, "E1213.MirrorCS", {"start": v(1797.1, 13.3) * mm, "end": v(1789.6, 13.3) * mm});
            skLineSegment(sketch, "E1214.MirrorCS", {"start": v(1815.04, 8) * mm, "end": v(1814.1, 13.3) * mm});
            skLineSegment(sketch, "E1215.MirrorCS", {"start": v(1807.54, 8) * mm, "end": v(1802.1, 8) * mm});
            skLineSegment(sketch, "E1216", {"start": v(1782.1, 8) * mm, "end": v(1789.6, 8) * mm});
            skLineSegment(sketch, "E1217.MirrorCS", {"start": v(1797.1, 8) * mm, "end": v(1789.6, 8) * mm});
            skLineSegment(sketch, "E1218.MirrorCS", {"start": v(1823.04, 0) * mm, "end": v(1823.04, 8) * mm});
            skLineSegment(sketch, "E1219.MirrorCS", {"start": v(1823.04, 8) * mm, "end": v(1815.04, 8) * mm});
            skLineSegment(sketch, "E1220", {"start": v(1771.67, 8) * mm, "end": v(1770.1, 13.3) * mm});
            skLineSegment(sketch, "E1221", {"start": v(1777.1, 13.3) * mm, "end": v(1777.1, 8) * mm});
            skLineSegment(sketch, "E1222", {"start": v(1782.1, 8) * mm, "end": v(1782.1, 13.3) * mm});
            skLineSegment(sketch, "E1223.MirrorCS", {"start": v(1807.54, 8) * mm, "end": v(1809.1, 13.3) * mm});
            skLineSegment(sketch, "E1224.MirrorCS", {"start": v(1802.1, 13.3) * mm, "end": v(1802.1, 8) * mm});
            skLineSegment(sketch, "E1225.MirrorCS", {"start": v(1797.1, 8) * mm, "end": v(1797.1, 13.3) * mm});
            skLineSegment(sketch, "E1226", {"start": v(1727.49, 13.3) * mm, "end": v(1841.92, 13.3) * mm, "construction": true});
            skLineSegment(sketch, "E1227", {"start": v(1931.52, 17.3) * mm, "end": v(1931.52, 0) * mm, "construction": true});
            skLineSegment(sketch, "E1228", {"start": v(1844.97, 0) * mm, "end": v(1986.9, 0) * mm, "construction": true});
            skLineSegment(sketch, "E1229.bottom", {"start": v(1907.02, 16.9) * mm, "end": v(1931.52, 16.9) * mm});
            skLineSegment(sketch, "E1229.top", {"start": v(1912.02, 8.9) * mm, "end": v(1919.02, 8.9) * mm});
            skLineSegment(sketch, "E1229.left", {"start": v(1907.02, 16.9) * mm, "end": v(1907.02, 14.9) * mm});
            skLineSegment(sketch, "E1230.bottom", {"start": v(1898.33, 0) * mm, "end": v(1964.7, 0) * mm});
            skLineSegment(sketch, "E1230.left", {"start": v(1898.33, 0) * mm, "end": v(1898.33, 5) * mm});
            skLineSegment(sketch, "E1231", {"start": v(1906.33, 5) * mm, "end": v(1907.02, 8.9) * mm});
            skLineSegment(sketch, "E1232", {"start": v(1898.33, 5) * mm, "end": v(1906.33, 5) * mm});
            skLineSegment(sketch, "E1233.bottom", {"start": v(1901.52, 17.9) * mm, "end": v(1906.52, 17.9) * mm});
            skLineSegment(sketch, "E1233.top", {"start": v(1901.52, 8.9) * mm, "end": v(1907.02, 8.9) * mm});
            skLineSegment(sketch, "E1233.left", {"start": v(1901.52, 17.9) * mm, "end": v(1901.52, 8.9) * mm});
            skLineSegment(sketch, "E1234.right", {"start": v(1906.52, 17.9) * mm, "end": v(1906.52, 14.9) * mm});
            skLineSegment(sketch, "E1235", {"start": v(1906.52, 14.9) * mm, "end": v(1907.02, 14.9) * mm});
            skLineSegment(sketch, "E1236.trimOffspring", {"start": v(1913.83, 5) * mm, "end": v(1919.02, 5) * mm});
            skLineSegment(sketch, "E1237", {"start": v(1924.02, 8.9) * mm, "end": v(1931.52, 8.9) * mm});
            skLineSegment(sketch, "E1238.MirrorCS", {"start": v(1956.02, 16.9) * mm, "end": v(1931.52, 16.9) * mm});
            skLineSegment(sketch, "E1239.MirrorCS", {"start": v(1956.02, 16.9) * mm, "end": v(1956.02, 14.9) * mm});
            skLineSegment(sketch, "E1240.MirrorCS", {"start": v(1956.52, 14.9) * mm, "end": v(1956.02, 14.9) * mm});
            skLineSegment(sketch, "E1241.MirrorCS", {"start": v(1956.52, 17.9) * mm, "end": v(1956.52, 14.9) * mm});
            skLineSegment(sketch, "E1242.MirrorCS", {"start": v(1961.52, 17.9) * mm, "end": v(1956.52, 17.9) * mm});
            skLineSegment(sketch, "E1243.MirrorCS", {"start": v(1961.52, 17.9) * mm, "end": v(1961.52, 8.9) * mm});
            skLineSegment(sketch, "E1244.MirrorCS", {"start": v(1961.52, 8.9) * mm, "end": v(1956.02, 8.9) * mm});
            skLineSegment(sketch, "E1245.MirrorCS", {"start": v(1951.02, 8.9) * mm, "end": v(1944.02, 8.9) * mm});
            skLineSegment(sketch, "E1246.MirrorCS", {"start": v(1939.02, 8.9) * mm, "end": v(1931.52, 8.9) * mm});
            skLineSegment(sketch, "E1247.MirrorCS", {"start": v(1956.7, 5) * mm, "end": v(1956.02, 8.9) * mm});
            skLineSegment(sketch, "E1248.MirrorCS", {"start": v(1949.2, 5) * mm, "end": v(1944.02, 5) * mm});
            skLineSegment(sketch, "E1249", {"start": v(1924.02, 5) * mm, "end": v(1931.52, 5) * mm});
            skLineSegment(sketch, "E1250.MirrorCS", {"start": v(1939.02, 5) * mm, "end": v(1931.52, 5) * mm});
            skLineSegment(sketch, "E1251.MirrorCS", {"start": v(1964.7, 0) * mm, "end": v(1964.7, 5) * mm});
            skLineSegment(sketch, "E1252.MirrorCS", {"start": v(1964.7, 5) * mm, "end": v(1956.7, 5) * mm});
            skLineSegment(sketch, "E1253", {"start": v(1913.83, 5) * mm, "end": v(1912.02, 8.9) * mm});
            skLineSegment(sketch, "E1254", {"start": v(1919.02, 8.9) * mm, "end": v(1919.02, 5) * mm});
            skLineSegment(sketch, "E1255", {"start": v(1924.02, 5) * mm, "end": v(1924.02, 8.9) * mm});
            skLineSegment(sketch, "E1256.MirrorCS", {"start": v(1949.2, 5) * mm, "end": v(1951.02, 8.9) * mm});
            skLineSegment(sketch, "E1257.MirrorCS", {"start": v(1944.02, 8.9) * mm, "end": v(1944.02, 5) * mm});
            skLineSegment(sketch, "E1258.MirrorCS", {"start": v(1939.02, 5) * mm, "end": v(1939.02, 8.9) * mm});
            skLineSegment(sketch, "E1259", {"start": v(1869.4, 8.9) * mm, "end": v(1983.85, 8.9) * mm, "construction": true});
            skLineSegment(sketch, "E1260", {"start": v(2072.14, 29.71) * mm, "end": v(2072.14, 0) * mm, "construction": true});
            skLineSegment(sketch, "E1261.bottom", {"start": v(2047.64, 12.5) * mm, "end": v(2072.14, 12.5) * mm});
            skLineSegment(sketch, "E1261.left", {"start": v(2047.64, 12.5) * mm, "end": v(2047.64, 10.5) * mm});
            skLineSegment(sketch, "E1262.left", {"start": v(2038.76, 0) * mm, "end": v(2038.76, 4.5) * mm});
            skLineSegment(sketch, "E1263", {"start": v(2046.76, 4.5) * mm, "end": v(2047.64, 4.5) * mm});
            skLineSegment(sketch, "E1264", {"start": v(2038.76, 4.5) * mm, "end": v(2046.76, 4.5) * mm});
            skLineSegment(sketch, "E1265.bottom", {"start": v(2042.14, 13.5) * mm, "end": v(2047.14, 13.5) * mm});
            skLineSegment(sketch, "E1265.top", {"start": v(2042.14, 4.5) * mm, "end": v(2047.64, 4.5) * mm});
            skLineSegment(sketch, "E1265.left", {"start": v(2042.14, 13.5) * mm, "end": v(2042.14, 4.5) * mm});
            skLineSegment(sketch, "E1266.right", {"start": v(2047.14, 13.5) * mm, "end": v(2047.14, 10.5) * mm});
            skLineSegment(sketch, "E1267", {"start": v(2047.14, 10.5) * mm, "end": v(2047.64, 10.5) * mm});
            skLineSegment(sketch, "E1268.MirrorCS", {"start": v(2096.64, 12.5) * mm, "end": v(2072.14, 12.5) * mm});
            skLineSegment(sketch, "E1269.MirrorCS", {"start": v(2096.64, 12.5) * mm, "end": v(2096.64, 10.5) * mm});
            skLineSegment(sketch, "E1270.MirrorCS", {"start": v(2097.14, 10.5) * mm, "end": v(2096.64, 10.5) * mm});
            skLineSegment(sketch, "E1271.MirrorCS", {"start": v(2097.14, 13.5) * mm, "end": v(2097.14, 10.5) * mm});
            skLineSegment(sketch, "E1272.MirrorCS", {"start": v(2102.14, 13.5) * mm, "end": v(2097.14, 13.5) * mm});
            skLineSegment(sketch, "E1273.MirrorCS", {"start": v(2102.14, 13.5) * mm, "end": v(2102.14, 4.5) * mm});
            skLineSegment(sketch, "E1274.MirrorCS", {"start": v(2102.14, 4.5) * mm, "end": v(2096.64, 4.5) * mm});
            skLineSegment(sketch, "E1275.MirrorCS", {"start": v(2097.52, 4.5) * mm, "end": v(2096.64, 4.5) * mm});
            skLineSegment(sketch, "E1276.MirrorCS", {"start": v(2105.52, 0) * mm, "end": v(2105.52, 4.5) * mm});
            skLineSegment(sketch, "E1277.MirrorCS", {"start": v(2105.52, 4.5) * mm, "end": v(2097.52, 4.5) * mm});
            skLineSegment(sketch, "E1278", {"start": v(2011.33, 4.5) * mm, "end": v(2125.77, 4.5) * mm, "construction": true});
            skLineSegment(sketch, "E1279", {"start": v(2038.76, 0) * mm, "end": v(2105.52, 0) * mm});
            skLineSegment(sketch, "E1280", {"start": v(2234.88, 65.8) * mm, "end": v(2234.88, 36.1) * mm, "construction": true});
            skLineSegment(sketch, "E1281.bottom", {"start": v(2210.38, 11.4) * mm, "end": v(2234.88, 11.4) * mm});
            skLineSegment(sketch, "E1281.left", {"start": v(2210.38, 11.4) * mm, "end": v(2210.38, 9.4) * mm});
            skLineSegment(sketch, "E1282.left", {"start": v(2201.5, 0) * mm, "end": v(2201.5, 3.4) * mm});
            skLineSegment(sketch, "E1283", {"start": v(2209.5, 3.4) * mm, "end": v(2210.38, 3.4) * mm});
            skLineSegment(sketch, "E1284", {"start": v(2201.5, 3.4) * mm, "end": v(2209.5, 3.4) * mm});
            skLineSegment(sketch, "E1285.bottom", {"start": v(2204.88, 12.4) * mm, "end": v(2209.88, 12.4) * mm});
            skLineSegment(sketch, "E1285.top", {"start": v(2204.88, 3.4) * mm, "end": v(2210.38, 3.4) * mm});
            skLineSegment(sketch, "E1285.left", {"start": v(2204.88, 12.4) * mm, "end": v(2204.88, 3.4) * mm});
            skLineSegment(sketch, "E1286.right", {"start": v(2209.88, 12.4) * mm, "end": v(2209.88, 9.4) * mm});
            skLineSegment(sketch, "E1287", {"start": v(2209.88, 9.4) * mm, "end": v(2210.38, 9.4) * mm});
            skLineSegment(sketch, "E1288.MirrorCS", {"start": v(2259.38, 11.4) * mm, "end": v(2234.88, 11.4) * mm});
            skLineSegment(sketch, "E1289.MirrorCS", {"start": v(2259.38, 11.4) * mm, "end": v(2259.38, 9.4) * mm});
            skLineSegment(sketch, "E1290.MirrorCS", {"start": v(2259.88, 9.4) * mm, "end": v(2259.38, 9.4) * mm});
            skLineSegment(sketch, "E1291.MirrorCS", {"start": v(2259.88, 12.4) * mm, "end": v(2259.88, 9.4) * mm});
            skLineSegment(sketch, "E1292.MirrorCS", {"start": v(2264.88, 12.4) * mm, "end": v(2259.88, 12.4) * mm});
            skLineSegment(sketch, "E1293.MirrorCS", {"start": v(2264.88, 12.4) * mm, "end": v(2264.88, 3.4) * mm});
            skLineSegment(sketch, "E1294.MirrorCS", {"start": v(2264.88, 3.4) * mm, "end": v(2259.38, 3.4) * mm});
            skLineSegment(sketch, "E1295.MirrorCS", {"start": v(2260.27, 3.4) * mm, "end": v(2259.38, 3.4) * mm});
            skLineSegment(sketch, "E1296.MirrorCS", {"start": v(2268.27, 0) * mm, "end": v(2268.27, 3.4) * mm});
            skLineSegment(sketch, "E1297.MirrorCS", {"start": v(2268.27, 3.4) * mm, "end": v(2260.27, 3.4) * mm});
            skLineSegment(sketch, "E1298", {"start": v(2174.07, 3.4) * mm, "end": v(2288.51, 3.4) * mm, "construction": true});
            skLineSegment(sketch, "E1299", {"start": v(2201.5, 0) * mm, "end": v(2268.27, 0) * mm});
            skLineSegment(sketch, "E1300", {"start": v(2417.97, 24.21) * mm, "end": v(2417.97, -5.5) * mm, "construction": true});
            skLineSegment(sketch, "E1301.bottom", {"start": v(2393.47, 7) * mm, "end": v(2417.97, 7) * mm});
            skLineSegment(sketch, "E1301.left", {"start": v(2393.47, 7) * mm, "end": v(2393.47, 5) * mm});
            skLineSegment(sketch, "E1302.bottom", {"start": v(2387.97, 8) * mm, "end": v(2392.97, 8) * mm});
            skLineSegment(sketch, "E1302.left", {"start": v(2387.97, 8) * mm, "end": v(2387.97, 0) * mm});
            skLineSegment(sketch, "E1303.right", {"start": v(2392.97, 8) * mm, "end": v(2392.97, 5) * mm});
            skLineSegment(sketch, "E1304", {"start": v(2392.97, 5) * mm, "end": v(2393.47, 5) * mm});
            skLineSegment(sketch, "E1305.MirrorCS", {"start": v(2442.47, 7) * mm, "end": v(2417.97, 7) * mm});
            skLineSegment(sketch, "E1306.MirrorCS", {"start": v(2442.47, 7) * mm, "end": v(2442.47, 5) * mm});
            skLineSegment(sketch, "E1307.MirrorCS", {"start": v(2442.97, 5) * mm, "end": v(2442.47, 5) * mm});
            skLineSegment(sketch, "E1308.MirrorCS", {"start": v(2442.97, 8) * mm, "end": v(2442.97, 5) * mm});
            skLineSegment(sketch, "E1309.MirrorCS", {"start": v(2447.97, 8) * mm, "end": v(2442.97, 8) * mm});
            skLineSegment(sketch, "E1310.MirrorCS", {"start": v(2447.97, 8) * mm, "end": v(2447.97, 0) * mm});
            skLineSegment(sketch, "E1311", {"start": v(2387.97, 0) * mm, "end": v(2447.97, 0) * mm});
            skLineSegment(sketch, "E1312", {"start": v(2553.04, 19.71) * mm, "end": v(2553.04, -10) * mm, "construction": true});
            skLineSegment(sketch, "E1313.bottom", {"start": v(2528.54, 2.5) * mm, "end": v(2553.04, 2.5) * mm});
            skLineSegment(sketch, "E1313.left", {"start": v(2528.54, 2.5) * mm, "end": v(2528.54, 0.5) * mm});
            skLineSegment(sketch, "E1314.bottom", {"start": v(2523.04, 3.5) * mm, "end": v(2528.04, 3.5) * mm});
            skLineSegment(sketch, "E1314.left", {"start": v(2523.04, 3.5) * mm, "end": v(2523.04, 0) * mm});
            skLineSegment(sketch, "E1315.right", {"start": v(2528.04, 3.5) * mm, "end": v(2528.04, 0.5) * mm});
            skLineSegment(sketch, "E1316", {"start": v(2528.04, 0.5) * mm, "end": v(2528.54, 0.5) * mm});
            skLineSegment(sketch, "E1317.MirrorCS", {"start": v(2577.54, 2.5) * mm, "end": v(2553.04, 2.5) * mm});
            skLineSegment(sketch, "E1318.MirrorCS", {"start": v(2577.54, 2.5) * mm, "end": v(2577.54, 0.5) * mm});
            skLineSegment(sketch, "E1319.MirrorCS", {"start": v(2578.04, 0.5) * mm, "end": v(2577.54, 0.5) * mm});
            skLineSegment(sketch, "E1320.MirrorCS", {"start": v(2578.04, 3.5) * mm, "end": v(2578.04, 0.5) * mm});
            skLineSegment(sketch, "E1321.MirrorCS", {"start": v(2583.04, 3.5) * mm, "end": v(2578.04, 3.5) * mm});
            skLineSegment(sketch, "E1322.MirrorCS", {"start": v(2583.04, 3.5) * mm, "end": v(2583.04, 0) * mm});
            skLineSegment(sketch, "E1323", {"start": v(2523.04, 0) * mm, "end": v(2583.04, 0) * mm});
            skSolve(sketch);
        }
        {
            var Q0;
            Q0=makeQuery(id+"F0.imprint","IMPRINT",FACE,{"disambiguationData":[TD([[makeQuery(id+"F0.imprint","IMPRINT",EDGE,{"derivedFrom":sQuery(id+"F0.wireOp",EDGE,"E47.bottom")}),-1.0]])]});
            var Q1;
            Q1=makeQuery(id+"F0.imprint","IMPRINT",FACE,{"disambiguationData":[TD([[makeQuery(id+"F0.imprint","IMPRINT",EDGE,{"derivedFrom":sQuery(id+"F0.wireOp",EDGE,"E92.bottom")}),-1.0]])]});
            var Q2;
            Q2=makeQuery(id+"F0.imprint","IMPRINT",FACE,{"disambiguationData":[TD([[makeQuery(id+"F0.imprint","IMPRINT",EDGE,{"derivedFrom":sQuery(id+"F0.wireOp",EDGE,"E137.bottom")}),-1.0]])]});
            var Q3;
            Q3=makeQuery(id+"F0.imprint","IMPRINT",FACE,{"disambiguationData":[TD([[makeQuery(id+"F0.imprint","IMPRINT",EDGE,{"derivedFrom":sQuery(id+"F0.wireOp",EDGE,"E182.bottom")}),-1.0]])]});
            var Q4;
            Q4=makeQuery(id+"F0.imprint","IMPRINT",FACE,{"disambiguationData":[TD([[makeQuery(id+"F0.imprint","IMPRINT",EDGE,{"derivedFrom":sQuery(id+"F0.wireOp",EDGE,"E227.bottom")}),-1.0]])]});
            var Q5;
            Q5=makeQuery(id+"F0.imprint","IMPRINT",FACE,{"disambiguationData":[TD([[makeQuery(id+"F0.imprint","IMPRINT",EDGE,{"derivedFrom":sQuery(id+"F0.wireOp",EDGE,"E272.bottom")}),-1.0]])]});
            var Q6;
            Q6=makeQuery(id+"F0.imprint","IMPRINT",FACE,{"disambiguationData":[TD([[makeQuery(id+"F0.imprint","IMPRINT",EDGE,{"derivedFrom":sQuery(id+"F0.wireOp",EDGE,"E317.bottom")}),-1.0]])]});
            var Q7;
            Q7=makeQuery(id+"F0.imprint","IMPRINT",FACE,{"disambiguationData":[TD([[makeQuery(id+"F0.imprint","IMPRINT",EDGE,{"derivedFrom":sQuery(id+"F0.wireOp",EDGE,"E362.bottom")}),-1.0]])]});
            var Q8;
            Q8=makeQuery(id+"F0.imprint","IMPRINT",FACE,{"disambiguationData":[TD([[makeQuery(id+"F0.imprint","IMPRINT",EDGE,{"derivedFrom":sQuery(id+"F0.wireOp",EDGE,"E407.bottom")}),-1.0]])]});
            var Q9;
            Q9=makeQuery(id+"F0.imprint","IMPRINT",FACE,{"disambiguationData":[TD([[makeQuery(id+"F0.imprint","IMPRINT",EDGE,{"derivedFrom":sQuery(id+"F0.wireOp",EDGE,"E452.bottom")}),-1.0]])]});
            var Q10;
            Q10=makeQuery(id+"F0.imprint","IMPRINT",FACE,{"disambiguationData":[TD([[makeQuery(id+"F0.imprint","IMPRINT",EDGE,{"derivedFrom":sQuery(id+"F0.wireOp",EDGE,"E497.bottom")}),-1.0]])]});
            var Q11;
            Q11=makeQuery(id+"F0.imprint","IMPRINT",FACE,{"disambiguationData":[TD([[makeQuery(id+"F0.imprint","IMPRINT",EDGE,{"derivedFrom":sQuery(id+"F0.wireOp",EDGE,"E542.bottom")}),-1.0]])]});
            var Q12;
            Q12=makeQuery(id+"F0.imprint","IMPRINT",FACE,{"disambiguationData":[TD([[makeQuery(id+"F0.imprint","IMPRINT",EDGE,{"derivedFrom":sQuery(id+"F0.wireOp",EDGE,"E587.bottom")}),-1.0]])]});
            var Q13;
            Q13=makeQuery(id+"F0.imprint","IMPRINT",FACE,{"disambiguationData":[TD([[makeQuery(id+"F0.imprint","IMPRINT",EDGE,{"derivedFrom":sQuery(id+"F0.wireOp",EDGE,"E632.bottom")}),-1.0]])]});
            var Q14;
            Q14=makeQuery(id+"F0.imprint","IMPRINT",FACE,{"disambiguationData":[TD([[makeQuery(id+"F0.imprint","IMPRINT",EDGE,{"derivedFrom":sQuery(id+"F0.wireOp",EDGE,"E677.bottom")}),-1.0]])]});
            extrude(context, id + "F2", {"entities" : qUnion([Q0, Q1, Q2, Q3, Q4, Q5, Q6, Q7, Q8, Q9, Q10, Q11, Q12, Q13, Q14]), "depth" : 5 * mm});
        }
        {
            var Q0;
            Q0=makeQuery(id+"F1.imprint","IMPRINT",FACE,{"disambiguationData":[TD([[makeQuery(id+"F1.imprint","IMPRINT",EDGE,{"derivedFrom":sQuery(id+"F1.wireOp",EDGE,"E800.bottom")}),-1.0]])]});
            var Q1;
            Q1=makeQuery(id+"F1.imprint","IMPRINT",FACE,{"disambiguationData":[TD([[makeQuery(id+"F1.imprint","IMPRINT",EDGE,{"derivedFrom":sQuery(id+"F1.wireOp",EDGE,"E833.bottom")}),-1.0]])]});
            var Q2;
            Q2=makeQuery(id+"F1.imprint","IMPRINT",FACE,{"disambiguationData":[TD([[makeQuery(id+"F1.imprint","IMPRINT",EDGE,{"derivedFrom":sQuery(id+"F1.wireOp",EDGE,"E866.bottom")}),-1.0]])]});
            var Q3;
            Q3=makeQuery(id+"F1.imprint","IMPRINT",FACE,{"disambiguationData":[TD([[makeQuery(id+"F1.imprint","IMPRINT",EDGE,{"derivedFrom":sQuery(id+"F1.wireOp",EDGE,"E899.bottom")}),-1.0]])]});
            var Q4;
            Q4=makeQuery(id+"F1.imprint","IMPRINT",FACE,{"disambiguationData":[TD([[makeQuery(id+"F1.imprint","IMPRINT",EDGE,{"derivedFrom":sQuery(id+"F1.wireOp",EDGE,"E932.bottom")}),-1.0]])]});
            var Q5;
            Q5=makeQuery(id+"F1.imprint","IMPRINT",FACE,{"disambiguationData":[TD([[makeQuery(id+"F1.imprint","IMPRINT",EDGE,{"derivedFrom":sQuery(id+"F1.wireOp",EDGE,"E965.bottom")}),-1.0]])]});
            var Q6;
            Q6=makeQuery(id+"F1.imprint","IMPRINT",FACE,{"disambiguationData":[TD([[makeQuery(id+"F1.imprint","IMPRINT",EDGE,{"derivedFrom":sQuery(id+"F1.wireOp",EDGE,"E998.bottom")}),-1.0]])]});
            var Q7;
            Q7=makeQuery(id+"F1.imprint","IMPRINT",FACE,{"disambiguationData":[TD([[makeQuery(id+"F1.imprint","IMPRINT",EDGE,{"derivedFrom":sQuery(id+"F1.wireOp",EDGE,"E1031.bottom")}),-1.0]])]});
            var Q8;
            Q8=makeQuery(id+"F1.imprint","IMPRINT",FACE,{"disambiguationData":[TD([[makeQuery(id+"F1.imprint","IMPRINT",EDGE,{"derivedFrom":sQuery(id+"F1.wireOp",EDGE,"E1064.bottom")}),-1.0]])]});
            var Q9;
            Q9=makeQuery(id+"F1.imprint","IMPRINT",FACE,{"disambiguationData":[TD([[makeQuery(id+"F1.imprint","IMPRINT",EDGE,{"derivedFrom":sQuery(id+"F1.wireOp",EDGE,"E1097.bottom")}),-1.0]])]});
            var Q10;
            Q10=makeQuery(id+"F1.imprint","IMPRINT",FACE,{"disambiguationData":[TD([[makeQuery(id+"F1.imprint","IMPRINT",EDGE,{"derivedFrom":sQuery(id+"F1.wireOp",EDGE,"E1130.bottom")}),-1.0]])]});
            var Q11;
            Q11=makeQuery(id+"F1.imprint","IMPRINT",FACE,{"disambiguationData":[TD([[makeQuery(id+"F1.imprint","IMPRINT",EDGE,{"derivedFrom":sQuery(id+"F1.wireOp",EDGE,"E1163.bottom")}),-1.0]])]});
            var Q12;
            Q12=makeQuery(id+"F1.imprint","IMPRINT",FACE,{"disambiguationData":[TD([[makeQuery(id+"F1.imprint","IMPRINT",EDGE,{"derivedFrom":sQuery(id+"F1.wireOp",EDGE,"E1196.bottom")}),-1.0]])]});
            var Q13;
            Q13=makeQuery(id+"F1.imprint","IMPRINT",FACE,{"disambiguationData":[TD([[makeQuery(id+"F1.imprint","IMPRINT",EDGE,{"derivedFrom":sQuery(id+"F1.wireOp",EDGE,"E1229.bottom")}),-1.0]])]});
            var Q14;
            Q14=makeQuery(id+"F1.imprint","IMPRINT",FACE,{"disambiguationData":[TD([[makeQuery(id+"F1.imprint","IMPRINT",EDGE,{"derivedFrom":sQuery(id+"F1.wireOp",EDGE,"E1261.bottom")}),-1.0]])]});
            var Q15;
            Q15=makeQuery(id+"F1.imprint","IMPRINT",FACE,{"disambiguationData":[TD([[makeQuery(id+"F1.imprint","IMPRINT",EDGE,{"derivedFrom":sQuery(id+"F1.wireOp",EDGE,"E1281.bottom")}),-1.0]])]});
            var Q16;
            Q16=makeQuery(id+"F1.imprint","IMPRINT",FACE,{"disambiguationData":[TD([[makeQuery(id+"F1.imprint","IMPRINT",EDGE,{"derivedFrom":sQuery(id+"F1.wireOp",EDGE,"E1301.bottom")}),-1.0]])]});
            var Q17;
            Q17=makeQuery(id+"F1.imprint","IMPRINT",FACE,{"disambiguationData":[TD([[makeQuery(id+"F1.imprint","IMPRINT",EDGE,{"derivedFrom":sQuery(id+"F1.wireOp",EDGE,"E1313.bottom")}),-1.0]])]});
            extrude(context, id + "F3", {"entities" : qUnion([Q0, Q1, Q2, Q3, Q4, Q5, Q6, Q7, Q8, Q9, Q10, Q11, Q12, Q13, Q14, Q15, Q16, Q17]), "depth" : 5 * mm});
        }
    });
